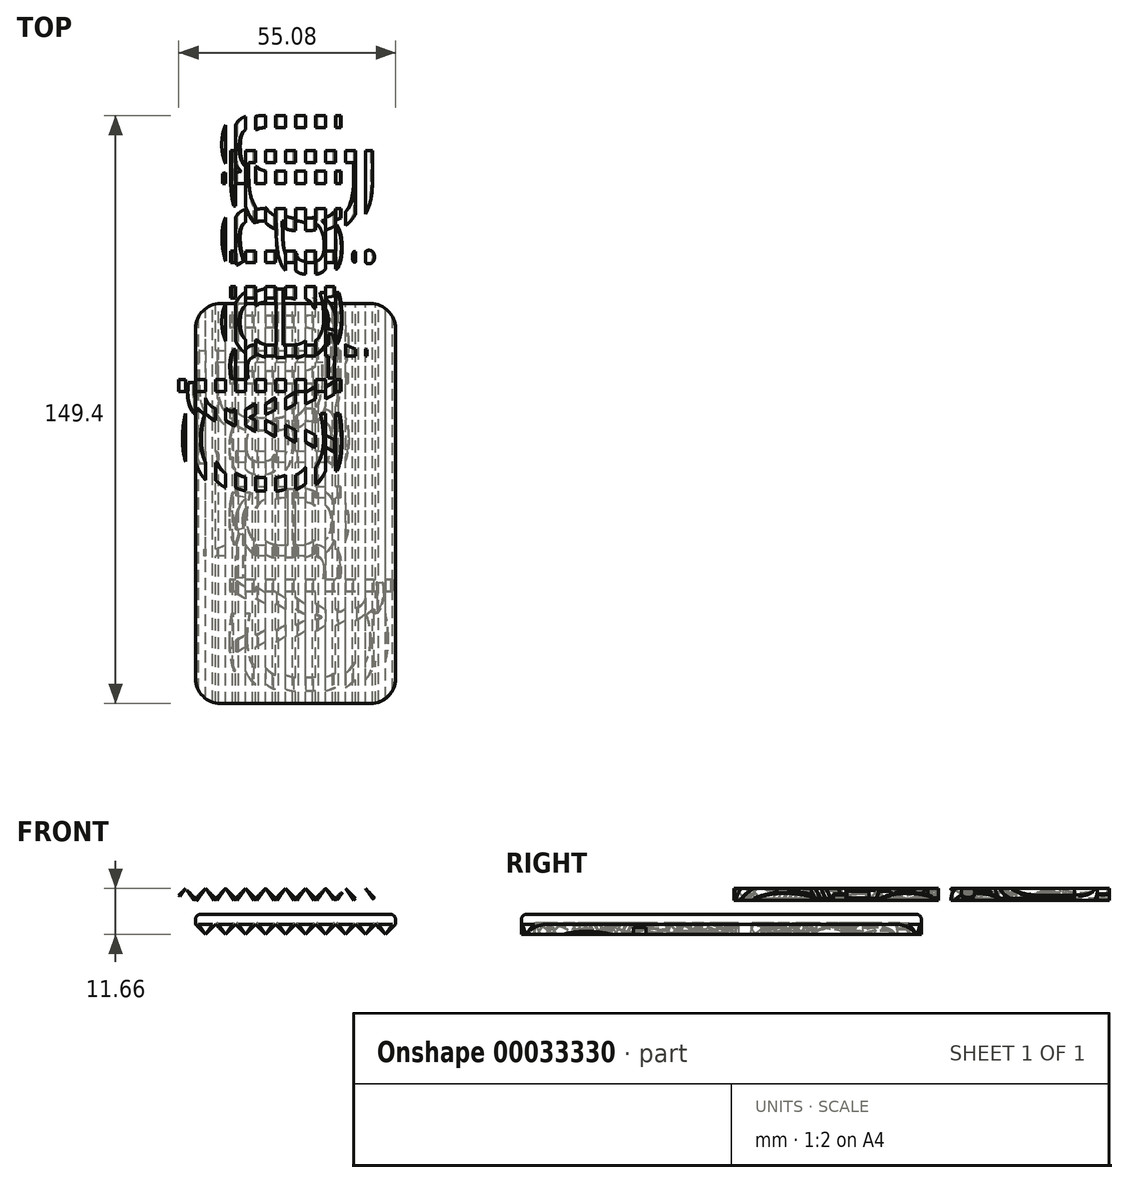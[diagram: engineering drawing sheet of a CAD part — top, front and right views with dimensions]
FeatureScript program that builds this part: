
annotation { "Feature Type Name" : "Feature", "Feature Type Description" : "" }
export const myFeature = defineFeature(function(context is Context, id is Id, definition is map)
    precondition{}
    {
        {
            var Q0;
            Q0=qCreatedBy(makeId("Front.planeOp"),FACE);
            var sketch = newSketch(context, id + "F0", { "sketchPlane" : qUnion([Q0])});
            skLineSegment(sketch, "E0.bottom", {"start": v(-20.32, 0) * mm, "end": v(30.48, 0) * mm});
            skLineSegment(sketch, "E0.top", {"start": v(-20.32, -2.54) * mm, "end": v(30.48, -2.54) * mm});
            skLineSegment(sketch, "E0.left", {"start": v(-20.32, 0) * mm, "end": v(-20.32, -2.54) * mm});
            skLineSegment(sketch, "E0.right", {"start": v(30.48, 0) * mm, "end": v(30.48, -2.54) * mm});
            skLineSegment(sketch, "E1", {"start": v(-20.32, -2.54) * mm, "end": v(-17.78, -5.08) * mm});
            skLineSegment(sketch, "E2", {"start": v(-17.78, -5.08) * mm, "end": v(-15.24, -2.54) * mm});
            skLineSegment(sketch, "E3", {"start": v(-15.24, -2.54) * mm, "end": v(-12.7, -5.08) * mm});
            skLineSegment(sketch, "E4", {"start": v(-12.7, -5.08) * mm, "end": v(-10.16, -2.54) * mm});
            skLineSegment(sketch, "E5", {"start": v(-10.16, -2.54) * mm, "end": v(-7.62, -5.08) * mm});
            skLineSegment(sketch, "E6", {"start": v(-7.62, -5.08) * mm, "end": v(-5.08, -2.54) * mm});
            skLineSegment(sketch, "E7", {"start": v(-5.08, -2.54) * mm, "end": v(-2.54, -5.08) * mm});
            skLineSegment(sketch, "E8", {"start": v(-2.54, -5.08) * mm, "end": v(0, -2.54) * mm});
            skLineSegment(sketch, "E9", {"start": v(0, -2.54) * mm, "end": v(2.54, -5.08) * mm});
            skLineSegment(sketch, "E10", {"start": v(2.54, -5.08) * mm, "end": v(5.08, -2.54) * mm});
            skLineSegment(sketch, "E11", {"start": v(5.08, -2.54) * mm, "end": v(7.62, -5.08) * mm});
            skLineSegment(sketch, "E12", {"start": v(7.62, -5.08) * mm, "end": v(10.16, -2.54) * mm});
            skLineSegment(sketch, "E13", {"start": v(10.16, -2.54) * mm, "end": v(12.7, -5.08) * mm});
            skLineSegment(sketch, "E14", {"start": v(12.7, -5.08) * mm, "end": v(15.24, -2.54) * mm});
            skLineSegment(sketch, "E15", {"start": v(15.24, -2.54) * mm, "end": v(17.78, -5.08) * mm});
            skLineSegment(sketch, "E16", {"start": v(17.78, -5.08) * mm, "end": v(20.32, -2.54) * mm});
            skLineSegment(sketch, "E17", {"start": v(20.32, -2.54) * mm, "end": v(22.86, -5.08) * mm});
            skLineSegment(sketch, "E18", {"start": v(22.86, -5.08) * mm, "end": v(25.4, -2.54) * mm});
            skLineSegment(sketch, "E19", {"start": v(25.4, -2.54) * mm, "end": v(27.94, -5.08) * mm});
            skLineSegment(sketch, "E20", {"start": v(27.94, -5.08) * mm, "end": v(30.48, -2.54) * mm});
            skLineSegment(sketch, "E21", {"start": v(-17.78, -5.08) * mm, "end": v(-19.56, -2.54) * mm});
            skLineSegment(sketch, "E22", {"start": v(-17.78, -5.08) * mm, "end": v(-16, -2.54) * mm});
            skLineSegment(sketch, "E23", {"start": v(-12.7, -5.08) * mm, "end": v(-14.48, -2.54) * mm});
            skLineSegment(sketch, "E24", {"start": v(-12.7, -5.08) * mm, "end": v(-10.92, -2.54) * mm});
            skLineSegment(sketch, "E25", {"start": v(-7.62, -5.08) * mm, "end": v(-9.4, -2.54) * mm});
            skLineSegment(sketch, "E26", {"start": v(-7.62, -5.08) * mm, "end": v(-5.84, -2.54) * mm});
            skLineSegment(sketch, "E27", {"start": v(-2.54, -5.08) * mm, "end": v(-4.32, -2.54) * mm});
            skLineSegment(sketch, "E28", {"start": v(-2.54, -5.08) * mm, "end": v(-0.76, -2.54) * mm});
            skLineSegment(sketch, "E29", {"start": v(2.54, -5.08) * mm, "end": v(0.76, -2.54) * mm});
            skLineSegment(sketch, "E30", {"start": v(2.54, -5.08) * mm, "end": v(4.32, -2.54) * mm});
            skLineSegment(sketch, "E31", {"start": v(7.62, -5.08) * mm, "end": v(9.4, -2.54) * mm});
            skLineSegment(sketch, "E32", {"start": v(7.62, -5.08) * mm, "end": v(5.84, -2.54) * mm});
            skLineSegment(sketch, "E33", {"start": v(12.7, -5.08) * mm, "end": v(10.92, -2.54) * mm});
            skLineSegment(sketch, "E34", {"start": v(12.7, -5.08) * mm, "end": v(14.48, -2.54) * mm});
            skLineSegment(sketch, "E35", {"start": v(17.78, -5.08) * mm, "end": v(16, -2.54) * mm});
            skLineSegment(sketch, "E36", {"start": v(17.78, -5.08) * mm, "end": v(19.56, -2.54) * mm});
            skLineSegment(sketch, "E37", {"start": v(22.86, -5.08) * mm, "end": v(24.64, -2.54) * mm});
            skLineSegment(sketch, "E38", {"start": v(22.86, -5.08) * mm, "end": v(21.08, -2.54) * mm});
            skLineSegment(sketch, "E39", {"start": v(27.94, -5.08) * mm, "end": v(29.72, -2.54) * mm});
            skLineSegment(sketch, "E40", {"start": v(27.94, -5.08) * mm, "end": v(26.16, -2.54) * mm});
            skSolve(sketch);
        }
        {
            var Q0;
            Q0=makeQuery(id+"F0.imprint","IMPRINT",FACE,{"disambiguationData":[TD([[makeQuery(id+"F0.imprint","IMPRINT",EDGE,{"derivedFrom":sQuery(id+"F0.wireOp",EDGE,"E0.bottom")}),-1.0]])]});
            var Q1;
            {var subQ1=sQuery(id+"F0.wireOp",EDGE,"E1");Q1=makeQuery(id+"F0.imprint","IMPRINT",FACE,{"disambiguationData":[TD([[makeQuery(id+"F0.imprint","IMPRINT",EDGE,{"derivedFrom":subQ1}),1.0]])]});}
            var Q2;
            {var subQ1=sQuery(id+"F0.wireOp",EDGE,"E21");Q2=makeQuery(id+"F0.imprint","IMPRINT",FACE,{"disambiguationData":[TD([[makeQuery(id+"F0.imprint","IMPRINT",EDGE,{"derivedFrom":subQ1}),-1.0]])]});}
            var Q3;
            {var subQ1=sQuery(id+"F0.wireOp",EDGE,"E2");Q3=makeQuery(id+"F0.imprint","IMPRINT",FACE,{"disambiguationData":[TD([[makeQuery(id+"F0.imprint","IMPRINT",EDGE,{"derivedFrom":subQ1}),1.0]])]});}
            var Q4;
            {var subQ1=sQuery(id+"F0.wireOp",EDGE,"E14");Q4=makeQuery(id+"F0.imprint","IMPRINT",FACE,{"disambiguationData":[TD([[makeQuery(id+"F0.imprint","IMPRINT",EDGE,{"derivedFrom":subQ1}),1.0]])]});}
            var Q5;
            {var subQ1=sQuery(id+"F0.wireOp",EDGE,"E16");Q5=makeQuery(id+"F0.imprint","IMPRINT",FACE,{"disambiguationData":[TD([[makeQuery(id+"F0.imprint","IMPRINT",EDGE,{"derivedFrom":subQ1}),1.0]])]});}
            var Q6;
            {var subQ1=sQuery(id+"F0.wireOp",EDGE,"E19");Q6=makeQuery(id+"F0.imprint","IMPRINT",FACE,{"disambiguationData":[TD([[makeQuery(id+"F0.imprint","IMPRINT",EDGE,{"derivedFrom":subQ1}),1.0]])]});}
            var Q7;
            {var subQ1=sQuery(id+"F0.wireOp",EDGE,"E33");Q7=makeQuery(id+"F0.imprint","IMPRINT",FACE,{"disambiguationData":[TD([[makeQuery(id+"F0.imprint","IMPRINT",EDGE,{"derivedFrom":subQ1}),-1.0]])]});}
            var Q8;
            {var subQ1=sQuery(id+"F0.wireOp",EDGE,"E6");Q8=makeQuery(id+"F0.imprint","IMPRINT",FACE,{"disambiguationData":[TD([[makeQuery(id+"F0.imprint","IMPRINT",EDGE,{"derivedFrom":subQ1}),1.0]])]});}
            var Q9;
            {var subQ1=sQuery(id+"F0.wireOp",EDGE,"E8");Q9=makeQuery(id+"F0.imprint","IMPRINT",FACE,{"disambiguationData":[TD([[makeQuery(id+"F0.imprint","IMPRINT",EDGE,{"derivedFrom":subQ1}),1.0]])]});}
            var Q10;
            {var subQ1=sQuery(id+"F0.wireOp",EDGE,"E13");Q10=makeQuery(id+"F0.imprint","IMPRINT",FACE,{"disambiguationData":[TD([[makeQuery(id+"F0.imprint","IMPRINT",EDGE,{"derivedFrom":subQ1}),1.0]])]});}
            var Q11;
            {var subQ0=sQuery(id+"F0.wireOp",EDGE,"E9");Q11=makeQuery(id+"F0.imprint","IMPRINT",FACE,{"disambiguationData":[TD([[makeQuery(id+"F0.imprint","IMPRINT",EDGE,{"derivedFrom":subQ0}),1.0]])]});}
            var Q12;
            {var subQ1=sQuery(id+"F0.wireOp",EDGE,"E12");Q12=makeQuery(id+"F0.imprint","IMPRINT",FACE,{"disambiguationData":[TD([[makeQuery(id+"F0.imprint","IMPRINT",EDGE,{"derivedFrom":subQ1}),1.0]])]});}
            var Q13;
            {var subQ1=sQuery(id+"F0.wireOp",EDGE,"E11");Q13=makeQuery(id+"F0.imprint","IMPRINT",FACE,{"disambiguationData":[TD([[makeQuery(id+"F0.imprint","IMPRINT",EDGE,{"derivedFrom":subQ1}),1.0]])]});}
            var Q14;
            {var subQ1=sQuery(id+"F0.wireOp",EDGE,"E10");Q14=makeQuery(id+"F0.imprint","IMPRINT",FACE,{"disambiguationData":[TD([[makeQuery(id+"F0.imprint","IMPRINT",EDGE,{"derivedFrom":subQ1}),1.0]])]});}
            var Q15;
            {var subQ1=sQuery(id+"F0.wireOp",EDGE,"E7");Q15=makeQuery(id+"F0.imprint","IMPRINT",FACE,{"disambiguationData":[TD([[makeQuery(id+"F0.imprint","IMPRINT",EDGE,{"derivedFrom":subQ1}),1.0]])]});}
            var Q16;
            {var subQ1=sQuery(id+"F0.wireOp",EDGE,"E25");Q16=makeQuery(id+"F0.imprint","IMPRINT",FACE,{"disambiguationData":[TD([[makeQuery(id+"F0.imprint","IMPRINT",EDGE,{"derivedFrom":subQ1}),-1.0]])]});}
            var Q17;
            {var subQ1=sQuery(id+"F0.wireOp",EDGE,"E15");Q17=makeQuery(id+"F0.imprint","IMPRINT",FACE,{"disambiguationData":[TD([[makeQuery(id+"F0.imprint","IMPRINT",EDGE,{"derivedFrom":subQ1}),1.0]])]});}
            var Q18;
            {var subQ1=sQuery(id+"F0.wireOp",EDGE,"E31");Q18=makeQuery(id+"F0.imprint","IMPRINT",FACE,{"disambiguationData":[TD([[makeQuery(id+"F0.imprint","IMPRINT",EDGE,{"derivedFrom":subQ1}),1.0]])]});}
            var Q19;
            {var subQ1=sQuery(id+"F0.wireOp",EDGE,"E3");Q19=makeQuery(id+"F0.imprint","IMPRINT",FACE,{"disambiguationData":[TD([[makeQuery(id+"F0.imprint","IMPRINT",EDGE,{"derivedFrom":subQ1}),1.0]])]});}
            var Q20;
            {var subQ1=sQuery(id+"F0.wireOp",EDGE,"E4");Q20=makeQuery(id+"F0.imprint","IMPRINT",FACE,{"disambiguationData":[TD([[makeQuery(id+"F0.imprint","IMPRINT",EDGE,{"derivedFrom":subQ1}),1.0]])]});}
            var Q21;
            {var subQ1=sQuery(id+"F0.wireOp",EDGE,"E5");Q21=makeQuery(id+"F0.imprint","IMPRINT",FACE,{"disambiguationData":[TD([[makeQuery(id+"F0.imprint","IMPRINT",EDGE,{"derivedFrom":subQ1}),1.0]])]});}
            var Q22;
            {var subQ0=sQuery(id+"F0.wireOp",EDGE,"E20");Q22=makeQuery(id+"F0.imprint","IMPRINT",FACE,{"disambiguationData":[TD([[makeQuery(id+"F0.imprint","IMPRINT",EDGE,{"derivedFrom":subQ0}),1.0]])]});}
            var Q23;
            {var subQ1=sQuery(id+"F0.wireOp",EDGE,"E27");Q23=makeQuery(id+"F0.imprint","IMPRINT",FACE,{"disambiguationData":[TD([[makeQuery(id+"F0.imprint","IMPRINT",EDGE,{"derivedFrom":subQ1}),-1.0]])]});}
            var Q24;
            {var subQ1=sQuery(id+"F0.wireOp",EDGE,"E35");Q24=makeQuery(id+"F0.imprint","IMPRINT",FACE,{"disambiguationData":[TD([[makeQuery(id+"F0.imprint","IMPRINT",EDGE,{"derivedFrom":subQ1}),-1.0]])]});}
            var Q25;
            {var subQ1=sQuery(id+"F0.wireOp",EDGE,"E39");Q25=makeQuery(id+"F0.imprint","IMPRINT",FACE,{"disambiguationData":[TD([[makeQuery(id+"F0.imprint","IMPRINT",EDGE,{"derivedFrom":subQ1}),1.0]])]});}
            var Q26;
            {var subQ1=sQuery(id+"F0.wireOp",EDGE,"E23");Q26=makeQuery(id+"F0.imprint","IMPRINT",FACE,{"disambiguationData":[TD([[makeQuery(id+"F0.imprint","IMPRINT",EDGE,{"derivedFrom":subQ1}),-1.0]])]});}
            var Q27;
            {var subQ1=sQuery(id+"F0.wireOp",EDGE,"E17");Q27=makeQuery(id+"F0.imprint","IMPRINT",FACE,{"disambiguationData":[TD([[makeQuery(id+"F0.imprint","IMPRINT",EDGE,{"derivedFrom":subQ1}),1.0]])]});}
            var Q28;
            {var subQ1=sQuery(id+"F0.wireOp",EDGE,"E18");Q28=makeQuery(id+"F0.imprint","IMPRINT",FACE,{"disambiguationData":[TD([[makeQuery(id+"F0.imprint","IMPRINT",EDGE,{"derivedFrom":subQ1}),1.0]])]});}
            var Q29;
            {var subQ0=sQuery(id+"F0.wireOp",EDGE,"E29");Q29=makeQuery(id+"F0.imprint","IMPRINT",FACE,{"disambiguationData":[TD([[makeQuery(id+"F0.imprint","IMPRINT",EDGE,{"derivedFrom":subQ0}),-1.0]])]});}
            var Q30;
            {var subQ1=sQuery(id+"F0.wireOp",EDGE,"E37");Q30=makeQuery(id+"F0.imprint","IMPRINT",FACE,{"disambiguationData":[TD([[makeQuery(id+"F0.imprint","IMPRINT",EDGE,{"derivedFrom":subQ1}),1.0]])]});}
            extrude(context, id + "F1", {"entities" : qUnion([Q0, Q1, Q2, Q3, Q4, Q5, Q6, Q7, Q8, Q9, Q10, Q11, Q12, Q13, Q14, Q15, Q16, Q17, Q18, Q19, Q20, Q21, Q22, Q23, Q24, Q25, Q26, Q27, Q28, Q29, Q30]), "depth" : 101.6 * mm});
        }
        {
            var Q0;
            {var subQ1=sQuery(id+"F0.wireOp",EDGE,"E39");Q0=makeQuery(id+"F0.imprint","IMPRINT",FACE,{"disambiguationData":[TD([[makeQuery(id+"F0.imprint","IMPRINT",EDGE,{"derivedFrom":subQ1}),1.0]])]});}
            var Q1;
            {var subQ1=sQuery(id+"F0.wireOp",EDGE,"E37");Q1=makeQuery(id+"F0.imprint","IMPRINT",FACE,{"disambiguationData":[TD([[makeQuery(id+"F0.imprint","IMPRINT",EDGE,{"derivedFrom":subQ1}),1.0]])]});}
            var Q2;
            {var subQ1=sQuery(id+"F0.wireOp",EDGE,"E35");Q2=makeQuery(id+"F0.imprint","IMPRINT",FACE,{"disambiguationData":[TD([[makeQuery(id+"F0.imprint","IMPRINT",EDGE,{"derivedFrom":subQ1}),-1.0]])]});}
            var Q3;
            {var subQ1=sQuery(id+"F0.wireOp",EDGE,"E33");Q3=makeQuery(id+"F0.imprint","IMPRINT",FACE,{"disambiguationData":[TD([[makeQuery(id+"F0.imprint","IMPRINT",EDGE,{"derivedFrom":subQ1}),-1.0]])]});}
            var Q4;
            {var subQ1=sQuery(id+"F0.wireOp",EDGE,"E31");Q4=makeQuery(id+"F0.imprint","IMPRINT",FACE,{"disambiguationData":[TD([[makeQuery(id+"F0.imprint","IMPRINT",EDGE,{"derivedFrom":subQ1}),1.0]])]});}
            var Q5;
            {var subQ0=sQuery(id+"F0.wireOp",EDGE,"E29");Q5=makeQuery(id+"F0.imprint","IMPRINT",FACE,{"disambiguationData":[TD([[makeQuery(id+"F0.imprint","IMPRINT",EDGE,{"derivedFrom":subQ0}),-1.0]])]});}
            var Q6;
            {var subQ1=sQuery(id+"F0.wireOp",EDGE,"E27");Q6=makeQuery(id+"F0.imprint","IMPRINT",FACE,{"disambiguationData":[TD([[makeQuery(id+"F0.imprint","IMPRINT",EDGE,{"derivedFrom":subQ1}),-1.0]])]});}
            var Q7;
            {var subQ1=sQuery(id+"F0.wireOp",EDGE,"E25");Q7=makeQuery(id+"F0.imprint","IMPRINT",FACE,{"disambiguationData":[TD([[makeQuery(id+"F0.imprint","IMPRINT",EDGE,{"derivedFrom":subQ1}),-1.0]])]});}
            var Q8;
            {var subQ1=sQuery(id+"F0.wireOp",EDGE,"E23");Q8=makeQuery(id+"F0.imprint","IMPRINT",FACE,{"disambiguationData":[TD([[makeQuery(id+"F0.imprint","IMPRINT",EDGE,{"derivedFrom":subQ1}),-1.0]])]});}
            var Q9;
            {var subQ1=sQuery(id+"F0.wireOp",EDGE,"E21");Q9=makeQuery(id+"F0.imprint","IMPRINT",FACE,{"disambiguationData":[TD([[makeQuery(id+"F0.imprint","IMPRINT",EDGE,{"derivedFrom":subQ1}),-1.0]])]});}
            extrude(context, id + "F2", {"entities" : qUnion([Q0, Q1, Q2, Q3, Q4, Q5, Q6, Q7, Q8, Q9]), "depth" : 101.6 * mm});
        }
        {
            var Q0;
            Q0=makeQuery(id+"F1.opExtrude","SWEPT_FACE",FACE,{"disambiguationData":[OSD([sQuery(id+"F0.wireOp",EDGE,"E16")])]});
            cPlane(context, id + "F3", {"entities" : qUnion([Q0]), "cplaneType" : CPlaneType.OFFSET, "offset" : 12.7 * mm, "width" : 152.4 * mm, "height" : 152.4 * mm});
        }
        {
            var Q0;
            Q0=makeQuery(id+"F1.opExtrude","SWEPT_FACE",FACE,{"disambiguationData":[OSD([sQuery(id+"F0.wireOp",EDGE,"E5")])]});
            cPlane(context, id + "F4", {"entities" : qUnion([Q0]), "cplaneType" : CPlaneType.OFFSET, "offset" : 15.24 * mm, "width" : 152.4 * mm, "height" : 152.4 * mm});
        }
        {
            var Q0;
            Q0=qCreatedBy(id+"F3.planeOp",FACE);
            var sketch = newSketch(context, id + "F5", { "sketchPlane" : qUnion([Q0])});
            skText(sketch, "E41", { "text": "Clean", "fontName": "OpenSans-Regular.ttf"});
            skLineSegment(sketch, "E42", {"start": v(-0.73, 16.16) * mm, "end": v(-103.2, 16.16) * mm});
            skLineSegment(sketch, "E43", {"start": v(-103.05, 12.57) * mm, "end": v(-1.71, 12.57) * mm});
            skLineSegment(sketch, "E44", {"start": v(-1.26, 8.98) * mm, "end": v(-105.16, 8.98) * mm});
            skLineSegment(sketch, "E45", {"start": v(-103.35, 5.39) * mm, "end": v(-1.34, 5.39) * mm});
            skLineSegment(sketch, "E46", {"start": v(-1.49, 1.8) * mm, "end": v(-105.62, 1.8) * mm});
            skLineSegment(sketch, "E47", {"start": v(-104.1, -1.8) * mm, "end": v(-1.19, -1.8) * mm});
            skLineSegment(sketch, "E48", {"start": v(-1.56, -5.39) * mm, "end": v(-107.58, -5.39) * mm});
            skLineSegment(sketch, "E49", {"start": v(-104.63, -8.98) * mm, "end": v(-1.03, -8.98) * mm});
            const initialGuessF5  = {"E41": [-0.10082, -0.0107, 1, 0, 0.02779]};
            skSetInitialGuess(sketch, initialGuessF5);
            skSolve(sketch);
        }
        {
            var Q0;
            {var subQ1=sQuery(id+"F5.wireOp",EDGE,"E41.sketch_text.stroke-12");var subQ3=sQuery(id+"F5.wireOp",EDGE,"E41.sketch_text.stroke-11");var subQ5=makeQuery(id+"F5.imprint","INTERSECT",VERTEX,{"derivedFrom":[subQ3,subQ1]});Q0=makeQuery(id+"F5.imprint","IMPRINT",FACE,{"disambiguationData":[TD([[makeQuery(id+"F5.imprint","IMPRINT",EDGE,{"disambiguationData":[TD([[subQ5,1.0]])],"derivedFrom":subQ3}),-1.0]])]});}
            var Q1;
            {var subQ5=sQuery(id+"F5.wireOp",EDGE,"E41.sketch_text.stroke-17");Q1=makeQuery(id+"F5.imprint","IMPRINT",FACE,{"disambiguationData":[TD([[makeQuery(id+"F5.imprint","IMPRINT",EDGE,{"derivedFrom":subQ5}),-1.0]])]});}
            var Q2;
            Q2=makeQuery(id+"F2.opExtrude","SWEPT_FACE",FACE,{"disambiguationData":[OSD([sQuery(id+"F0.wireOp",EDGE,"E39")])]});
            extrude(context, id + "F6", {"entities" : qUnion([Q0, Q1]), "operationType" : NewBodyOperationType.REMOVE, "endBound" : BoundingType.UP_TO_SURFACE, "oppositeDirection" : true, "endBoundEntityFace" : qUnion([Q2]), "depth" : 25.4 * mm});
        }
        {
            var Q0;
            {var subQ11=sQuery(id+"F5.wireOp",EDGE,"E41.sketch_text.stroke-13");Q0=makeQuery(id+"F5.imprint","IMPRINT",FACE,{"disambiguationData":[TD([[makeQuery(id+"F5.imprint","IMPRINT",EDGE,{"derivedFrom":subQ11}),-1.0]])]});}
            var Q1;
            {var subQ1=sQuery(id+"F5.wireOp",EDGE,"E41.sketch_text.stroke-16");var subQ5=sQuery(id+"F5.wireOp",EDGE,"E42");var subQ6=makeQuery(id+"F5.imprint","INTERSECT",VERTEX,{"derivedFrom":[subQ1,subQ5]});Q1=makeQuery(id+"F5.imprint","IMPRINT",FACE,{"disambiguationData":[TD([[makeQuery(id+"F5.imprint","IMPRINT",EDGE,{"disambiguationData":[TD([[subQ6,1.0]])],"derivedFrom":subQ1}),-1.0]])]});}
            var Q2;
            Q2=makeQuery(id+"F2.opExtrude","SWEPT_FACE",FACE,{"disambiguationData":[OSD([sQuery(id+"F0.wireOp",EDGE,"E37")])]});
            extrude(context, id + "F7", {"entities" : qUnion([Q0, Q1]), "operationType" : NewBodyOperationType.REMOVE, "endBound" : BoundingType.UP_TO_SURFACE, "oppositeDirection" : true, "endBoundEntityFace" : qUnion([Q2]), "depth" : 25.4 * mm});
        }
        {
            var Q0;
            {var subQ1=sQuery(id+"F5.wireOp",EDGE,"E41.sketch_text.stroke-1");var subQ6=sQuery(id+"F5.wireOp",EDGE,"E41.sketch_text.stroke-0");var subQ11=makeQuery(id+"F5.imprint","INTERSECT",VERTEX,{"derivedFrom":[subQ6,subQ1]});Q0=makeQuery(id+"F5.imprint","IMPRINT",FACE,{"disambiguationData":[TD([[makeQuery(id+"F5.imprint","IMPRINT",EDGE,{"disambiguationData":[TD([[subQ11,1.0]])],"derivedFrom":subQ6}),-1.0]])]});}
            var Q1;
            {var subQ0=sQuery(id+"F5.wireOp",EDGE,"E44");var subQ1=sQuery(id+"F5.wireOp",EDGE,"E41.sketch_text.stroke-16");var subQ2=makeQuery(id+"F5.imprint","INTERSECT",VERTEX,{"derivedFrom":[subQ1,subQ0]});Q1=makeQuery(id+"F5.imprint","IMPRINT",FACE,{"disambiguationData":[TD([[makeQuery(id+"F5.imprint","IMPRINT",EDGE,{"disambiguationData":[TD([[subQ2,-1.0]])],"derivedFrom":subQ1}),-1.0]])]});}
            var Q2;
            {var subQ1=sQuery(id+"F5.wireOp",EDGE,"E41.sketch_text.stroke-23");var subQ3=sQuery(id+"F5.wireOp",EDGE,"E41.sketch_text.stroke-22");var subQ5=makeQuery(id+"F5.imprint","INTERSECT",VERTEX,{"derivedFrom":[subQ3,subQ1]});Q2=makeQuery(id+"F5.imprint","IMPRINT",FACE,{"disambiguationData":[TD([[makeQuery(id+"F5.imprint","IMPRINT",EDGE,{"disambiguationData":[TD([[subQ5,1.0]])],"derivedFrom":subQ3}),-1.0]])]});}
            var Q3;
            {var subQ5=sQuery(id+"F5.wireOp",EDGE,"E41.sketch_text.stroke-52");Q3=makeQuery(id+"F5.imprint","IMPRINT",FACE,{"disambiguationData":[TD([[makeQuery(id+"F5.imprint","IMPRINT",EDGE,{"derivedFrom":subQ5}),-1.0]])]});}
            var Q4;
            {var subQ5=sQuery(id+"F5.wireOp",EDGE,"E41.sketch_text.stroke-77");Q4=makeQuery(id+"F5.imprint","IMPRINT",FACE,{"disambiguationData":[TD([[makeQuery(id+"F5.imprint","IMPRINT",EDGE,{"derivedFrom":subQ5}),-1.0]])]});}
            var Q5;
            {var subQ5=sQuery(id+"F5.wireOp",EDGE,"E41.sketch_text.stroke-73");Q5=makeQuery(id+"F5.imprint","IMPRINT",FACE,{"disambiguationData":[TD([[makeQuery(id+"F5.imprint","IMPRINT",EDGE,{"derivedFrom":subQ5}),-1.0]])]});}
            var Q6;
            Q6=makeQuery(id+"F2.opExtrude","SWEPT_FACE",FACE,{"disambiguationData":[OSD([sQuery(id+"F0.wireOp",EDGE,"E36")])]});
            extrude(context, id + "F8", {"entities" : qUnion([Q0, Q1, Q2, Q3, Q4, Q5]), "operationType" : NewBodyOperationType.REMOVE, "endBound" : BoundingType.UP_TO_SURFACE, "oppositeDirection" : true, "endBoundEntityFace" : qUnion([Q6]), "depth" : 25.4 * mm});
        }
        {
            var Q0;
            {var subQ1=sQuery(id+"F5.wireOp",EDGE,"E41.sketch_text.stroke-1");var subQ5=sQuery(id+"F5.wireOp",EDGE,"E44");var subQ6=makeQuery(id+"F5.imprint","INTERSECT",VERTEX,{"derivedFrom":[subQ1,subQ5]});Q0=makeQuery(id+"F5.imprint","IMPRINT",FACE,{"disambiguationData":[TD([[makeQuery(id+"F5.imprint","IMPRINT",EDGE,{"disambiguationData":[TD([[subQ6,-1.0]])],"derivedFrom":subQ1}),-1.0]])]});}
            var Q1;
            {var subQ0=sQuery(id+"F5.wireOp",EDGE,"E45");var subQ3=sQuery(id+"F5.wireOp",EDGE,"E41.sketch_text.stroke-16");var subQ4=makeQuery(id+"F5.imprint","INTERSECT",VERTEX,{"derivedFrom":[subQ3,subQ0]});Q1=makeQuery(id+"F5.imprint","IMPRINT",FACE,{"disambiguationData":[TD([[makeQuery(id+"F5.imprint","IMPRINT",EDGE,{"disambiguationData":[TD([[subQ4,-1.0]])],"derivedFrom":subQ3}),-1.0]])]});}
            var Q2;
            {var subQ15=sQuery(id+"F5.wireOp",EDGE,"E41.sketch_text.stroke-33");Q2=makeQuery(id+"F5.imprint","IMPRINT",FACE,{"disambiguationData":[TD([[makeQuery(id+"F5.imprint","IMPRINT",EDGE,{"derivedFrom":subQ15}),-1.0]])]});}
            var Q3;
            {var subQ12=sQuery(id+"F5.wireOp",EDGE,"E41.sketch_text.stroke-48");Q3=makeQuery(id+"F5.imprint","IMPRINT",FACE,{"disambiguationData":[TD([[makeQuery(id+"F5.imprint","IMPRINT",EDGE,{"derivedFrom":subQ12}),-1.0]])]});}
            var Q4;
            {var subQ20=sQuery(id+"F5.wireOp",EDGE,"E41.sketch_text.stroke-67");Q4=makeQuery(id+"F5.imprint","IMPRINT",FACE,{"disambiguationData":[TD([[makeQuery(id+"F5.imprint","IMPRINT",EDGE,{"derivedFrom":subQ20}),-1.0]])]});}
            var Q5;
            Q5=makeQuery(id+"F2.opExtrude","SWEPT_FACE",FACE,{"disambiguationData":[OSD([sQuery(id+"F0.wireOp",EDGE,"E34")])]});
            extrude(context, id + "F9", {"entities" : qUnion([Q0, Q1, Q2, Q3, Q4]), "operationType" : NewBodyOperationType.REMOVE, "endBound" : BoundingType.UP_TO_SURFACE, "oppositeDirection" : true, "endBoundEntityFace" : qUnion([Q5]), "depth" : 25.4 * mm});
        }
        {
            var Q0;
            {var subQ1=sQuery(id+"F5.wireOp",EDGE,"E41.sketch_text.stroke-2");var subQ6=sQuery(id+"F5.wireOp",EDGE,"E41.sketch_text.stroke-1");var subQ11=makeQuery(id+"F5.imprint","INTERSECT",VERTEX,{"derivedFrom":[subQ6,subQ1]});Q0=makeQuery(id+"F5.imprint","IMPRINT",FACE,{"disambiguationData":[TD([[makeQuery(id+"F5.imprint","IMPRINT",EDGE,{"disambiguationData":[TD([[subQ11,1.0]])],"derivedFrom":subQ6}),-1.0]])]});}
            var Q1;
            {var subQ0=sQuery(id+"F5.wireOp",EDGE,"E46");var subQ3=sQuery(id+"F5.wireOp",EDGE,"E41.sketch_text.stroke-16");var subQ4=makeQuery(id+"F5.imprint","INTERSECT",VERTEX,{"derivedFrom":[subQ3,subQ0]});Q1=makeQuery(id+"F5.imprint","IMPRINT",FACE,{"disambiguationData":[TD([[makeQuery(id+"F5.imprint","IMPRINT",EDGE,{"disambiguationData":[TD([[subQ4,-1.0]])],"derivedFrom":subQ3}),-1.0]])]});}
            var Q2;
            {var subQ0=sQuery(id+"F5.wireOp",EDGE,"E46");var subQ3=sQuery(id+"F5.wireOp",EDGE,"E41.sketch_text.stroke-21");var subQ4=makeQuery(id+"F5.imprint","INTERSECT",VERTEX,{"derivedFrom":[subQ3,subQ0]});Q2=makeQuery(id+"F5.imprint","IMPRINT",FACE,{"disambiguationData":[TD([[makeQuery(id+"F5.imprint","IMPRINT",EDGE,{"disambiguationData":[TD([[subQ4,-1.0]])],"derivedFrom":subQ3}),-1.0]])]});}
            var Q3;
            {var subQ3=sQuery(id+"F5.wireOp",EDGE,"E41.sketch_text.stroke-24");var subQ5=sQuery(id+"F5.wireOp",EDGE,"E45");var subQ7=makeQuery(id+"F5.imprint","INTERSECT",VERTEX,{"derivedFrom":[subQ3,subQ5]});Q3=makeQuery(id+"F5.imprint","IMPRINT",FACE,{"disambiguationData":[TD([[makeQuery(id+"F5.imprint","IMPRINT",EDGE,{"disambiguationData":[TD([[subQ7,-1.0]])],"derivedFrom":subQ3}),-1.0]])]});}
            var Q4;
            {var subQ3=sQuery(id+"F5.wireOp",EDGE,"E41.sketch_text.stroke-46");var subQ8=sQuery(id+"F5.wireOp",EDGE,"E41.sketch_text.stroke-47");var subQ11=makeQuery(id+"F5.imprint","INTERSECT",VERTEX,{"derivedFrom":[subQ3,subQ8]});Q4=makeQuery(id+"F5.imprint","IMPRINT",FACE,{"disambiguationData":[TD([[makeQuery(id+"F5.imprint","IMPRINT",EDGE,{"disambiguationData":[TD([[subQ11,1.0]])],"derivedFrom":subQ3}),-1.0]])]});}
            var Q5;
            {var subQ3=sQuery(id+"F5.wireOp",EDGE,"E41.sketch_text.stroke-69");var subQ5=sQuery(id+"F5.wireOp",EDGE,"E45");var subQ7=makeQuery(id+"F5.imprint","INTERSECT",VERTEX,{"derivedFrom":[subQ3,subQ5]});Q5=makeQuery(id+"F5.imprint","IMPRINT",FACE,{"disambiguationData":[TD([[makeQuery(id+"F5.imprint","IMPRINT",EDGE,{"disambiguationData":[TD([[subQ7,-1.0]])],"derivedFrom":subQ3}),-1.0]])]});}
            var Q6;
            {var subQ1=sQuery(id+"F5.wireOp",EDGE,"E41.sketch_text.stroke-65");var subQ6=sQuery(id+"F5.wireOp",EDGE,"E41.sketch_text.stroke-66");var subQ11=makeQuery(id+"F5.imprint","INTERSECT",VERTEX,{"derivedFrom":[subQ1,subQ6]});Q6=makeQuery(id+"F5.imprint","IMPRINT",FACE,{"disambiguationData":[TD([[makeQuery(id+"F5.imprint","IMPRINT",EDGE,{"disambiguationData":[TD([[subQ11,1.0]])],"derivedFrom":subQ1}),-1.0]])]});}
            var Q7;
            Q7=makeQuery(id+"F2.opExtrude","SWEPT_FACE",FACE,{"disambiguationData":[OSD([sQuery(id+"F0.wireOp",EDGE,"E31")])]});
            extrude(context, id + "F10", {"entities" : qUnion([Q0, Q1, Q2, Q3, Q4, Q5, Q6]), "operationType" : NewBodyOperationType.REMOVE, "endBound" : BoundingType.UP_TO_SURFACE, "oppositeDirection" : true, "endBoundEntityFace" : qUnion([Q7]), "depth" : 25.4 * mm});
        }
        {
            var Q0;
            {var subQ1=sQuery(id+"F5.wireOp",EDGE,"E41.sketch_text.stroke-2");var subQ5=sQuery(id+"F5.wireOp",EDGE,"E46");var subQ6=makeQuery(id+"F5.imprint","INTERSECT",VERTEX,{"derivedFrom":[subQ1,subQ5]});Q0=makeQuery(id+"F5.imprint","IMPRINT",FACE,{"disambiguationData":[TD([[makeQuery(id+"F5.imprint","IMPRINT",EDGE,{"disambiguationData":[TD([[subQ6,-1.0]])],"derivedFrom":subQ1}),-1.0]])]});}
            var Q1;
            {var subQ0=sQuery(id+"F5.wireOp",EDGE,"E47");var subQ3=sQuery(id+"F5.wireOp",EDGE,"E41.sketch_text.stroke-16");var subQ4=makeQuery(id+"F5.imprint","INTERSECT",VERTEX,{"derivedFrom":[subQ3,subQ0]});Q1=makeQuery(id+"F5.imprint","IMPRINT",FACE,{"disambiguationData":[TD([[makeQuery(id+"F5.imprint","IMPRINT",EDGE,{"disambiguationData":[TD([[subQ4,-1.0]])],"derivedFrom":subQ3}),-1.0]])]});}
            var Q2;
            {var subQ16=sQuery(id+"F5.wireOp",EDGE,"E41.sketch_text.stroke-25");Q2=makeQuery(id+"F5.imprint","IMPRINT",FACE,{"disambiguationData":[TD([[makeQuery(id+"F5.imprint","IMPRINT",EDGE,{"derivedFrom":subQ16}),-1.0]])]});}
            var Q3;
            {var subQ14=sQuery(id+"F5.wireOp",EDGE,"E41.sketch_text.stroke-45");Q3=makeQuery(id+"F5.imprint","IMPRINT",FACE,{"disambiguationData":[TD([[makeQuery(id+"F5.imprint","IMPRINT",EDGE,{"derivedFrom":subQ14}),-1.0]])]});}
            var Q4;
            {var subQ3=sQuery(id+"F5.wireOp",EDGE,"E41.sketch_text.stroke-70");var subQ7=sQuery(id+"F5.wireOp",EDGE,"E41.sketch_text.stroke-69");var subQ9=makeQuery(id+"F5.imprint","INTERSECT",VERTEX,{"derivedFrom":[subQ7,subQ3]});Q4=makeQuery(id+"F5.imprint","IMPRINT",FACE,{"disambiguationData":[TD([[makeQuery(id+"F5.imprint","IMPRINT",EDGE,{"disambiguationData":[TD([[subQ9,1.0]])],"derivedFrom":subQ7}),-1.0]])]});}
            var Q5;
            {var subQ0=sQuery(id+"F5.wireOp",EDGE,"E47");var subQ1=sQuery(id+"F5.wireOp",EDGE,"E41.sketch_text.stroke-65");var subQ2=makeQuery(id+"F5.imprint","INTERSECT",VERTEX,{"derivedFrom":[subQ1,subQ0]});Q5=makeQuery(id+"F5.imprint","IMPRINT",FACE,{"disambiguationData":[TD([[makeQuery(id+"F5.imprint","IMPRINT",EDGE,{"disambiguationData":[TD([[subQ2,-1.0]])],"derivedFrom":subQ1}),-1.0]])]});}
            var Q6;
            Q6=makeQuery(id+"F2.opExtrude","SWEPT_FACE",FACE,{"disambiguationData":[OSD([sQuery(id+"F0.wireOp",EDGE,"E30")])]});
            extrude(context, id + "F11", {"entities" : qUnion([Q0, Q1, Q2, Q3, Q4, Q5]), "operationType" : NewBodyOperationType.REMOVE, "endBound" : BoundingType.UP_TO_SURFACE, "oppositeDirection" : true, "endBoundEntityFace" : qUnion([Q6]), "depth" : 25.4 * mm});
        }
        {
            var Q0;
            {var subQ1=sQuery(id+"F5.wireOp",EDGE,"E41.sketch_text.stroke-3");var subQ6=sQuery(id+"F5.wireOp",EDGE,"E41.sketch_text.stroke-2");var subQ9=makeQuery(id+"F5.imprint","INTERSECT",VERTEX,{"derivedFrom":[subQ6,subQ1]});Q0=makeQuery(id+"F5.imprint","IMPRINT",FACE,{"disambiguationData":[TD([[makeQuery(id+"F5.imprint","IMPRINT",EDGE,{"disambiguationData":[TD([[subQ9,1.0]])],"derivedFrom":subQ6}),-1.0]])]});}
            var Q1;
            {var subQ0=sQuery(id+"F5.wireOp",EDGE,"E48");var subQ3=sQuery(id+"F5.wireOp",EDGE,"E41.sketch_text.stroke-16");var subQ4=makeQuery(id+"F5.imprint","INTERSECT",VERTEX,{"derivedFrom":[subQ3,subQ0]});Q1=makeQuery(id+"F5.imprint","IMPRINT",FACE,{"disambiguationData":[TD([[makeQuery(id+"F5.imprint","IMPRINT",EDGE,{"disambiguationData":[TD([[subQ4,-1.0]])],"derivedFrom":subQ3}),-1.0]])]});}
            var Q2;
            {var subQ0=sQuery(id+"F5.wireOp",EDGE,"E48");var subQ3=sQuery(id+"F5.wireOp",EDGE,"E41.sketch_text.stroke-20");var subQ4=makeQuery(id+"F5.imprint","INTERSECT",VERTEX,{"derivedFrom":[subQ3,subQ0]});Q2=makeQuery(id+"F5.imprint","IMPRINT",FACE,{"disambiguationData":[TD([[makeQuery(id+"F5.imprint","IMPRINT",EDGE,{"disambiguationData":[TD([[subQ4,-1.0]])],"derivedFrom":subQ3}),-1.0]])]});}
            var Q3;
            {var subQ10=sQuery(id+"F5.wireOp",EDGE,"E41.sketch_text.stroke-62");Q3=makeQuery(id+"F5.imprint","IMPRINT",FACE,{"disambiguationData":[TD([[makeQuery(id+"F5.imprint","IMPRINT",EDGE,{"derivedFrom":subQ10}),-1.0]])]});}
            var Q4;
            {var subQ3=sQuery(id+"F5.wireOp",EDGE,"E41.sketch_text.stroke-55");var subQ5=sQuery(id+"F5.wireOp",EDGE,"E47");var subQ8=makeQuery(id+"F5.imprint","INTERSECT",VERTEX,{"derivedFrom":[subQ3,subQ5]});Q4=makeQuery(id+"F5.imprint","IMPRINT",FACE,{"disambiguationData":[TD([[makeQuery(id+"F5.imprint","IMPRINT",EDGE,{"disambiguationData":[TD([[subQ8,-1.0]])],"derivedFrom":subQ3}),-1.0]])]});}
            var Q5;
            {var subQ3=sQuery(id+"F5.wireOp",EDGE,"E41.sketch_text.stroke-70");var subQ5=sQuery(id+"F5.wireOp",EDGE,"E47");var subQ7=makeQuery(id+"F5.imprint","INTERSECT",VERTEX,{"derivedFrom":[subQ3,subQ5]});Q5=makeQuery(id+"F5.imprint","IMPRINT",FACE,{"disambiguationData":[TD([[makeQuery(id+"F5.imprint","IMPRINT",EDGE,{"disambiguationData":[TD([[subQ7,-1.0]])],"derivedFrom":subQ3}),-1.0]])]});}
            var Q6;
            {var subQ1=sQuery(id+"F5.wireOp",EDGE,"E41.sketch_text.stroke-65");var subQ5=sQuery(id+"F5.wireOp",EDGE,"E48");var subQ6=makeQuery(id+"F5.imprint","INTERSECT",VERTEX,{"derivedFrom":[subQ1,subQ5]});Q6=makeQuery(id+"F5.imprint","IMPRINT",FACE,{"disambiguationData":[TD([[makeQuery(id+"F5.imprint","IMPRINT",EDGE,{"disambiguationData":[TD([[subQ6,-1.0]])],"derivedFrom":subQ1}),-1.0]])]});}
            var Q7;
            Q7=makeQuery(id+"F2.opExtrude","SWEPT_FACE",FACE,{"disambiguationData":[OSD([sQuery(id+"F0.wireOp",EDGE,"E28")])]});
            extrude(context, id + "F12", {"entities" : qUnion([Q0, Q1, Q2, Q3, Q4, Q5, Q6]), "operationType" : NewBodyOperationType.REMOVE, "endBound" : BoundingType.UP_TO_SURFACE, "oppositeDirection" : true, "endBoundEntityFace" : qUnion([Q7]), "depth" : 25.4 * mm});
        }
        {
            var Q0;
            {var subQ11=sQuery(id+"F5.wireOp",EDGE,"E41.sketch_text.stroke-4");Q0=makeQuery(id+"F5.imprint","IMPRINT",FACE,{"disambiguationData":[TD([[makeQuery(id+"F5.imprint","IMPRINT",EDGE,{"derivedFrom":subQ11}),-1.0]])]});}
            var Q1;
            {var subQ0=sQuery(id+"F5.wireOp",EDGE,"E49");var subQ3=sQuery(id+"F5.wireOp",EDGE,"E41.sketch_text.stroke-16");var subQ4=makeQuery(id+"F5.imprint","INTERSECT",VERTEX,{"derivedFrom":[subQ3,subQ0]});Q1=makeQuery(id+"F5.imprint","IMPRINT",FACE,{"disambiguationData":[TD([[makeQuery(id+"F5.imprint","IMPRINT",EDGE,{"disambiguationData":[TD([[subQ4,-1.0]])],"derivedFrom":subQ3}),-1.0]])]});}
            var Q2;
            {var subQ11=sQuery(id+"F5.wireOp",EDGE,"E41.sketch_text.stroke-28");Q2=makeQuery(id+"F5.imprint","IMPRINT",FACE,{"disambiguationData":[TD([[makeQuery(id+"F5.imprint","IMPRINT",EDGE,{"derivedFrom":subQ11}),-1.0]])]});}
            var Q3;
            {var subQ18=sQuery(id+"F5.wireOp",EDGE,"E41.sketch_text.stroke-39");Q3=makeQuery(id+"F5.imprint","IMPRINT",FACE,{"disambiguationData":[TD([[makeQuery(id+"F5.imprint","IMPRINT",EDGE,{"derivedFrom":subQ18}),-1.0]])]});}
            var Q4;
            {var subQ0=sQuery(id+"F5.wireOp",EDGE,"E49");var subQ3=sQuery(id+"F5.wireOp",EDGE,"E41.sketch_text.stroke-70");var subQ4=makeQuery(id+"F5.imprint","INTERSECT",VERTEX,{"derivedFrom":[subQ3,subQ0]});Q4=makeQuery(id+"F5.imprint","IMPRINT",FACE,{"disambiguationData":[TD([[makeQuery(id+"F5.imprint","IMPRINT",EDGE,{"disambiguationData":[TD([[subQ4,1.0]])],"derivedFrom":subQ3}),-1.0]])]});}
            var Q5;
            {var subQ0=sQuery(id+"F5.wireOp",EDGE,"E49");var subQ1=sQuery(id+"F5.wireOp",EDGE,"E41.sketch_text.stroke-65");var subQ2=makeQuery(id+"F5.imprint","INTERSECT",VERTEX,{"derivedFrom":[subQ1,subQ0]});Q5=makeQuery(id+"F5.imprint","IMPRINT",FACE,{"disambiguationData":[TD([[makeQuery(id+"F5.imprint","IMPRINT",EDGE,{"disambiguationData":[TD([[subQ2,-1.0]])],"derivedFrom":subQ1}),-1.0]])]});}
            var Q6;
            Q6=makeQuery(id+"F2.opExtrude","SWEPT_FACE",FACE,{"disambiguationData":[OSD([sQuery(id+"F0.wireOp",EDGE,"E26")])]});
            extrude(context, id + "F13", {"entities" : qUnion([Q0, Q1, Q2, Q3, Q4, Q5]), "operationType" : NewBodyOperationType.REMOVE, "endBound" : BoundingType.UP_TO_SURFACE, "oppositeDirection" : true, "endBoundEntityFace" : qUnion([Q6]), "depth" : 25.4 * mm});
        }
        {
            var Q0;
            {var subQ5=sQuery(id+"F5.wireOp",EDGE,"E41.sketch_text.stroke-6");Q0=makeQuery(id+"F5.imprint","IMPRINT",FACE,{"disambiguationData":[TD([[makeQuery(id+"F5.imprint","IMPRINT",EDGE,{"derivedFrom":subQ5}),-1.0]])]});}
            var Q1;
            {var subQ5=sQuery(id+"F5.wireOp",EDGE,"E41.sketch_text.stroke-15");Q1=makeQuery(id+"F5.imprint","IMPRINT",FACE,{"disambiguationData":[TD([[makeQuery(id+"F5.imprint","IMPRINT",EDGE,{"derivedFrom":subQ5}),-1.0]])]});}
            var Q2;
            {var subQ6=sQuery(id+"F5.wireOp",EDGE,"E41.sketch_text.stroke-31");Q2=makeQuery(id+"F5.imprint","IMPRINT",FACE,{"disambiguationData":[TD([[makeQuery(id+"F5.imprint","IMPRINT",EDGE,{"derivedFrom":subQ6}),-1.0]])]});}
            var Q3;
            {var subQ6=sQuery(id+"F5.wireOp",EDGE,"E41.sketch_text.stroke-41");Q3=makeQuery(id+"F5.imprint","IMPRINT",FACE,{"disambiguationData":[TD([[makeQuery(id+"F5.imprint","IMPRINT",EDGE,{"derivedFrom":subQ6}),-1.0]])]});}
            var Q4;
            {var subQ5=sQuery(id+"F5.wireOp",EDGE,"E41.sketch_text.stroke-56");Q4=makeQuery(id+"F5.imprint","IMPRINT",FACE,{"disambiguationData":[TD([[makeQuery(id+"F5.imprint","IMPRINT",EDGE,{"derivedFrom":subQ5}),-1.0]])]});}
            var Q5;
            {var subQ5=sQuery(id+"F5.wireOp",EDGE,"E41.sketch_text.stroke-71");Q5=makeQuery(id+"F5.imprint","IMPRINT",FACE,{"disambiguationData":[TD([[makeQuery(id+"F5.imprint","IMPRINT",EDGE,{"derivedFrom":subQ5}),-1.0]])]});}
            var Q6;
            {var subQ5=sQuery(id+"F5.wireOp",EDGE,"E41.sketch_text.stroke-81");Q6=makeQuery(id+"F5.imprint","IMPRINT",FACE,{"disambiguationData":[TD([[makeQuery(id+"F5.imprint","IMPRINT",EDGE,{"derivedFrom":subQ5}),-1.0]])]});}
            var Q7;
            Q7=makeQuery(id+"F2.opExtrude","SWEPT_FACE",FACE,{"disambiguationData":[OSD([sQuery(id+"F0.wireOp",EDGE,"E24")])]});
            extrude(context, id + "F14", {"entities" : qUnion([Q0, Q1, Q2, Q3, Q4, Q5, Q6]), "operationType" : NewBodyOperationType.REMOVE, "endBound" : BoundingType.UP_TO_SURFACE, "oppositeDirection" : true, "endBoundEntityFace" : qUnion([Q7]), "depth" : 25.4 * mm});
        }
        {
            var Q0;
            Q0=qCreatedBy(id+"F4.planeOp",FACE);
            var sketch = newSketch(context, id + "F15", { "sketchPlane" : qUnion([Q0])});
            skText(sketch, "E50", { "text": "Dirty", "fontName": "OpenSans-Regular.ttf"});
            skLineSegment(sketch, "E51", {"start": v(86.73, -19.76) * mm, "end": v(18.24, -19.76) * mm});
            skLineSegment(sketch, "E52", {"start": v(30.02, -16.16) * mm, "end": v(94.1, -16.16) * mm});
            skLineSegment(sketch, "E53", {"start": v(95.54, -12.57) * mm, "end": v(5.7, -12.57) * mm});
            skLineSegment(sketch, "E54", {"start": v(4.68, -8.98) * mm, "end": v(93.6, -8.98) * mm});
            skLineSegment(sketch, "E55", {"start": v(93.93, -5.39) * mm, "end": v(3.92, -5.39) * mm});
            skLineSegment(sketch, "E56", {"start": v(4.68, -1.8) * mm, "end": v(94.01, -1.8) * mm});
            skLineSegment(sketch, "E57", {"start": v(93.93, 1.8) * mm, "end": v(4.51, 1.8) * mm});
            skLineSegment(sketch, "E58", {"start": v(4.68, 5.39) * mm, "end": v(93.42, 5.39) * mm});
            skLineSegment(sketch, "E59", {"start": v(93.25, 8.98) * mm, "end": v(1.3, 8.98) * mm});
            const initialGuessF15  = {"E50": [0.00845, -0.01396, 1, 0, 0.02566]};
            skSetInitialGuess(sketch, initialGuessF15);
            skSolve(sketch);
        }
        {
            var Q0;
            {var subQ6=sQuery(id+"F15.wireOp",EDGE,"E50.sketch_text.stroke-67");Q0=makeQuery(id+"F15.imprint","IMPRINT",FACE,{"disambiguationData":[TD([[makeQuery(id+"F15.imprint","IMPRINT",EDGE,{"derivedFrom":subQ6}),-1.0]])]});}
            var Q1;
            Q1=makeQuery(id+"F2.opExtrude","SWEPT_FACE",FACE,{"disambiguationData":[OSD([sQuery(id+"F0.wireOp",EDGE,"E40")])]});
            extrude(context, id + "F16", {"entities" : qUnion([Q0]), "operationType" : NewBodyOperationType.REMOVE, "endBound" : BoundingType.UP_TO_SURFACE, "oppositeDirection" : true, "endBoundEntityFace" : qUnion([Q1]), "depth" : 25.4 * mm});
        }
        {
            var Q0;
            {var subQ3=sQuery(id+"F15.wireOp",EDGE,"E50.sketch_text.stroke-65");var subQ8=sQuery(id+"F15.wireOp",EDGE,"E50.sketch_text.stroke-66");var subQ11=makeQuery(id+"F15.imprint","INTERSECT",VERTEX,{"derivedFrom":[subQ3,subQ8]});Q0=makeQuery(id+"F15.imprint","IMPRINT",FACE,{"disambiguationData":[TD([[makeQuery(id+"F15.imprint","IMPRINT",EDGE,{"disambiguationData":[TD([[subQ11,1.0]])],"derivedFrom":subQ3}),-1.0]])]});}
            var Q1;
            Q1=makeQuery(id+"F2.opExtrude","SWEPT_FACE",FACE,{"disambiguationData":[OSD([sQuery(id+"F0.wireOp",EDGE,"E38")])]});
            extrude(context, id + "F17", {"entities" : qUnion([Q0]), "operationType" : NewBodyOperationType.REMOVE, "endBound" : BoundingType.UP_TO_SURFACE, "oppositeDirection" : true, "endBoundEntityFace" : qUnion([Q1]), "depth" : 25.4 * mm});
        }
        {
            var Q0;
            {var subQ0=sQuery(id+"F15.wireOp",EDGE,"E53");var subQ3=sQuery(id+"F15.wireOp",EDGE,"E50.sketch_text.stroke-65");var subQ4=makeQuery(id+"F15.imprint","INTERSECT",VERTEX,{"derivedFrom":[subQ3,subQ0]});Q0=makeQuery(id+"F15.imprint","IMPRINT",FACE,{"disambiguationData":[TD([[makeQuery(id+"F15.imprint","IMPRINT",EDGE,{"disambiguationData":[TD([[subQ4,-1.0]])],"derivedFrom":subQ3}),-1.0]])]});}
            var Q1;
            {var subQ4=sQuery(id+"F15.wireOp",EDGE,"E50.sketch_text.stroke-42");Q1=makeQuery(id+"F15.imprint","IMPRINT",FACE,{"disambiguationData":[TD([[makeQuery(id+"F15.imprint","IMPRINT",EDGE,{"derivedFrom":subQ4}),-1.0]])]});}
            var Q2;
            {var subQ5=sQuery(id+"F15.wireOp",EDGE,"E50.sketch_text.stroke-32");Q2=makeQuery(id+"F15.imprint","IMPRINT",FACE,{"disambiguationData":[TD([[makeQuery(id+"F15.imprint","IMPRINT",EDGE,{"derivedFrom":subQ5}),-1.0]])]});}
            var Q3;
            {var subQ5=sQuery(id+"F15.wireOp",EDGE,"E50.sketch_text.stroke-14");Q3=makeQuery(id+"F15.imprint","IMPRINT",FACE,{"disambiguationData":[TD([[makeQuery(id+"F15.imprint","IMPRINT",EDGE,{"derivedFrom":subQ5}),-1.0]])]});}
            var Q4;
            {var subQ5=sQuery(id+"F15.wireOp",EDGE,"E50.sketch_text.stroke-2");Q4=makeQuery(id+"F15.imprint","IMPRINT",FACE,{"disambiguationData":[TD([[makeQuery(id+"F15.imprint","IMPRINT",EDGE,{"derivedFrom":subQ5}),-1.0]])]});}
            var Q5;
            Q5=makeQuery(id+"F2.opExtrude","SWEPT_FACE",FACE,{"disambiguationData":[OSD([sQuery(id+"F0.wireOp",EDGE,"E35")])]});
            extrude(context, id + "F18", {"entities" : qUnion([Q0, Q1, Q2, Q3, Q4]), "operationType" : NewBodyOperationType.REMOVE, "endBound" : BoundingType.UP_TO_SURFACE, "oppositeDirection" : true, "endBoundEntityFace" : qUnion([Q5]), "depth" : 25.4 * mm});
        }
        {
            var Q0;
            {var subQ12=sQuery(id+"F15.wireOp",EDGE,"E50.sketch_text.stroke-61");Q0=makeQuery(id+"F15.imprint","IMPRINT",FACE,{"disambiguationData":[TD([[makeQuery(id+"F15.imprint","IMPRINT",EDGE,{"derivedFrom":subQ12}),-1.0]])]});}
            var Q1;
            Q1=makeQuery(id+"F15.imprint","IMPRINT",FACE,{"disambiguationData":[TD([[makeQuery(id+"F15.imprint","IMPRINT",EDGE,{"derivedFrom":sQuery(id+"F15.wireOp",EDGE,"E50.sketch_text.stroke-39")}),-1.0]])]});
            var Q2;
            {var subQ3=sQuery(id+"F15.wireOp",EDGE,"E50.sketch_text.stroke-31");var subQ5=sQuery(id+"F15.wireOp",EDGE,"E53");var subQ7=makeQuery(id+"F15.imprint","INTERSECT",VERTEX,{"derivedFrom":[subQ3,subQ5]});Q2=makeQuery(id+"F15.imprint","IMPRINT",FACE,{"disambiguationData":[TD([[makeQuery(id+"F15.imprint","IMPRINT",EDGE,{"disambiguationData":[TD([[subQ7,1.0]])],"derivedFrom":subQ3}),-1.0]])]});}
            var Q3;
            {var subQ0=sQuery(id+"F15.wireOp",EDGE,"E53");var subQ3=sQuery(id+"F15.wireOp",EDGE,"E50.sketch_text.stroke-15");var subQ4=makeQuery(id+"F15.imprint","INTERSECT",VERTEX,{"derivedFrom":[subQ3,subQ0]});Q3=makeQuery(id+"F15.imprint","IMPRINT",FACE,{"disambiguationData":[TD([[makeQuery(id+"F15.imprint","IMPRINT",EDGE,{"disambiguationData":[TD([[subQ4,-1.0]])],"derivedFrom":subQ3}),-1.0]])]});}
            var Q4;
            {var subQ9=sQuery(id+"F15.wireOp",EDGE,"E50.sketch_text.stroke-11");Q4=makeQuery(id+"F15.imprint","IMPRINT",FACE,{"disambiguationData":[TD([[makeQuery(id+"F15.imprint","IMPRINT",EDGE,{"derivedFrom":subQ9}),-1.0]])]});}
            var Q5;
            Q5=makeQuery(id+"F2.opExtrude","SWEPT_FACE",FACE,{"disambiguationData":[OSD([sQuery(id+"F0.wireOp",EDGE,"E33")])]});
            extrude(context, id + "F19", {"entities" : qUnion([Q0, Q1, Q2, Q3, Q4]), "operationType" : NewBodyOperationType.REMOVE, "endBound" : BoundingType.UP_TO_SURFACE, "oppositeDirection" : true, "endBoundEntityFace" : qUnion([Q5]), "depth" : 25.4 * mm});
        }
        {
            var Q0;
            {var subQ1=sQuery(id+"F15.wireOp",EDGE,"E50.sketch_text.stroke-63");var subQ6=sQuery(id+"F15.wireOp",EDGE,"E50.sketch_text.stroke-62");var subQ9=makeQuery(id+"F15.imprint","INTERSECT",VERTEX,{"derivedFrom":[subQ6,subQ1]});Q0=makeQuery(id+"F15.imprint","IMPRINT",FACE,{"disambiguationData":[TD([[makeQuery(id+"F15.imprint","IMPRINT",EDGE,{"disambiguationData":[TD([[subQ9,1.0]])],"derivedFrom":subQ6}),-1.0]])]});}
            var Q1;
            {var subQ3=sQuery(id+"F15.wireOp",EDGE,"E50.sketch_text.stroke-59");var subQ7=sQuery(id+"F15.wireOp",EDGE,"E50.sketch_text.stroke-60");var subQ9=makeQuery(id+"F15.imprint","INTERSECT",VERTEX,{"derivedFrom":[subQ3,subQ7]});Q1=makeQuery(id+"F15.imprint","IMPRINT",FACE,{"disambiguationData":[TD([[makeQuery(id+"F15.imprint","IMPRINT",EDGE,{"disambiguationData":[TD([[subQ9,1.0]])],"derivedFrom":subQ3}),-1.0]])]});}
            var Q2;
            {var subQ3=sQuery(id+"F15.wireOp",EDGE,"E50.sketch_text.stroke-45");var subQ8=sQuery(id+"F15.wireOp",EDGE,"E50.sketch_text.stroke-44");var subQ11=makeQuery(id+"F15.imprint","INTERSECT",VERTEX,{"derivedFrom":[subQ8,subQ3]});Q2=makeQuery(id+"F15.imprint","IMPRINT",FACE,{"disambiguationData":[TD([[makeQuery(id+"F15.imprint","IMPRINT",EDGE,{"disambiguationData":[TD([[subQ11,1.0]])],"derivedFrom":subQ8}),-1.0]])]});}
            var Q3;
            {var subQ0=sQuery(id+"F15.wireOp",EDGE,"E55");var subQ3=sQuery(id+"F15.wireOp",EDGE,"E50.sketch_text.stroke-31");var subQ4=makeQuery(id+"F15.imprint","INTERSECT",VERTEX,{"derivedFrom":[subQ3,subQ0]});Q3=makeQuery(id+"F15.imprint","IMPRINT",FACE,{"disambiguationData":[TD([[makeQuery(id+"F15.imprint","IMPRINT",EDGE,{"disambiguationData":[TD([[subQ4,-1.0]])],"derivedFrom":subQ3}),-1.0]])]});}
            var Q4;
            {var subQ3=sQuery(id+"F15.wireOp",EDGE,"E50.sketch_text.stroke-15");var subQ5=sQuery(id+"F15.wireOp",EDGE,"E54");var subQ7=makeQuery(id+"F15.imprint","INTERSECT",VERTEX,{"derivedFrom":[subQ3,subQ5]});Q4=makeQuery(id+"F15.imprint","IMPRINT",FACE,{"disambiguationData":[TD([[makeQuery(id+"F15.imprint","IMPRINT",EDGE,{"disambiguationData":[TD([[subQ7,-1.0]])],"derivedFrom":subQ3}),-1.0]])]});}
            var Q5;
            {var subQ0=sQuery(id+"F15.wireOp",EDGE,"E55");var subQ3=sQuery(id+"F15.wireOp",EDGE,"E50.sketch_text.stroke-0");var subQ4=makeQuery(id+"F15.imprint","INTERSECT",VERTEX,{"derivedFrom":[subQ3,subQ0]});Q5=makeQuery(id+"F15.imprint","IMPRINT",FACE,{"disambiguationData":[TD([[makeQuery(id+"F15.imprint","IMPRINT",EDGE,{"disambiguationData":[TD([[subQ4,-1.0]])],"derivedFrom":subQ3}),-1.0]])]});}
            var Q6;
            {var subQ3=sQuery(id+"F15.wireOp",EDGE,"E50.sketch_text.stroke-3");var subQ5=sQuery(id+"F15.wireOp",EDGE,"E54");var subQ7=makeQuery(id+"F15.imprint","INTERSECT",VERTEX,{"derivedFrom":[subQ3,subQ5]});Q6=makeQuery(id+"F15.imprint","IMPRINT",FACE,{"disambiguationData":[TD([[makeQuery(id+"F15.imprint","IMPRINT",EDGE,{"disambiguationData":[TD([[subQ7,-1.0]])],"derivedFrom":subQ3}),-1.0]])]});}
            var Q7;
            Q7=makeQuery(id+"F2.opExtrude","SWEPT_FACE",FACE,{"disambiguationData":[OSD([sQuery(id+"F0.wireOp",EDGE,"E32")])]});
            extrude(context, id + "F20", {"entities" : qUnion([Q0, Q1, Q2, Q3, Q4, Q5, Q6]), "operationType" : NewBodyOperationType.REMOVE, "endBound" : BoundingType.UP_TO_SURFACE, "oppositeDirection" : true, "endBoundEntityFace" : qUnion([Q7]), "depth" : 25.4 * mm});
        }
        {
            var Q0;
            {var subQ3=sQuery(id+"F15.wireOp",EDGE,"E50.sketch_text.stroke-3");var subQ5=sQuery(id+"F15.wireOp",EDGE,"E55");var subQ7=makeQuery(id+"F15.imprint","INTERSECT",VERTEX,{"derivedFrom":[subQ3,subQ5]});Q0=makeQuery(id+"F15.imprint","IMPRINT",FACE,{"disambiguationData":[TD([[makeQuery(id+"F15.imprint","IMPRINT",EDGE,{"disambiguationData":[TD([[subQ7,-1.0]])],"derivedFrom":subQ3}),-1.0]])]});}
            var Q1;
            {var subQ0=sQuery(id+"F15.wireOp",EDGE,"E56");var subQ3=sQuery(id+"F15.wireOp",EDGE,"E50.sketch_text.stroke-0");var subQ4=makeQuery(id+"F15.imprint","INTERSECT",VERTEX,{"derivedFrom":[subQ3,subQ0]});Q1=makeQuery(id+"F15.imprint","IMPRINT",FACE,{"disambiguationData":[TD([[makeQuery(id+"F15.imprint","IMPRINT",EDGE,{"disambiguationData":[TD([[subQ4,-1.0]])],"derivedFrom":subQ3}),-1.0]])]});}
            var Q2;
            {var subQ3=sQuery(id+"F15.wireOp",EDGE,"E50.sketch_text.stroke-15");var subQ5=sQuery(id+"F15.wireOp",EDGE,"E55");var subQ7=makeQuery(id+"F15.imprint","INTERSECT",VERTEX,{"derivedFrom":[subQ3,subQ5]});Q2=makeQuery(id+"F15.imprint","IMPRINT",FACE,{"disambiguationData":[TD([[makeQuery(id+"F15.imprint","IMPRINT",EDGE,{"disambiguationData":[TD([[subQ7,-1.0]])],"derivedFrom":subQ3}),-1.0]])]});}
            var Q3;
            {var subQ3=sQuery(id+"F15.wireOp",EDGE,"E50.sketch_text.stroke-30");var subQ7=sQuery(id+"F15.wireOp",EDGE,"E50.sketch_text.stroke-31");var subQ9=makeQuery(id+"F15.imprint","INTERSECT",VERTEX,{"derivedFrom":[subQ3,subQ7]});Q3=makeQuery(id+"F15.imprint","IMPRINT",FACE,{"disambiguationData":[TD([[makeQuery(id+"F15.imprint","IMPRINT",EDGE,{"disambiguationData":[TD([[subQ9,1.0]])],"derivedFrom":subQ3}),-1.0]])]});}
            var Q4;
            {var subQ3=sQuery(id+"F15.wireOp",EDGE,"E50.sketch_text.stroke-45");var subQ5=sQuery(id+"F15.wireOp",EDGE,"E55");var subQ7=makeQuery(id+"F15.imprint","INTERSECT",VERTEX,{"derivedFrom":[subQ3,subQ5]});Q4=makeQuery(id+"F15.imprint","IMPRINT",FACE,{"disambiguationData":[TD([[makeQuery(id+"F15.imprint","IMPRINT",EDGE,{"disambiguationData":[TD([[subQ7,-1.0]])],"derivedFrom":subQ3}),-1.0]])]});}
            var Q5;
            {var subQ0=sQuery(id+"F15.wireOp",EDGE,"E56");var subQ3=sQuery(id+"F15.wireOp",EDGE,"E50.sketch_text.stroke-59");var subQ4=makeQuery(id+"F15.imprint","INTERSECT",VERTEX,{"derivedFrom":[subQ3,subQ0]});Q5=makeQuery(id+"F15.imprint","IMPRINT",FACE,{"disambiguationData":[TD([[makeQuery(id+"F15.imprint","IMPRINT",EDGE,{"disambiguationData":[TD([[subQ4,-1.0]])],"derivedFrom":subQ3}),-1.0]])]});}
            var Q6;
            {var subQ1=sQuery(id+"F15.wireOp",EDGE,"E50.sketch_text.stroke-63");var subQ5=sQuery(id+"F15.wireOp",EDGE,"E55");var subQ6=makeQuery(id+"F15.imprint","INTERSECT",VERTEX,{"derivedFrom":[subQ1,subQ5]});Q6=makeQuery(id+"F15.imprint","IMPRINT",FACE,{"disambiguationData":[TD([[makeQuery(id+"F15.imprint","IMPRINT",EDGE,{"disambiguationData":[TD([[subQ6,-1.0]])],"derivedFrom":subQ1}),-1.0]])]});}
            var Q7;
            Q7=makeQuery(id+"F2.opExtrude","SWEPT_FACE",FACE,{"disambiguationData":[OSD([sQuery(id+"F0.wireOp",EDGE,"E29")])]});
            extrude(context, id + "F21", {"entities" : qUnion([Q0, Q1, Q2, Q3, Q4, Q5, Q6]), "operationType" : NewBodyOperationType.REMOVE, "endBound" : BoundingType.UP_TO_SURFACE, "oppositeDirection" : true, "endBoundEntityFace" : qUnion([Q7]), "depth" : 25.4 * mm});
        }
        {
            var Q0;
            {var subQ3=sQuery(id+"F15.wireOp",EDGE,"E50.sketch_text.stroke-3");var subQ5=sQuery(id+"F15.wireOp",EDGE,"E56");var subQ7=makeQuery(id+"F15.imprint","INTERSECT",VERTEX,{"derivedFrom":[subQ3,subQ5]});Q0=makeQuery(id+"F15.imprint","IMPRINT",FACE,{"disambiguationData":[TD([[makeQuery(id+"F15.imprint","IMPRINT",EDGE,{"disambiguationData":[TD([[subQ7,-1.0]])],"derivedFrom":subQ3}),-1.0]])]});}
            var Q1;
            {var subQ3=sQuery(id+"F15.wireOp",EDGE,"E50.sketch_text.stroke-0");var subQ9=sQuery(id+"F15.wireOp",EDGE,"E50.sketch_text.stroke-6");var subQ11=makeQuery(id+"F15.imprint","INTERSECT",VERTEX,{"derivedFrom":[subQ3,subQ9]});Q1=makeQuery(id+"F15.imprint","IMPRINT",FACE,{"disambiguationData":[TD([[makeQuery(id+"F15.imprint","IMPRINT",EDGE,{"disambiguationData":[TD([[subQ11,-1.0]])],"derivedFrom":subQ3}),-1.0]])]});}
            var Q2;
            {var subQ0=sQuery(id+"F15.wireOp",EDGE,"E56");var subQ3=sQuery(id+"F15.wireOp",EDGE,"E50.sketch_text.stroke-15");var subQ4=makeQuery(id+"F15.imprint","INTERSECT",VERTEX,{"derivedFrom":[subQ3,subQ0]});Q2=makeQuery(id+"F15.imprint","IMPRINT",FACE,{"disambiguationData":[TD([[makeQuery(id+"F15.imprint","IMPRINT",EDGE,{"disambiguationData":[TD([[subQ4,-1.0]])],"derivedFrom":subQ3}),-1.0]])]});}
            var Q3;
            {var subQ13=sQuery(id+"F15.wireOp",EDGE,"E50.sketch_text.stroke-36");Q3=makeQuery(id+"F15.imprint","IMPRINT",FACE,{"disambiguationData":[TD([[makeQuery(id+"F15.imprint","IMPRINT",EDGE,{"derivedFrom":subQ13}),-1.0]])]});}
            var Q4;
            {var subQ1=sQuery(id+"F15.wireOp",EDGE,"E50.sketch_text.stroke-45");var subQ5=sQuery(id+"F15.wireOp",EDGE,"E56");var subQ7=makeQuery(id+"F15.imprint","INTERSECT",VERTEX,{"derivedFrom":[subQ1,subQ5]});Q4=makeQuery(id+"F15.imprint","IMPRINT",FACE,{"disambiguationData":[TD([[makeQuery(id+"F15.imprint","IMPRINT",EDGE,{"disambiguationData":[TD([[subQ7,-1.0]])],"derivedFrom":subQ1}),-1.0]])]});}
            var Q5;
            {var subQ0=sQuery(id+"F15.wireOp",EDGE,"E57");var subQ3=sQuery(id+"F15.wireOp",EDGE,"E50.sketch_text.stroke-59");var subQ4=makeQuery(id+"F15.imprint","INTERSECT",VERTEX,{"derivedFrom":[subQ3,subQ0]});Q5=makeQuery(id+"F15.imprint","IMPRINT",FACE,{"disambiguationData":[TD([[makeQuery(id+"F15.imprint","IMPRINT",EDGE,{"disambiguationData":[TD([[subQ4,-1.0]])],"derivedFrom":subQ3}),-1.0]])]});}
            var Q6;
            {var subQ0=sQuery(id+"F15.wireOp",EDGE,"E57");var subQ1=sQuery(id+"F15.wireOp",EDGE,"E50.sketch_text.stroke-63");var subQ2=makeQuery(id+"F15.imprint","INTERSECT",VERTEX,{"derivedFrom":[subQ1,subQ0]});Q6=makeQuery(id+"F15.imprint","IMPRINT",FACE,{"disambiguationData":[TD([[makeQuery(id+"F15.imprint","IMPRINT",EDGE,{"disambiguationData":[TD([[subQ2,1.0]])],"derivedFrom":subQ1}),-1.0]])]});}
            var Q7;
            Q7=makeQuery(id+"F2.opExtrude","SWEPT_FACE",FACE,{"disambiguationData":[OSD([sQuery(id+"F0.wireOp",EDGE,"E27")])]});
            extrude(context, id + "F22", {"entities" : qUnion([Q0, Q1, Q2, Q3, Q4, Q5, Q6]), "operationType" : NewBodyOperationType.REMOVE, "endBound" : BoundingType.UP_TO_SURFACE, "oppositeDirection" : true, "endBoundEntityFace" : qUnion([Q7]), "depth" : 25.4 * mm});
        }
        {
            var Q0;
            {var subQ0=sQuery(id+"F15.wireOp",EDGE,"E57");var subQ3=sQuery(id+"F15.wireOp",EDGE,"E50.sketch_text.stroke-3");var subQ4=makeQuery(id+"F15.imprint","INTERSECT",VERTEX,{"derivedFrom":[subQ3,subQ0]});Q0=makeQuery(id+"F15.imprint","IMPRINT",FACE,{"disambiguationData":[TD([[makeQuery(id+"F15.imprint","IMPRINT",EDGE,{"disambiguationData":[TD([[subQ4,-1.0]])],"derivedFrom":subQ3}),-1.0]])]});}
            var Q1;
            {var subQ0=sQuery(id+"F15.wireOp",EDGE,"E58");var subQ3=sQuery(id+"F15.wireOp",EDGE,"E50.sketch_text.stroke-6");var subQ4=makeQuery(id+"F15.imprint","INTERSECT",VERTEX,{"derivedFrom":[subQ3,subQ0]});Q1=makeQuery(id+"F15.imprint","IMPRINT",FACE,{"disambiguationData":[TD([[makeQuery(id+"F15.imprint","IMPRINT",EDGE,{"disambiguationData":[TD([[subQ4,-1.0]])],"derivedFrom":subQ3}),-1.0]])]});}
            var Q2;
            {var subQ3=sQuery(id+"F15.wireOp",EDGE,"E50.sketch_text.stroke-16");Q2=makeQuery(id+"F15.imprint","IMPRINT",FACE,{"disambiguationData":[TD([[makeQuery(id+"F15.imprint","IMPRINT",EDGE,{"derivedFrom":subQ3}),-1.0]])]});}
            var Q3;
            {var subQ3=sQuery(id+"F15.wireOp",EDGE,"E50.sketch_text.stroke-34");Q3=makeQuery(id+"F15.imprint","IMPRINT",FACE,{"disambiguationData":[TD([[makeQuery(id+"F15.imprint","IMPRINT",EDGE,{"derivedFrom":subQ3}),-1.0]])]});}
            var Q4;
            {var subQ12=sQuery(id+"F15.wireOp",EDGE,"E50.sketch_text.stroke-27");Q4=makeQuery(id+"F15.imprint","IMPRINT",FACE,{"disambiguationData":[TD([[makeQuery(id+"F15.imprint","IMPRINT",EDGE,{"derivedFrom":subQ12}),-1.0]])]});}
            var Q5;
            {var subQ13=sQuery(id+"F15.wireOp",EDGE,"E50.sketch_text.stroke-46");Q5=makeQuery(id+"F15.imprint","IMPRINT",FACE,{"disambiguationData":[TD([[makeQuery(id+"F15.imprint","IMPRINT",EDGE,{"derivedFrom":subQ13}),-1.0]])]});}
            var Q6;
            {var subQ3=sQuery(id+"F15.wireOp",EDGE,"E50.sketch_text.stroke-58");Q6=makeQuery(id+"F15.imprint","IMPRINT",FACE,{"disambiguationData":[TD([[makeQuery(id+"F15.imprint","IMPRINT",EDGE,{"derivedFrom":subQ3}),-1.0]])]});}
            var Q7;
            {var subQ5=sQuery(id+"F15.wireOp",EDGE,"E50.sketch_text.stroke-64");Q7=makeQuery(id+"F15.imprint","IMPRINT",FACE,{"disambiguationData":[TD([[makeQuery(id+"F15.imprint","IMPRINT",EDGE,{"derivedFrom":subQ5}),-1.0]])]});}
            var Q8;
            Q8=makeQuery(id+"F2.opExtrude","SWEPT_FACE",FACE,{"disambiguationData":[OSD([sQuery(id+"F0.wireOp",EDGE,"E25")])]});
            extrude(context, id + "F23", {"entities" : qUnion([Q0, Q1, Q2, Q3, Q4, Q5, Q6, Q7]), "operationType" : NewBodyOperationType.REMOVE, "endBound" : BoundingType.UP_TO_SURFACE, "oppositeDirection" : true, "endBoundEntityFace" : qUnion([Q8]), "depth" : 25.4 * mm});
        }
        {
            var Q0;
            {var subQ14=sQuery(id+"F15.wireOp",EDGE,"E50.sketch_text.stroke-8");Q0=makeQuery(id+"F15.imprint","IMPRINT",FACE,{"disambiguationData":[TD([[makeQuery(id+"F15.imprint","IMPRINT",EDGE,{"derivedFrom":subQ14}),-1.0]])]});}
            var Q1;
            {var subQ6=sQuery(id+"F15.wireOp",EDGE,"E50.sketch_text.stroke-23");Q1=makeQuery(id+"F15.imprint","IMPRINT",FACE,{"disambiguationData":[TD([[makeQuery(id+"F15.imprint","IMPRINT",EDGE,{"derivedFrom":subQ6}),-1.0]])]});}
            var Q2;
            {var subQ1=sQuery(id+"F15.wireOp",EDGE,"E50.sketch_text.stroke-49");var subQ6=sQuery(id+"F15.wireOp",EDGE,"E50.sketch_text.stroke-48");var subQ9=makeQuery(id+"F15.imprint","INTERSECT",VERTEX,{"derivedFrom":[subQ6,subQ1]});Q2=makeQuery(id+"F15.imprint","IMPRINT",FACE,{"disambiguationData":[TD([[makeQuery(id+"F15.imprint","IMPRINT",EDGE,{"disambiguationData":[TD([[subQ9,1.0]])],"derivedFrom":subQ6}),-1.0]])]});}
            var Q3;
            Q3=makeQuery(id+"F2.opExtrude","SWEPT_FACE",FACE,{"disambiguationData":[OSD([sQuery(id+"F0.wireOp",EDGE,"E23")])]});
            extrude(context, id + "F24", {"entities" : qUnion([Q0, Q1, Q2]), "operationType" : NewBodyOperationType.REMOVE, "endBound" : BoundingType.UP_TO_SURFACE, "oppositeDirection" : true, "endBoundEntityFace" : qUnion([Q3]), "depth" : 25.4 * mm});
        }
        {
            var Q0;
            {var subQ5=sQuery(id+"F15.wireOp",EDGE,"E50.sketch_text.stroke-4");Q0=makeQuery(id+"F15.imprint","IMPRINT",FACE,{"disambiguationData":[TD([[makeQuery(id+"F15.imprint","IMPRINT",EDGE,{"derivedFrom":subQ5}),-1.0]])]});}
            var Q1;
            {var subQ6=sQuery(id+"F15.wireOp",EDGE,"E50.sketch_text.stroke-18");Q1=makeQuery(id+"F15.imprint","IMPRINT",FACE,{"disambiguationData":[TD([[makeQuery(id+"F15.imprint","IMPRINT",EDGE,{"derivedFrom":subQ6}),-1.0]])]});}
            var Q2;
            {var subQ5=sQuery(id+"F15.wireOp",EDGE,"E50.sketch_text.stroke-50");Q2=makeQuery(id+"F15.imprint","IMPRINT",FACE,{"disambiguationData":[TD([[makeQuery(id+"F15.imprint","IMPRINT",EDGE,{"derivedFrom":subQ5}),-1.0]])]});}
            var Q3;
            Q3=makeQuery(id+"F2.opExtrude","SWEPT_FACE",FACE,{"disambiguationData":[OSD([sQuery(id+"F0.wireOp",EDGE,"E21")])]});
            extrude(context, id + "F25", {"entities" : qUnion([Q0, Q1, Q2]), "operationType" : NewBodyOperationType.REMOVE, "endBound" : BoundingType.UP_TO_SURFACE, "oppositeDirection" : true, "endBoundEntityFace" : qUnion([Q3]), "depth" : 25.4 * mm});
        }
        {
            var Q0;
            Q0=qCreatedBy(makeId("Top.planeOp"),FACE);
            var sketch = newSketch(context, id + "F26", { "sketchPlane" : qUnion([Q0])});
            skLineSegment(sketch, "E60.bottom", {"start": v(24.13, -101.6) * mm, "end": v(-13.97, -101.6) * mm});
            skLineSegment(sketch, "E60.top", {"start": v(24.13, 0) * mm, "end": v(-13.97, 0) * mm});
            skLineSegment(sketch, "E60.left", {"start": v(30.48, -95.25) * mm, "end": v(30.48, -6.35) * mm});
            skLineSegment(sketch, "E60.right", {"start": v(-20.32, -95.25) * mm, "end": v(-20.32, -6.35) * mm});
            skPoint(sketch, "E61.visualSharp", {"position": v(-20.32, -101.6) * mm});
            skArc(sketch, "E61.filletArc", {"start": v(-20.32, -95.25) * mm, "mid": v(-18.46, -99.74) * mm, "end": v(-13.97, -101.6) * mm});
            skPoint(sketch, "E62.visualSharp", {"position": v(30.48, -101.6) * mm});
            skArc(sketch, "E62.filletArc", {"start": v(24.13, -101.6) * mm, "mid": v(28.62, -99.74) * mm, "end": v(30.48, -95.25) * mm});
            skPoint(sketch, "E63.visualSharp", {"position": v(30.48, 0) * mm});
            skArc(sketch, "E63.filletArc", {"start": v(30.48, -6.35) * mm, "mid": v(28.62, -1.86) * mm, "end": v(24.13, 0) * mm});
            skPoint(sketch, "E64.visualSharp", {"position": v(-20.32, 0) * mm});
            skArc(sketch, "E64.filletArc", {"start": v(-13.97, 0) * mm, "mid": v(-18.46, -1.86) * mm, "end": v(-20.32, -6.35) * mm});
            skLineSegment(sketch, "E65.bottom", {"start": v(32.03, -103.63) * mm, "end": v(-22.04, -103.63) * mm});
            skLineSegment(sketch, "E65.top", {"start": v(32.03, 1.1) * mm, "end": v(-22.04, 1.1) * mm});
            skLineSegment(sketch, "E65.left", {"start": v(32.03, -103.63) * mm, "end": v(32.03, 1.1) * mm});
            skLineSegment(sketch, "E65.right", {"start": v(-22.04, -103.63) * mm, "end": v(-22.04, 1.1) * mm});
            skSolve(sketch);
        }
        {
            var Q0;
            Q0=makeQuery(id+"F26.imprint","IMPRINT",FACE,{"disambiguationData":[TD([[makeQuery(id+"F26.imprint","IMPRINT",EDGE,{"derivedFrom":sQuery(id+"F26.wireOp",EDGE,"E60.bottom")}),1.0]])]});
            extrude(context, id + "F27", {"entities" : qUnion([Q0]), "operationType" : NewBodyOperationType.REMOVE, "endBound" : BoundingType.THROUGH_ALL, "oppositeDirection" : true, "depth" : 25.4 * mm});
        }
        {
            var Q0;
            Q0=makeQuery(id+"F1.opExtrude","SWEPT_EDGE",EDGE,{"disambiguationData":[OSD([sQuery(id+"F0.wireOp",EDGE,"E0.bottom"),sQuery(id+"F0.wireOp",EDGE,"E0.right")])]});
            fillet(context, id + "F28", {"entities" : qUnion([Q0]), "radius" : 1.27 * mm, "tangentPropagation" : true, "allowEdgeOverflow" : false});
        }
        {
            var Q0;
            Q0=makeQuery(id+"F1.opExtrude","SWEPT_BODY",BODY,{"disambiguationData":[OSD([sQuery(id+"F0.wireOp",EDGE,"E0.bottom"),sQuery(id+"F0.wireOp",EDGE,"E0.left"),sQuery(id+"F0.wireOp",EDGE,"E0.right"),sQuery(id+"F0.wireOp",EDGE,"E1"),sQuery(id+"F0.wireOp",EDGE,"E2"),sQuery(id+"F0.wireOp",EDGE,"E3"),sQuery(id+"F0.wireOp",EDGE,"E4"),sQuery(id+"F0.wireOp",EDGE,"E5"),sQuery(id+"F0.wireOp",EDGE,"E6"),sQuery(id+"F0.wireOp",EDGE,"E7"),sQuery(id+"F0.wireOp",EDGE,"E8"),sQuery(id+"F0.wireOp",EDGE,"E9"),sQuery(id+"F0.wireOp",EDGE,"E10"),sQuery(id+"F0.wireOp",EDGE,"E11"),sQuery(id+"F0.wireOp",EDGE,"E12"),sQuery(id+"F0.wireOp",EDGE,"E13"),sQuery(id+"F0.wireOp",EDGE,"E14"),sQuery(id+"F0.wireOp",EDGE,"E15"),sQuery(id+"F0.wireOp",EDGE,"E16"),sQuery(id+"F0.wireOp",EDGE,"E17"),sQuery(id+"F0.wireOp",EDGE,"E18"),sQuery(id+"F0.wireOp",EDGE,"E19"),sQuery(id+"F0.wireOp",EDGE,"E20")])]});
            transform(context, id + "F29", {"entities" : qUnion([Q0]), "transformType" : TransformType.TRANSLATION_3D, "dx" : 0 * mm, "dy" : 0 * mm, "dz" : 0 * mm, "makeCopy" : true});
        }
        {
            var Q0;
            Q0=makeQuery(id+"F1.opExtrude","SWEPT_BODY",BODY,{"disambiguationData":[OSD([sQuery(id+"F0.wireOp",EDGE,"E0.bottom"),sQuery(id+"F0.wireOp",EDGE,"E0.left"),sQuery(id+"F0.wireOp",EDGE,"E0.right"),sQuery(id+"F0.wireOp",EDGE,"E1"),sQuery(id+"F0.wireOp",EDGE,"E2"),sQuery(id+"F0.wireOp",EDGE,"E3"),sQuery(id+"F0.wireOp",EDGE,"E4"),sQuery(id+"F0.wireOp",EDGE,"E5"),sQuery(id+"F0.wireOp",EDGE,"E6"),sQuery(id+"F0.wireOp",EDGE,"E7"),sQuery(id+"F0.wireOp",EDGE,"E8"),sQuery(id+"F0.wireOp",EDGE,"E9"),sQuery(id+"F0.wireOp",EDGE,"E10"),sQuery(id+"F0.wireOp",EDGE,"E11"),sQuery(id+"F0.wireOp",EDGE,"E12"),sQuery(id+"F0.wireOp",EDGE,"E13"),sQuery(id+"F0.wireOp",EDGE,"E14"),sQuery(id+"F0.wireOp",EDGE,"E15"),sQuery(id+"F0.wireOp",EDGE,"E16"),sQuery(id+"F0.wireOp",EDGE,"E17"),sQuery(id+"F0.wireOp",EDGE,"E18"),sQuery(id+"F0.wireOp",EDGE,"E19"),sQuery(id+"F0.wireOp",EDGE,"E20")])]});
            var Q1;
            {var subQ0=sQuery(id+"F0.wireOp",EDGE,"E0.bottom");Q1=makeQuery(id+"F28.opFillet","BLEND_EDGE",EDGE,{"blendedFrom":[makeQuery(id+"F1.opExtrude","SWEPT_EDGE",EDGE,{"disambiguationData":[OSD([subQ0,sQuery(id+"F0.wireOp",EDGE,"E0.right")])]}),makeQuery(id+"F1.opExtrude","SWEPT_FACE",FACE,{"disambiguationData":[OSD([subQ0])]})],"blendedInto":[makeQuery(id+"F1.opExtrude","SWEPT_FACE",FACE,{"disambiguationData":[OSD([subQ0])]})]});}
            var Q2;
            {var subQ0=sQuery(id+"F0.wireOp",EDGE,"E0.bottom");Q2=makeQuery(id+"F28.opFillet","BLEND_EDGE",EDGE,{"blendedFrom":[makeQuery(id+"F1.opExtrude","SWEPT_EDGE",EDGE,{"disambiguationData":[OSD([subQ0,sQuery(id+"F0.wireOp",EDGE,"E0.right")])]}),makeQuery(id+"F1.opExtrude","SWEPT_FACE",FACE,{"disambiguationData":[OSD([subQ0])]})],"blendedInto":[makeQuery(id+"F1.opExtrude","SWEPT_FACE",FACE,{"disambiguationData":[OSD([subQ0])]})]});}
            transform(context, id + "F30", {"entities" : qUnion([Q0]), "transformType" : TransformType.ROTATION, "transformAxis" : qUnion([Q2]), "angle" : 180 * degree, "makeCopy" : false});
        }
        {
            var Q0;
            Q0=makeQuery(id+"F1.opExtrude","SWEPT_BODY",BODY,{"disambiguationData":[OSD([sQuery(id+"F0.wireOp",EDGE,"E0.bottom"),sQuery(id+"F0.wireOp",EDGE,"E0.left"),sQuery(id+"F0.wireOp",EDGE,"E0.right"),sQuery(id+"F0.wireOp",EDGE,"E1"),sQuery(id+"F0.wireOp",EDGE,"E2"),sQuery(id+"F0.wireOp",EDGE,"E3"),sQuery(id+"F0.wireOp",EDGE,"E4"),sQuery(id+"F0.wireOp",EDGE,"E5"),sQuery(id+"F0.wireOp",EDGE,"E6"),sQuery(id+"F0.wireOp",EDGE,"E7"),sQuery(id+"F0.wireOp",EDGE,"E8"),sQuery(id+"F0.wireOp",EDGE,"E9"),sQuery(id+"F0.wireOp",EDGE,"E10"),sQuery(id+"F0.wireOp",EDGE,"E11"),sQuery(id+"F0.wireOp",EDGE,"E12"),sQuery(id+"F0.wireOp",EDGE,"E13"),sQuery(id+"F0.wireOp",EDGE,"E14"),sQuery(id+"F0.wireOp",EDGE,"E15"),sQuery(id+"F0.wireOp",EDGE,"E16"),sQuery(id+"F0.wireOp",EDGE,"E17"),sQuery(id+"F0.wireOp",EDGE,"E18"),sQuery(id+"F0.wireOp",EDGE,"E19"),sQuery(id+"F0.wireOp",EDGE,"E20")])]});
            var Q1;
            Q1=qCreatedBy(makeId("Right.planeOp"),FACE);
            transform(context, id + "F31", {"entities" : qUnion([Q0]), "transformType" : TransformType.TRANSLATION_DISTANCE, "transformDirection" : qUnion([Q1]), "distance" : 53.34 * mm, "oppositeDirection" : true, "makeCopy" : false});
        }
        {
            var Q0;
            Q0=makeQuery(id+"F1.opExtrude","SWEPT_BODY",BODY,{"disambiguationData":[OSD([sQuery(id+"F0.wireOp",EDGE,"E0.bottom"),sQuery(id+"F0.wireOp",EDGE,"E0.left"),sQuery(id+"F0.wireOp",EDGE,"E0.right"),sQuery(id+"F0.wireOp",EDGE,"E1"),sQuery(id+"F0.wireOp",EDGE,"E2"),sQuery(id+"F0.wireOp",EDGE,"E3"),sQuery(id+"F0.wireOp",EDGE,"E4"),sQuery(id+"F0.wireOp",EDGE,"E5"),sQuery(id+"F0.wireOp",EDGE,"E6"),sQuery(id+"F0.wireOp",EDGE,"E7"),sQuery(id+"F0.wireOp",EDGE,"E8"),sQuery(id+"F0.wireOp",EDGE,"E9"),sQuery(id+"F0.wireOp",EDGE,"E10"),sQuery(id+"F0.wireOp",EDGE,"E11"),sQuery(id+"F0.wireOp",EDGE,"E12"),sQuery(id+"F0.wireOp",EDGE,"E13"),sQuery(id+"F0.wireOp",EDGE,"E14"),sQuery(id+"F0.wireOp",EDGE,"E15"),sQuery(id+"F0.wireOp",EDGE,"E16"),sQuery(id+"F0.wireOp",EDGE,"E17"),sQuery(id+"F0.wireOp",EDGE,"E18"),sQuery(id+"F0.wireOp",EDGE,"E19"),sQuery(id+"F0.wireOp",EDGE,"E20")])]});
            var Q1;
            Q1=qCreatedBy(makeId("Front.planeOp"),FACE);
            transform(context, id + "F32", {"entities" : qUnion([Q0]), "transformType" : TransformType.TRANSLATION_DISTANCE, "transformDirection" : qUnion([Q1]), "distance" : 50.8 * mm, "oppositeDirection" : true, "makeCopy" : false});
        }
        {
            var Q0;
            Q0=makeQuery(id+"F1.opExtrude","CAP_FACE",FACE,{"disambiguationData":[OSD([sQuery(id+"F0.wireOp",EDGE,"E0.bottom"),sQuery(id+"F0.wireOp",EDGE,"E0.left"),sQuery(id+"F0.wireOp",EDGE,"E0.right"),sQuery(id+"F0.wireOp",EDGE,"E1"),sQuery(id+"F0.wireOp",EDGE,"E2"),sQuery(id+"F0.wireOp",EDGE,"E3"),sQuery(id+"F0.wireOp",EDGE,"E4"),sQuery(id+"F0.wireOp",EDGE,"E5"),sQuery(id+"F0.wireOp",EDGE,"E6"),sQuery(id+"F0.wireOp",EDGE,"E7"),sQuery(id+"F0.wireOp",EDGE,"E8"),sQuery(id+"F0.wireOp",EDGE,"E9"),sQuery(id+"F0.wireOp",EDGE,"E10"),sQuery(id+"F0.wireOp",EDGE,"E11"),sQuery(id+"F0.wireOp",EDGE,"E12"),sQuery(id+"F0.wireOp",EDGE,"E13"),sQuery(id+"F0.wireOp",EDGE,"E14"),sQuery(id+"F0.wireOp",EDGE,"E15"),sQuery(id+"F0.wireOp",EDGE,"E16"),sQuery(id+"F0.wireOp",EDGE,"E17"),sQuery(id+"F0.wireOp",EDGE,"E18"),sQuery(id+"F0.wireOp",EDGE,"E19"),sQuery(id+"F0.wireOp",EDGE,"E20")])],"isStart":false});
            var sketch = newSketch(context, id + "F33", { "sketchPlane" : qUnion([Q0])});
            skLineSegment(sketch, "E66", {"start": v(-25.4, 1.27) * mm, "end": v(-19.05, 1.27) * mm});
            skLineSegment(sketch, "E67", {"start": v(-19.05, 3.8) * mm, "end": v(-19.05, 1.27) * mm});
            skLineSegment(sketch, "E68", {"start": v(-19.05, 3.8) * mm, "end": v(-20.32, 2.54) * mm});
            skLineSegment(sketch, "E69", {"start": v(-20.32, 2.54) * mm, "end": v(-22.86, 5.08) * mm});
            skLineSegment(sketch, "E70", {"start": v(-22.86, 5.08) * mm, "end": v(-25.4, 2.54) * mm});
            skLineSegment(sketch, "E71", {"start": v(-25.4, 2.54) * mm, "end": v(-25.39, 1.27) * mm});
            skLineSegment(sketch, "E72.MirrorCS", {"start": v(22.86, 5.08) * mm, "end": v(25.4, 2.54) * mm});
            skLineSegment(sketch, "E73.MirrorCS", {"start": v(25.4, 2.54) * mm, "end": v(25.39, 1.27) * mm});
            skLineSegment(sketch, "E74.MirrorCS", {"start": v(20.32, 2.54) * mm, "end": v(22.86, 5.08) * mm});
            skLineSegment(sketch, "E75.MirrorCS", {"start": v(25.4, 1.27) * mm, "end": v(19.05, 1.27) * mm});
            skLineSegment(sketch, "E76.MirrorCS", {"start": v(19.05, 3.8) * mm, "end": v(19.05, 1.27) * mm});
            skLineSegment(sketch, "E77.MirrorCS", {"start": v(19.05, 3.8) * mm, "end": v(20.32, 2.54) * mm});
            skSolve(sketch);
        }
        {
            var Q0;
            {var subQ4=sQuery(id+"F0.wireOp",EDGE,"E4");Q0=makeQuery(id+"F33.imprint","IMPRINT",FACE,{"disambiguationData":[TD([[makeQuery(id+"F33.imprint","IMPRINT",EDGE,{"derivedFrom":makeQuery(id+"F1.opExtrude","CAP_EDGE",EDGE,{"disambiguationData":[OSD([subQ4])],"isStart":false})}),1.0]])]});}
            var Q1;
            {var subQ1=sQuery(id+"F33.wireOp",EDGE,"E67");Q1=makeQuery(id+"F33.imprint","IMPRINT",FACE,{"disambiguationData":[TD([[makeQuery(id+"F33.imprint","IMPRINT",EDGE,{"derivedFrom":subQ1}),-1.0]])]});}
            var Q2;
            Q2=makeQuery(id+"F33.imprint","IMPRINT",FACE,{"disambiguationData":[TD([[makeQuery(id+"F33.imprint","IMPRINT",EDGE,{"derivedFrom":sQuery(id+"F33.wireOp",EDGE,"E72.MirrorCS")}),-1.0]])]});
            extrude(context, id + "F34", {"entities" : qUnion([Q0, Q1, Q2]), "oppositeDirection" : true, "offsetDistance" : 25.4 * mm, "depth" : 101.6 * mm});
        }
        {
            var Q0;
            Q0=makeQuery(id+"F1.opExtrude","SWEPT_BODY",BODY,{"disambiguationData":[OSD([sQuery(id+"F0.wireOp",EDGE,"E0.bottom"),sQuery(id+"F0.wireOp",EDGE,"E0.left"),sQuery(id+"F0.wireOp",EDGE,"E0.right"),sQuery(id+"F0.wireOp",EDGE,"E1"),sQuery(id+"F0.wireOp",EDGE,"E2"),sQuery(id+"F0.wireOp",EDGE,"E3"),sQuery(id+"F0.wireOp",EDGE,"E4"),sQuery(id+"F0.wireOp",EDGE,"E5"),sQuery(id+"F0.wireOp",EDGE,"E6"),sQuery(id+"F0.wireOp",EDGE,"E7"),sQuery(id+"F0.wireOp",EDGE,"E8"),sQuery(id+"F0.wireOp",EDGE,"E9"),sQuery(id+"F0.wireOp",EDGE,"E10"),sQuery(id+"F0.wireOp",EDGE,"E11"),sQuery(id+"F0.wireOp",EDGE,"E12"),sQuery(id+"F0.wireOp",EDGE,"E13"),sQuery(id+"F0.wireOp",EDGE,"E14"),sQuery(id+"F0.wireOp",EDGE,"E15"),sQuery(id+"F0.wireOp",EDGE,"E16"),sQuery(id+"F0.wireOp",EDGE,"E17"),sQuery(id+"F0.wireOp",EDGE,"E18"),sQuery(id+"F0.wireOp",EDGE,"E19"),sQuery(id+"F0.wireOp",EDGE,"E20")])]});
            var Q1;
            Q1=makeQuery(id+"F34.opExtrude","SWEPT_BODY",BODY,{"disambiguationData":[OSD([sQuery(id+"F0.wireOp",EDGE,"E0.bottom"),sQuery(id+"F0.wireOp",EDGE,"E0.left"),sQuery(id+"F0.wireOp",EDGE,"E0.right"),sQuery(id+"F0.wireOp",EDGE,"E1"),sQuery(id+"F0.wireOp",EDGE,"E2"),sQuery(id+"F0.wireOp",EDGE,"E3"),sQuery(id+"F0.wireOp",EDGE,"E4"),sQuery(id+"F0.wireOp",EDGE,"E5"),sQuery(id+"F0.wireOp",EDGE,"E6"),sQuery(id+"F0.wireOp",EDGE,"E7"),sQuery(id+"F0.wireOp",EDGE,"E8"),sQuery(id+"F0.wireOp",EDGE,"E9"),sQuery(id+"F0.wireOp",EDGE,"E10"),sQuery(id+"F0.wireOp",EDGE,"E11"),sQuery(id+"F0.wireOp",EDGE,"E12"),sQuery(id+"F0.wireOp",EDGE,"E13"),sQuery(id+"F0.wireOp",EDGE,"E14"),sQuery(id+"F0.wireOp",EDGE,"E15"),sQuery(id+"F0.wireOp",EDGE,"E16"),sQuery(id+"F0.wireOp",EDGE,"E17"),sQuery(id+"F0.wireOp",EDGE,"E18"),sQuery(id+"F0.wireOp",EDGE,"E19"),sQuery(id+"F0.wireOp",EDGE,"E20"),sQuery(id+"F26.wireOp",EDGE,"E60.bottom"),sQuery(id+"F26.wireOp",EDGE,"E61.filletArc"),sQuery(id+"F26.wireOp",EDGE,"E62.filletArc")])]});
            booleanBodies(context, id + "F35", {"operationType" : BooleanOperationType.SUBTRACTION, "tools" : qUnion([Q0]), "targets" : qUnion([Q1])});
        }
        {
            var Q0;
            Q0=qCreatedBy(makeId("Top.planeOp"),FACE);
            var sketch = newSketch(context, id + "F36", { "sketchPlane" : qUnion([Q0])});
            skLineSegment(sketch, "E78.bottom", {"start": v(-33.56, 54.39) * mm, "end": v(-17.62, 54.39) * mm});
            skLineSegment(sketch, "E78.top", {"start": v(-33.56, 42.71) * mm, "end": v(-17.62, 42.71) * mm});
            skLineSegment(sketch, "E78.left", {"start": v(-33.56, 54.39) * mm, "end": v(-33.56, 42.71) * mm});
            skLineSegment(sketch, "E78.right", {"start": v(-17.62, 54.39) * mm, "end": v(-17.62, 42.71) * mm});
            skLineSegment(sketch, "E79.bottom", {"start": v(-34.58, -44.41) * mm, "end": v(-18.75, -44.41) * mm});
            skLineSegment(sketch, "E79.top", {"start": v(-34.58, -60.73) * mm, "end": v(-18.75, -60.73) * mm});
            skLineSegment(sketch, "E79.left", {"start": v(-34.58, -44.41) * mm, "end": v(-34.58, -60.73) * mm});
            skLineSegment(sketch, "E79.right", {"start": v(-18.75, -44.41) * mm, "end": v(-18.75, -60.73) * mm});
            skLineSegment(sketch, "E80.bottom", {"start": v(-18.75, -44.41) * mm, "end": v(-26.9, -44.41) * mm});
            skLineSegment(sketch, "E80.left", {"start": v(-18.75, -44.41) * mm, "end": v(-18.75, -53.23) * mm});
            skLineSegment(sketch, "E81.bottom", {"start": v(17.8, -43.33) * mm, "end": v(28.09, -43.33) * mm});
            skLineSegment(sketch, "E81.top", {"start": v(17.8, -53.75) * mm, "end": v(28.09, -53.75) * mm});
            skLineSegment(sketch, "E81.left", {"start": v(17.8, -43.33) * mm, "end": v(17.8, -53.75) * mm});
            skLineSegment(sketch, "E81.right", {"start": v(28.09, -43.33) * mm, "end": v(28.09, -53.75) * mm});
            skLineSegment(sketch, "E82.bottom", {"start": v(18.47, 51.9) * mm, "end": v(27.24, 51.9) * mm});
            skLineSegment(sketch, "E82.top", {"start": v(18.47, 43.37) * mm, "end": v(27.24, 43.37) * mm});
            skLineSegment(sketch, "E82.left", {"start": v(18.47, 51.9) * mm, "end": v(18.47, 43.37) * mm});
            skLineSegment(sketch, "E82.right", {"start": v(27.24, 51.9) * mm, "end": v(27.24, 43.37) * mm});
            skSolve(sketch);
        }
        {
            var Q0;
            Q0=makeQuery(id+"F36.imprint","IMPRINT",FACE,{"disambiguationData":[TD([[makeQuery(id+"F36.imprint","IMPRINT",EDGE,{"derivedFrom":sQuery(id+"F36.wireOp",EDGE,"E78.bottom")}),-1.0]])]});
            var Q1;
            Q1=makeQuery(id+"F36.imprint","IMPRINT",FACE,{"disambiguationData":[TD([[makeQuery(id+"F36.imprint","IMPRINT",EDGE,{"derivedFrom":sQuery(id+"F36.wireOp",EDGE,"E82.bottom")}),-1.0]])]});
            var Q2;
            Q2=makeQuery(id+"F36.imprint","IMPRINT",FACE,{"disambiguationData":[TD([[makeQuery(id+"F36.imprint","IMPRINT",EDGE,{"derivedFrom":sQuery(id+"F36.wireOp",EDGE,"E79.bottom")}),-1.0]])]});
            var Q3;
            Q3=makeQuery(id+"F36.imprint","IMPRINT",FACE,{"disambiguationData":[TD([[makeQuery(id+"F36.imprint","IMPRINT",EDGE,{"derivedFrom":sQuery(id+"F36.wireOp",EDGE,"E81.bottom")}),-1.0]])]});
            extrude(context, id + "F37", {"entities" : qUnion([Q0, Q1, Q2, Q3]), "operationType" : NewBodyOperationType.REMOVE, "depth" : 25.4 * mm});
        }
        {
            var Q0;
            Q0=makeQuery(id+"F35.opBoolean","SPLIT",BODY,{"disambiguationData":[OD(0.0)],"derivedFrom":makeQuery(id+"F34.opExtrude","SWEPT_BODY",BODY,{"disambiguationData":[OSD([sQuery(id+"F0.wireOp",EDGE,"E0.bottom"),sQuery(id+"F0.wireOp",EDGE,"E0.left"),sQuery(id+"F0.wireOp",EDGE,"E0.right"),sQuery(id+"F0.wireOp",EDGE,"E1"),sQuery(id+"F0.wireOp",EDGE,"E2"),sQuery(id+"F0.wireOp",EDGE,"E3"),sQuery(id+"F0.wireOp",EDGE,"E4"),sQuery(id+"F0.wireOp",EDGE,"E5"),sQuery(id+"F0.wireOp",EDGE,"E6"),sQuery(id+"F0.wireOp",EDGE,"E7"),sQuery(id+"F0.wireOp",EDGE,"E8"),sQuery(id+"F0.wireOp",EDGE,"E9"),sQuery(id+"F0.wireOp",EDGE,"E10"),sQuery(id+"F0.wireOp",EDGE,"E11"),sQuery(id+"F0.wireOp",EDGE,"E12"),sQuery(id+"F0.wireOp",EDGE,"E13"),sQuery(id+"F0.wireOp",EDGE,"E14"),sQuery(id+"F0.wireOp",EDGE,"E15"),sQuery(id+"F0.wireOp",EDGE,"E16"),sQuery(id+"F0.wireOp",EDGE,"E17"),sQuery(id+"F0.wireOp",EDGE,"E18"),sQuery(id+"F0.wireOp",EDGE,"E19"),sQuery(id+"F0.wireOp",EDGE,"E20"),sQuery(id+"F33.wireOp",EDGE,"E66"),sQuery(id+"F33.wireOp",EDGE,"E68"),sQuery(id+"F33.wireOp",EDGE,"E69"),sQuery(id+"F33.wireOp",EDGE,"E70"),sQuery(id+"F33.wireOp",EDGE,"E71"),sQuery(id+"F33.wireOp",EDGE,"E72.MirrorCS"),sQuery(id+"F33.wireOp",EDGE,"E73.MirrorCS"),sQuery(id+"F33.wireOp",EDGE,"E74.MirrorCS"),sQuery(id+"F33.wireOp",EDGE,"E75.MirrorCS"),sQuery(id+"F33.wireOp",EDGE,"E77.MirrorCS")])]})});
            var Q1;
            Q1=makeQuery(id+"F35.opBoolean","SPLIT",BODY,{"disambiguationData":[OD(1.0)],"derivedFrom":makeQuery(id+"F34.opExtrude","SWEPT_BODY",BODY,{"disambiguationData":[OSD([sQuery(id+"F0.wireOp",EDGE,"E0.bottom"),sQuery(id+"F0.wireOp",EDGE,"E0.left"),sQuery(id+"F0.wireOp",EDGE,"E0.right"),sQuery(id+"F0.wireOp",EDGE,"E1"),sQuery(id+"F0.wireOp",EDGE,"E2"),sQuery(id+"F0.wireOp",EDGE,"E3"),sQuery(id+"F0.wireOp",EDGE,"E4"),sQuery(id+"F0.wireOp",EDGE,"E5"),sQuery(id+"F0.wireOp",EDGE,"E6"),sQuery(id+"F0.wireOp",EDGE,"E7"),sQuery(id+"F0.wireOp",EDGE,"E8"),sQuery(id+"F0.wireOp",EDGE,"E9"),sQuery(id+"F0.wireOp",EDGE,"E10"),sQuery(id+"F0.wireOp",EDGE,"E11"),sQuery(id+"F0.wireOp",EDGE,"E12"),sQuery(id+"F0.wireOp",EDGE,"E13"),sQuery(id+"F0.wireOp",EDGE,"E14"),sQuery(id+"F0.wireOp",EDGE,"E15"),sQuery(id+"F0.wireOp",EDGE,"E16"),sQuery(id+"F0.wireOp",EDGE,"E17"),sQuery(id+"F0.wireOp",EDGE,"E18"),sQuery(id+"F0.wireOp",EDGE,"E19"),sQuery(id+"F0.wireOp",EDGE,"E20"),sQuery(id+"F33.wireOp",EDGE,"E66"),sQuery(id+"F33.wireOp",EDGE,"E68"),sQuery(id+"F33.wireOp",EDGE,"E69"),sQuery(id+"F33.wireOp",EDGE,"E70"),sQuery(id+"F33.wireOp",EDGE,"E71"),sQuery(id+"F33.wireOp",EDGE,"E72.MirrorCS"),sQuery(id+"F33.wireOp",EDGE,"E73.MirrorCS"),sQuery(id+"F33.wireOp",EDGE,"E74.MirrorCS"),sQuery(id+"F33.wireOp",EDGE,"E75.MirrorCS"),sQuery(id+"F33.wireOp",EDGE,"E77.MirrorCS")])]})});
            var Q2;
            Q2=makeQuery(id+"F35.opBoolean","SPLIT",BODY,{"disambiguationData":[OD(2.0)],"derivedFrom":makeQuery(id+"F34.opExtrude","SWEPT_BODY",BODY,{"disambiguationData":[OSD([sQuery(id+"F0.wireOp",EDGE,"E0.bottom"),sQuery(id+"F0.wireOp",EDGE,"E0.left"),sQuery(id+"F0.wireOp",EDGE,"E0.right"),sQuery(id+"F0.wireOp",EDGE,"E1"),sQuery(id+"F0.wireOp",EDGE,"E2"),sQuery(id+"F0.wireOp",EDGE,"E3"),sQuery(id+"F0.wireOp",EDGE,"E4"),sQuery(id+"F0.wireOp",EDGE,"E5"),sQuery(id+"F0.wireOp",EDGE,"E6"),sQuery(id+"F0.wireOp",EDGE,"E7"),sQuery(id+"F0.wireOp",EDGE,"E8"),sQuery(id+"F0.wireOp",EDGE,"E9"),sQuery(id+"F0.wireOp",EDGE,"E10"),sQuery(id+"F0.wireOp",EDGE,"E11"),sQuery(id+"F0.wireOp",EDGE,"E12"),sQuery(id+"F0.wireOp",EDGE,"E13"),sQuery(id+"F0.wireOp",EDGE,"E14"),sQuery(id+"F0.wireOp",EDGE,"E15"),sQuery(id+"F0.wireOp",EDGE,"E16"),sQuery(id+"F0.wireOp",EDGE,"E17"),sQuery(id+"F0.wireOp",EDGE,"E18"),sQuery(id+"F0.wireOp",EDGE,"E19"),sQuery(id+"F0.wireOp",EDGE,"E20"),sQuery(id+"F33.wireOp",EDGE,"E66"),sQuery(id+"F33.wireOp",EDGE,"E68"),sQuery(id+"F33.wireOp",EDGE,"E69"),sQuery(id+"F33.wireOp",EDGE,"E70"),sQuery(id+"F33.wireOp",EDGE,"E71"),sQuery(id+"F33.wireOp",EDGE,"E72.MirrorCS"),sQuery(id+"F33.wireOp",EDGE,"E73.MirrorCS"),sQuery(id+"F33.wireOp",EDGE,"E74.MirrorCS"),sQuery(id+"F33.wireOp",EDGE,"E75.MirrorCS"),sQuery(id+"F33.wireOp",EDGE,"E77.MirrorCS")])]})});
            var Q3;
            Q3=makeQuery(id+"F35.opBoolean","SPLIT",BODY,{"disambiguationData":[OD(3.0)],"derivedFrom":makeQuery(id+"F34.opExtrude","SWEPT_BODY",BODY,{"disambiguationData":[OSD([sQuery(id+"F0.wireOp",EDGE,"E0.bottom"),sQuery(id+"F0.wireOp",EDGE,"E0.left"),sQuery(id+"F0.wireOp",EDGE,"E0.right"),sQuery(id+"F0.wireOp",EDGE,"E1"),sQuery(id+"F0.wireOp",EDGE,"E2"),sQuery(id+"F0.wireOp",EDGE,"E3"),sQuery(id+"F0.wireOp",EDGE,"E4"),sQuery(id+"F0.wireOp",EDGE,"E5"),sQuery(id+"F0.wireOp",EDGE,"E6"),sQuery(id+"F0.wireOp",EDGE,"E7"),sQuery(id+"F0.wireOp",EDGE,"E8"),sQuery(id+"F0.wireOp",EDGE,"E9"),sQuery(id+"F0.wireOp",EDGE,"E10"),sQuery(id+"F0.wireOp",EDGE,"E11"),sQuery(id+"F0.wireOp",EDGE,"E12"),sQuery(id+"F0.wireOp",EDGE,"E13"),sQuery(id+"F0.wireOp",EDGE,"E14"),sQuery(id+"F0.wireOp",EDGE,"E15"),sQuery(id+"F0.wireOp",EDGE,"E16"),sQuery(id+"F0.wireOp",EDGE,"E17"),sQuery(id+"F0.wireOp",EDGE,"E18"),sQuery(id+"F0.wireOp",EDGE,"E19"),sQuery(id+"F0.wireOp",EDGE,"E20"),sQuery(id+"F33.wireOp",EDGE,"E66"),sQuery(id+"F33.wireOp",EDGE,"E68"),sQuery(id+"F33.wireOp",EDGE,"E69"),sQuery(id+"F33.wireOp",EDGE,"E70"),sQuery(id+"F33.wireOp",EDGE,"E71"),sQuery(id+"F33.wireOp",EDGE,"E72.MirrorCS"),sQuery(id+"F33.wireOp",EDGE,"E73.MirrorCS"),sQuery(id+"F33.wireOp",EDGE,"E74.MirrorCS"),sQuery(id+"F33.wireOp",EDGE,"E75.MirrorCS"),sQuery(id+"F33.wireOp",EDGE,"E77.MirrorCS")])]})});
            var Q4;
            Q4=makeQuery(id+"F35.opBoolean","SPLIT",BODY,{"disambiguationData":[OD(4.0)],"derivedFrom":makeQuery(id+"F34.opExtrude","SWEPT_BODY",BODY,{"disambiguationData":[OSD([sQuery(id+"F0.wireOp",EDGE,"E0.bottom"),sQuery(id+"F0.wireOp",EDGE,"E0.left"),sQuery(id+"F0.wireOp",EDGE,"E0.right"),sQuery(id+"F0.wireOp",EDGE,"E1"),sQuery(id+"F0.wireOp",EDGE,"E2"),sQuery(id+"F0.wireOp",EDGE,"E3"),sQuery(id+"F0.wireOp",EDGE,"E4"),sQuery(id+"F0.wireOp",EDGE,"E5"),sQuery(id+"F0.wireOp",EDGE,"E6"),sQuery(id+"F0.wireOp",EDGE,"E7"),sQuery(id+"F0.wireOp",EDGE,"E8"),sQuery(id+"F0.wireOp",EDGE,"E9"),sQuery(id+"F0.wireOp",EDGE,"E10"),sQuery(id+"F0.wireOp",EDGE,"E11"),sQuery(id+"F0.wireOp",EDGE,"E12"),sQuery(id+"F0.wireOp",EDGE,"E13"),sQuery(id+"F0.wireOp",EDGE,"E14"),sQuery(id+"F0.wireOp",EDGE,"E15"),sQuery(id+"F0.wireOp",EDGE,"E16"),sQuery(id+"F0.wireOp",EDGE,"E17"),sQuery(id+"F0.wireOp",EDGE,"E18"),sQuery(id+"F0.wireOp",EDGE,"E19"),sQuery(id+"F0.wireOp",EDGE,"E20"),sQuery(id+"F33.wireOp",EDGE,"E66"),sQuery(id+"F33.wireOp",EDGE,"E68"),sQuery(id+"F33.wireOp",EDGE,"E69"),sQuery(id+"F33.wireOp",EDGE,"E70"),sQuery(id+"F33.wireOp",EDGE,"E71"),sQuery(id+"F33.wireOp",EDGE,"E72.MirrorCS"),sQuery(id+"F33.wireOp",EDGE,"E73.MirrorCS"),sQuery(id+"F33.wireOp",EDGE,"E74.MirrorCS"),sQuery(id+"F33.wireOp",EDGE,"E75.MirrorCS"),sQuery(id+"F33.wireOp",EDGE,"E77.MirrorCS")])]})});
            var Q5;
            Q5=makeQuery(id+"F35.opBoolean","SPLIT",BODY,{"disambiguationData":[OD(5.0)],"derivedFrom":makeQuery(id+"F34.opExtrude","SWEPT_BODY",BODY,{"disambiguationData":[OSD([sQuery(id+"F0.wireOp",EDGE,"E0.bottom"),sQuery(id+"F0.wireOp",EDGE,"E0.left"),sQuery(id+"F0.wireOp",EDGE,"E0.right"),sQuery(id+"F0.wireOp",EDGE,"E1"),sQuery(id+"F0.wireOp",EDGE,"E2"),sQuery(id+"F0.wireOp",EDGE,"E3"),sQuery(id+"F0.wireOp",EDGE,"E4"),sQuery(id+"F0.wireOp",EDGE,"E5"),sQuery(id+"F0.wireOp",EDGE,"E6"),sQuery(id+"F0.wireOp",EDGE,"E7"),sQuery(id+"F0.wireOp",EDGE,"E8"),sQuery(id+"F0.wireOp",EDGE,"E9"),sQuery(id+"F0.wireOp",EDGE,"E10"),sQuery(id+"F0.wireOp",EDGE,"E11"),sQuery(id+"F0.wireOp",EDGE,"E12"),sQuery(id+"F0.wireOp",EDGE,"E13"),sQuery(id+"F0.wireOp",EDGE,"E14"),sQuery(id+"F0.wireOp",EDGE,"E15"),sQuery(id+"F0.wireOp",EDGE,"E16"),sQuery(id+"F0.wireOp",EDGE,"E17"),sQuery(id+"F0.wireOp",EDGE,"E18"),sQuery(id+"F0.wireOp",EDGE,"E19"),sQuery(id+"F0.wireOp",EDGE,"E20"),sQuery(id+"F33.wireOp",EDGE,"E66"),sQuery(id+"F33.wireOp",EDGE,"E68"),sQuery(id+"F33.wireOp",EDGE,"E69"),sQuery(id+"F33.wireOp",EDGE,"E70"),sQuery(id+"F33.wireOp",EDGE,"E71"),sQuery(id+"F33.wireOp",EDGE,"E72.MirrorCS"),sQuery(id+"F33.wireOp",EDGE,"E73.MirrorCS"),sQuery(id+"F33.wireOp",EDGE,"E74.MirrorCS"),sQuery(id+"F33.wireOp",EDGE,"E75.MirrorCS"),sQuery(id+"F33.wireOp",EDGE,"E77.MirrorCS")])]})});
            var Q6;
            Q6=makeQuery(id+"F35.opBoolean","SPLIT",BODY,{"disambiguationData":[OD(6.0)],"derivedFrom":makeQuery(id+"F34.opExtrude","SWEPT_BODY",BODY,{"disambiguationData":[OSD([sQuery(id+"F0.wireOp",EDGE,"E0.bottom"),sQuery(id+"F0.wireOp",EDGE,"E0.left"),sQuery(id+"F0.wireOp",EDGE,"E0.right"),sQuery(id+"F0.wireOp",EDGE,"E1"),sQuery(id+"F0.wireOp",EDGE,"E2"),sQuery(id+"F0.wireOp",EDGE,"E3"),sQuery(id+"F0.wireOp",EDGE,"E4"),sQuery(id+"F0.wireOp",EDGE,"E5"),sQuery(id+"F0.wireOp",EDGE,"E6"),sQuery(id+"F0.wireOp",EDGE,"E7"),sQuery(id+"F0.wireOp",EDGE,"E8"),sQuery(id+"F0.wireOp",EDGE,"E9"),sQuery(id+"F0.wireOp",EDGE,"E10"),sQuery(id+"F0.wireOp",EDGE,"E11"),sQuery(id+"F0.wireOp",EDGE,"E12"),sQuery(id+"F0.wireOp",EDGE,"E13"),sQuery(id+"F0.wireOp",EDGE,"E14"),sQuery(id+"F0.wireOp",EDGE,"E15"),sQuery(id+"F0.wireOp",EDGE,"E16"),sQuery(id+"F0.wireOp",EDGE,"E17"),sQuery(id+"F0.wireOp",EDGE,"E18"),sQuery(id+"F0.wireOp",EDGE,"E19"),sQuery(id+"F0.wireOp",EDGE,"E20"),sQuery(id+"F33.wireOp",EDGE,"E66"),sQuery(id+"F33.wireOp",EDGE,"E68"),sQuery(id+"F33.wireOp",EDGE,"E69"),sQuery(id+"F33.wireOp",EDGE,"E70"),sQuery(id+"F33.wireOp",EDGE,"E71"),sQuery(id+"F33.wireOp",EDGE,"E72.MirrorCS"),sQuery(id+"F33.wireOp",EDGE,"E73.MirrorCS"),sQuery(id+"F33.wireOp",EDGE,"E74.MirrorCS"),sQuery(id+"F33.wireOp",EDGE,"E75.MirrorCS"),sQuery(id+"F33.wireOp",EDGE,"E77.MirrorCS")])]})});
            var Q7;
            Q7=makeQuery(id+"F35.opBoolean","SPLIT",BODY,{"disambiguationData":[OD(7.0)],"derivedFrom":makeQuery(id+"F34.opExtrude","SWEPT_BODY",BODY,{"disambiguationData":[OSD([sQuery(id+"F0.wireOp",EDGE,"E0.bottom"),sQuery(id+"F0.wireOp",EDGE,"E0.left"),sQuery(id+"F0.wireOp",EDGE,"E0.right"),sQuery(id+"F0.wireOp",EDGE,"E1"),sQuery(id+"F0.wireOp",EDGE,"E2"),sQuery(id+"F0.wireOp",EDGE,"E3"),sQuery(id+"F0.wireOp",EDGE,"E4"),sQuery(id+"F0.wireOp",EDGE,"E5"),sQuery(id+"F0.wireOp",EDGE,"E6"),sQuery(id+"F0.wireOp",EDGE,"E7"),sQuery(id+"F0.wireOp",EDGE,"E8"),sQuery(id+"F0.wireOp",EDGE,"E9"),sQuery(id+"F0.wireOp",EDGE,"E10"),sQuery(id+"F0.wireOp",EDGE,"E11"),sQuery(id+"F0.wireOp",EDGE,"E12"),sQuery(id+"F0.wireOp",EDGE,"E13"),sQuery(id+"F0.wireOp",EDGE,"E14"),sQuery(id+"F0.wireOp",EDGE,"E15"),sQuery(id+"F0.wireOp",EDGE,"E16"),sQuery(id+"F0.wireOp",EDGE,"E17"),sQuery(id+"F0.wireOp",EDGE,"E18"),sQuery(id+"F0.wireOp",EDGE,"E19"),sQuery(id+"F0.wireOp",EDGE,"E20"),sQuery(id+"F33.wireOp",EDGE,"E66"),sQuery(id+"F33.wireOp",EDGE,"E68"),sQuery(id+"F33.wireOp",EDGE,"E69"),sQuery(id+"F33.wireOp",EDGE,"E70"),sQuery(id+"F33.wireOp",EDGE,"E71"),sQuery(id+"F33.wireOp",EDGE,"E72.MirrorCS"),sQuery(id+"F33.wireOp",EDGE,"E73.MirrorCS"),sQuery(id+"F33.wireOp",EDGE,"E74.MirrorCS"),sQuery(id+"F33.wireOp",EDGE,"E75.MirrorCS"),sQuery(id+"F33.wireOp",EDGE,"E77.MirrorCS")])]})});
            var Q8;
            Q8=makeQuery(id+"F35.opBoolean","SPLIT",BODY,{"disambiguationData":[OD(8.0)],"derivedFrom":makeQuery(id+"F34.opExtrude","SWEPT_BODY",BODY,{"disambiguationData":[OSD([sQuery(id+"F0.wireOp",EDGE,"E0.bottom"),sQuery(id+"F0.wireOp",EDGE,"E0.left"),sQuery(id+"F0.wireOp",EDGE,"E0.right"),sQuery(id+"F0.wireOp",EDGE,"E1"),sQuery(id+"F0.wireOp",EDGE,"E2"),sQuery(id+"F0.wireOp",EDGE,"E3"),sQuery(id+"F0.wireOp",EDGE,"E4"),sQuery(id+"F0.wireOp",EDGE,"E5"),sQuery(id+"F0.wireOp",EDGE,"E6"),sQuery(id+"F0.wireOp",EDGE,"E7"),sQuery(id+"F0.wireOp",EDGE,"E8"),sQuery(id+"F0.wireOp",EDGE,"E9"),sQuery(id+"F0.wireOp",EDGE,"E10"),sQuery(id+"F0.wireOp",EDGE,"E11"),sQuery(id+"F0.wireOp",EDGE,"E12"),sQuery(id+"F0.wireOp",EDGE,"E13"),sQuery(id+"F0.wireOp",EDGE,"E14"),sQuery(id+"F0.wireOp",EDGE,"E15"),sQuery(id+"F0.wireOp",EDGE,"E16"),sQuery(id+"F0.wireOp",EDGE,"E17"),sQuery(id+"F0.wireOp",EDGE,"E18"),sQuery(id+"F0.wireOp",EDGE,"E19"),sQuery(id+"F0.wireOp",EDGE,"E20"),sQuery(id+"F33.wireOp",EDGE,"E66"),sQuery(id+"F33.wireOp",EDGE,"E68"),sQuery(id+"F33.wireOp",EDGE,"E69"),sQuery(id+"F33.wireOp",EDGE,"E70"),sQuery(id+"F33.wireOp",EDGE,"E71"),sQuery(id+"F33.wireOp",EDGE,"E72.MirrorCS"),sQuery(id+"F33.wireOp",EDGE,"E73.MirrorCS"),sQuery(id+"F33.wireOp",EDGE,"E74.MirrorCS"),sQuery(id+"F33.wireOp",EDGE,"E75.MirrorCS"),sQuery(id+"F33.wireOp",EDGE,"E77.MirrorCS")])]})});
            var Q9;
            Q9=makeQuery(id+"F35.opBoolean","SPLIT",BODY,{"disambiguationData":[OD(9.0)],"derivedFrom":makeQuery(id+"F34.opExtrude","SWEPT_BODY",BODY,{"disambiguationData":[OSD([sQuery(id+"F0.wireOp",EDGE,"E0.bottom"),sQuery(id+"F0.wireOp",EDGE,"E0.left"),sQuery(id+"F0.wireOp",EDGE,"E0.right"),sQuery(id+"F0.wireOp",EDGE,"E1"),sQuery(id+"F0.wireOp",EDGE,"E2"),sQuery(id+"F0.wireOp",EDGE,"E3"),sQuery(id+"F0.wireOp",EDGE,"E4"),sQuery(id+"F0.wireOp",EDGE,"E5"),sQuery(id+"F0.wireOp",EDGE,"E6"),sQuery(id+"F0.wireOp",EDGE,"E7"),sQuery(id+"F0.wireOp",EDGE,"E8"),sQuery(id+"F0.wireOp",EDGE,"E9"),sQuery(id+"F0.wireOp",EDGE,"E10"),sQuery(id+"F0.wireOp",EDGE,"E11"),sQuery(id+"F0.wireOp",EDGE,"E12"),sQuery(id+"F0.wireOp",EDGE,"E13"),sQuery(id+"F0.wireOp",EDGE,"E14"),sQuery(id+"F0.wireOp",EDGE,"E15"),sQuery(id+"F0.wireOp",EDGE,"E16"),sQuery(id+"F0.wireOp",EDGE,"E17"),sQuery(id+"F0.wireOp",EDGE,"E18"),sQuery(id+"F0.wireOp",EDGE,"E19"),sQuery(id+"F0.wireOp",EDGE,"E20"),sQuery(id+"F33.wireOp",EDGE,"E66"),sQuery(id+"F33.wireOp",EDGE,"E68"),sQuery(id+"F33.wireOp",EDGE,"E69"),sQuery(id+"F33.wireOp",EDGE,"E70"),sQuery(id+"F33.wireOp",EDGE,"E71"),sQuery(id+"F33.wireOp",EDGE,"E72.MirrorCS"),sQuery(id+"F33.wireOp",EDGE,"E73.MirrorCS"),sQuery(id+"F33.wireOp",EDGE,"E74.MirrorCS"),sQuery(id+"F33.wireOp",EDGE,"E75.MirrorCS"),sQuery(id+"F33.wireOp",EDGE,"E77.MirrorCS")])]})});
            var Q10;
            Q10=makeQuery(id+"F35.opBoolean","SPLIT",BODY,{"disambiguationData":[OD(10.0)],"derivedFrom":makeQuery(id+"F34.opExtrude","SWEPT_BODY",BODY,{"disambiguationData":[OSD([sQuery(id+"F0.wireOp",EDGE,"E0.bottom"),sQuery(id+"F0.wireOp",EDGE,"E0.left"),sQuery(id+"F0.wireOp",EDGE,"E0.right"),sQuery(id+"F0.wireOp",EDGE,"E1"),sQuery(id+"F0.wireOp",EDGE,"E2"),sQuery(id+"F0.wireOp",EDGE,"E3"),sQuery(id+"F0.wireOp",EDGE,"E4"),sQuery(id+"F0.wireOp",EDGE,"E5"),sQuery(id+"F0.wireOp",EDGE,"E6"),sQuery(id+"F0.wireOp",EDGE,"E7"),sQuery(id+"F0.wireOp",EDGE,"E8"),sQuery(id+"F0.wireOp",EDGE,"E9"),sQuery(id+"F0.wireOp",EDGE,"E10"),sQuery(id+"F0.wireOp",EDGE,"E11"),sQuery(id+"F0.wireOp",EDGE,"E12"),sQuery(id+"F0.wireOp",EDGE,"E13"),sQuery(id+"F0.wireOp",EDGE,"E14"),sQuery(id+"F0.wireOp",EDGE,"E15"),sQuery(id+"F0.wireOp",EDGE,"E16"),sQuery(id+"F0.wireOp",EDGE,"E17"),sQuery(id+"F0.wireOp",EDGE,"E18"),sQuery(id+"F0.wireOp",EDGE,"E19"),sQuery(id+"F0.wireOp",EDGE,"E20"),sQuery(id+"F33.wireOp",EDGE,"E66"),sQuery(id+"F33.wireOp",EDGE,"E68"),sQuery(id+"F33.wireOp",EDGE,"E69"),sQuery(id+"F33.wireOp",EDGE,"E70"),sQuery(id+"F33.wireOp",EDGE,"E71"),sQuery(id+"F33.wireOp",EDGE,"E72.MirrorCS"),sQuery(id+"F33.wireOp",EDGE,"E73.MirrorCS"),sQuery(id+"F33.wireOp",EDGE,"E74.MirrorCS"),sQuery(id+"F33.wireOp",EDGE,"E75.MirrorCS"),sQuery(id+"F33.wireOp",EDGE,"E77.MirrorCS")])]})});
            var Q11;
            Q11=makeQuery(id+"F35.opBoolean","SPLIT",BODY,{"disambiguationData":[OD(11.0)],"derivedFrom":makeQuery(id+"F34.opExtrude","SWEPT_BODY",BODY,{"disambiguationData":[OSD([sQuery(id+"F0.wireOp",EDGE,"E0.bottom"),sQuery(id+"F0.wireOp",EDGE,"E0.left"),sQuery(id+"F0.wireOp",EDGE,"E0.right"),sQuery(id+"F0.wireOp",EDGE,"E1"),sQuery(id+"F0.wireOp",EDGE,"E2"),sQuery(id+"F0.wireOp",EDGE,"E3"),sQuery(id+"F0.wireOp",EDGE,"E4"),sQuery(id+"F0.wireOp",EDGE,"E5"),sQuery(id+"F0.wireOp",EDGE,"E6"),sQuery(id+"F0.wireOp",EDGE,"E7"),sQuery(id+"F0.wireOp",EDGE,"E8"),sQuery(id+"F0.wireOp",EDGE,"E9"),sQuery(id+"F0.wireOp",EDGE,"E10"),sQuery(id+"F0.wireOp",EDGE,"E11"),sQuery(id+"F0.wireOp",EDGE,"E12"),sQuery(id+"F0.wireOp",EDGE,"E13"),sQuery(id+"F0.wireOp",EDGE,"E14"),sQuery(id+"F0.wireOp",EDGE,"E15"),sQuery(id+"F0.wireOp",EDGE,"E16"),sQuery(id+"F0.wireOp",EDGE,"E17"),sQuery(id+"F0.wireOp",EDGE,"E18"),sQuery(id+"F0.wireOp",EDGE,"E19"),sQuery(id+"F0.wireOp",EDGE,"E20"),sQuery(id+"F33.wireOp",EDGE,"E66"),sQuery(id+"F33.wireOp",EDGE,"E68"),sQuery(id+"F33.wireOp",EDGE,"E69"),sQuery(id+"F33.wireOp",EDGE,"E70"),sQuery(id+"F33.wireOp",EDGE,"E71"),sQuery(id+"F33.wireOp",EDGE,"E72.MirrorCS"),sQuery(id+"F33.wireOp",EDGE,"E73.MirrorCS"),sQuery(id+"F33.wireOp",EDGE,"E74.MirrorCS"),sQuery(id+"F33.wireOp",EDGE,"E75.MirrorCS"),sQuery(id+"F33.wireOp",EDGE,"E77.MirrorCS")])]})});
            var Q12;
            Q12=makeQuery(id+"F35.opBoolean","SPLIT",BODY,{"disambiguationData":[OD(12.0)],"derivedFrom":makeQuery(id+"F34.opExtrude","SWEPT_BODY",BODY,{"disambiguationData":[OSD([sQuery(id+"F0.wireOp",EDGE,"E0.bottom"),sQuery(id+"F0.wireOp",EDGE,"E0.left"),sQuery(id+"F0.wireOp",EDGE,"E0.right"),sQuery(id+"F0.wireOp",EDGE,"E1"),sQuery(id+"F0.wireOp",EDGE,"E2"),sQuery(id+"F0.wireOp",EDGE,"E3"),sQuery(id+"F0.wireOp",EDGE,"E4"),sQuery(id+"F0.wireOp",EDGE,"E5"),sQuery(id+"F0.wireOp",EDGE,"E6"),sQuery(id+"F0.wireOp",EDGE,"E7"),sQuery(id+"F0.wireOp",EDGE,"E8"),sQuery(id+"F0.wireOp",EDGE,"E9"),sQuery(id+"F0.wireOp",EDGE,"E10"),sQuery(id+"F0.wireOp",EDGE,"E11"),sQuery(id+"F0.wireOp",EDGE,"E12"),sQuery(id+"F0.wireOp",EDGE,"E13"),sQuery(id+"F0.wireOp",EDGE,"E14"),sQuery(id+"F0.wireOp",EDGE,"E15"),sQuery(id+"F0.wireOp",EDGE,"E16"),sQuery(id+"F0.wireOp",EDGE,"E17"),sQuery(id+"F0.wireOp",EDGE,"E18"),sQuery(id+"F0.wireOp",EDGE,"E19"),sQuery(id+"F0.wireOp",EDGE,"E20"),sQuery(id+"F33.wireOp",EDGE,"E66"),sQuery(id+"F33.wireOp",EDGE,"E68"),sQuery(id+"F33.wireOp",EDGE,"E69"),sQuery(id+"F33.wireOp",EDGE,"E70"),sQuery(id+"F33.wireOp",EDGE,"E71"),sQuery(id+"F33.wireOp",EDGE,"E72.MirrorCS"),sQuery(id+"F33.wireOp",EDGE,"E73.MirrorCS"),sQuery(id+"F33.wireOp",EDGE,"E74.MirrorCS"),sQuery(id+"F33.wireOp",EDGE,"E75.MirrorCS"),sQuery(id+"F33.wireOp",EDGE,"E77.MirrorCS")])]})});
            var Q13;
            Q13=makeQuery(id+"F35.opBoolean","SPLIT",BODY,{"disambiguationData":[OD(13.0)],"derivedFrom":makeQuery(id+"F34.opExtrude","SWEPT_BODY",BODY,{"disambiguationData":[OSD([sQuery(id+"F0.wireOp",EDGE,"E0.bottom"),sQuery(id+"F0.wireOp",EDGE,"E0.left"),sQuery(id+"F0.wireOp",EDGE,"E0.right"),sQuery(id+"F0.wireOp",EDGE,"E1"),sQuery(id+"F0.wireOp",EDGE,"E2"),sQuery(id+"F0.wireOp",EDGE,"E3"),sQuery(id+"F0.wireOp",EDGE,"E4"),sQuery(id+"F0.wireOp",EDGE,"E5"),sQuery(id+"F0.wireOp",EDGE,"E6"),sQuery(id+"F0.wireOp",EDGE,"E7"),sQuery(id+"F0.wireOp",EDGE,"E8"),sQuery(id+"F0.wireOp",EDGE,"E9"),sQuery(id+"F0.wireOp",EDGE,"E10"),sQuery(id+"F0.wireOp",EDGE,"E11"),sQuery(id+"F0.wireOp",EDGE,"E12"),sQuery(id+"F0.wireOp",EDGE,"E13"),sQuery(id+"F0.wireOp",EDGE,"E14"),sQuery(id+"F0.wireOp",EDGE,"E15"),sQuery(id+"F0.wireOp",EDGE,"E16"),sQuery(id+"F0.wireOp",EDGE,"E17"),sQuery(id+"F0.wireOp",EDGE,"E18"),sQuery(id+"F0.wireOp",EDGE,"E19"),sQuery(id+"F0.wireOp",EDGE,"E20"),sQuery(id+"F33.wireOp",EDGE,"E66"),sQuery(id+"F33.wireOp",EDGE,"E68"),sQuery(id+"F33.wireOp",EDGE,"E69"),sQuery(id+"F33.wireOp",EDGE,"E70"),sQuery(id+"F33.wireOp",EDGE,"E71"),sQuery(id+"F33.wireOp",EDGE,"E72.MirrorCS"),sQuery(id+"F33.wireOp",EDGE,"E73.MirrorCS"),sQuery(id+"F33.wireOp",EDGE,"E74.MirrorCS"),sQuery(id+"F33.wireOp",EDGE,"E75.MirrorCS"),sQuery(id+"F33.wireOp",EDGE,"E77.MirrorCS")])]})});
            var Q14;
            Q14=makeQuery(id+"F35.opBoolean","SPLIT",BODY,{"disambiguationData":[OD(14.0)],"derivedFrom":makeQuery(id+"F34.opExtrude","SWEPT_BODY",BODY,{"disambiguationData":[OSD([sQuery(id+"F0.wireOp",EDGE,"E0.bottom"),sQuery(id+"F0.wireOp",EDGE,"E0.left"),sQuery(id+"F0.wireOp",EDGE,"E0.right"),sQuery(id+"F0.wireOp",EDGE,"E1"),sQuery(id+"F0.wireOp",EDGE,"E2"),sQuery(id+"F0.wireOp",EDGE,"E3"),sQuery(id+"F0.wireOp",EDGE,"E4"),sQuery(id+"F0.wireOp",EDGE,"E5"),sQuery(id+"F0.wireOp",EDGE,"E6"),sQuery(id+"F0.wireOp",EDGE,"E7"),sQuery(id+"F0.wireOp",EDGE,"E8"),sQuery(id+"F0.wireOp",EDGE,"E9"),sQuery(id+"F0.wireOp",EDGE,"E10"),sQuery(id+"F0.wireOp",EDGE,"E11"),sQuery(id+"F0.wireOp",EDGE,"E12"),sQuery(id+"F0.wireOp",EDGE,"E13"),sQuery(id+"F0.wireOp",EDGE,"E14"),sQuery(id+"F0.wireOp",EDGE,"E15"),sQuery(id+"F0.wireOp",EDGE,"E16"),sQuery(id+"F0.wireOp",EDGE,"E17"),sQuery(id+"F0.wireOp",EDGE,"E18"),sQuery(id+"F0.wireOp",EDGE,"E19"),sQuery(id+"F0.wireOp",EDGE,"E20"),sQuery(id+"F33.wireOp",EDGE,"E66"),sQuery(id+"F33.wireOp",EDGE,"E68"),sQuery(id+"F33.wireOp",EDGE,"E69"),sQuery(id+"F33.wireOp",EDGE,"E70"),sQuery(id+"F33.wireOp",EDGE,"E71"),sQuery(id+"F33.wireOp",EDGE,"E72.MirrorCS"),sQuery(id+"F33.wireOp",EDGE,"E73.MirrorCS"),sQuery(id+"F33.wireOp",EDGE,"E74.MirrorCS"),sQuery(id+"F33.wireOp",EDGE,"E75.MirrorCS"),sQuery(id+"F33.wireOp",EDGE,"E77.MirrorCS")])]})});
            var Q15;
            Q15=makeQuery(id+"F35.opBoolean","SPLIT",BODY,{"disambiguationData":[OD(15.0)],"derivedFrom":makeQuery(id+"F34.opExtrude","SWEPT_BODY",BODY,{"disambiguationData":[OSD([sQuery(id+"F0.wireOp",EDGE,"E0.bottom"),sQuery(id+"F0.wireOp",EDGE,"E0.left"),sQuery(id+"F0.wireOp",EDGE,"E0.right"),sQuery(id+"F0.wireOp",EDGE,"E1"),sQuery(id+"F0.wireOp",EDGE,"E2"),sQuery(id+"F0.wireOp",EDGE,"E3"),sQuery(id+"F0.wireOp",EDGE,"E4"),sQuery(id+"F0.wireOp",EDGE,"E5"),sQuery(id+"F0.wireOp",EDGE,"E6"),sQuery(id+"F0.wireOp",EDGE,"E7"),sQuery(id+"F0.wireOp",EDGE,"E8"),sQuery(id+"F0.wireOp",EDGE,"E9"),sQuery(id+"F0.wireOp",EDGE,"E10"),sQuery(id+"F0.wireOp",EDGE,"E11"),sQuery(id+"F0.wireOp",EDGE,"E12"),sQuery(id+"F0.wireOp",EDGE,"E13"),sQuery(id+"F0.wireOp",EDGE,"E14"),sQuery(id+"F0.wireOp",EDGE,"E15"),sQuery(id+"F0.wireOp",EDGE,"E16"),sQuery(id+"F0.wireOp",EDGE,"E17"),sQuery(id+"F0.wireOp",EDGE,"E18"),sQuery(id+"F0.wireOp",EDGE,"E19"),sQuery(id+"F0.wireOp",EDGE,"E20"),sQuery(id+"F33.wireOp",EDGE,"E66"),sQuery(id+"F33.wireOp",EDGE,"E68"),sQuery(id+"F33.wireOp",EDGE,"E69"),sQuery(id+"F33.wireOp",EDGE,"E70"),sQuery(id+"F33.wireOp",EDGE,"E71"),sQuery(id+"F33.wireOp",EDGE,"E72.MirrorCS"),sQuery(id+"F33.wireOp",EDGE,"E73.MirrorCS"),sQuery(id+"F33.wireOp",EDGE,"E74.MirrorCS"),sQuery(id+"F33.wireOp",EDGE,"E75.MirrorCS"),sQuery(id+"F33.wireOp",EDGE,"E77.MirrorCS")])]})});
            var Q16;
            Q16=makeQuery(id+"F35.opBoolean","SPLIT",BODY,{"disambiguationData":[OD(16.0)],"derivedFrom":makeQuery(id+"F34.opExtrude","SWEPT_BODY",BODY,{"disambiguationData":[OSD([sQuery(id+"F0.wireOp",EDGE,"E0.bottom"),sQuery(id+"F0.wireOp",EDGE,"E0.left"),sQuery(id+"F0.wireOp",EDGE,"E0.right"),sQuery(id+"F0.wireOp",EDGE,"E1"),sQuery(id+"F0.wireOp",EDGE,"E2"),sQuery(id+"F0.wireOp",EDGE,"E3"),sQuery(id+"F0.wireOp",EDGE,"E4"),sQuery(id+"F0.wireOp",EDGE,"E5"),sQuery(id+"F0.wireOp",EDGE,"E6"),sQuery(id+"F0.wireOp",EDGE,"E7"),sQuery(id+"F0.wireOp",EDGE,"E8"),sQuery(id+"F0.wireOp",EDGE,"E9"),sQuery(id+"F0.wireOp",EDGE,"E10"),sQuery(id+"F0.wireOp",EDGE,"E11"),sQuery(id+"F0.wireOp",EDGE,"E12"),sQuery(id+"F0.wireOp",EDGE,"E13"),sQuery(id+"F0.wireOp",EDGE,"E14"),sQuery(id+"F0.wireOp",EDGE,"E15"),sQuery(id+"F0.wireOp",EDGE,"E16"),sQuery(id+"F0.wireOp",EDGE,"E17"),sQuery(id+"F0.wireOp",EDGE,"E18"),sQuery(id+"F0.wireOp",EDGE,"E19"),sQuery(id+"F0.wireOp",EDGE,"E20"),sQuery(id+"F33.wireOp",EDGE,"E66"),sQuery(id+"F33.wireOp",EDGE,"E68"),sQuery(id+"F33.wireOp",EDGE,"E69"),sQuery(id+"F33.wireOp",EDGE,"E70"),sQuery(id+"F33.wireOp",EDGE,"E71"),sQuery(id+"F33.wireOp",EDGE,"E72.MirrorCS"),sQuery(id+"F33.wireOp",EDGE,"E73.MirrorCS"),sQuery(id+"F33.wireOp",EDGE,"E74.MirrorCS"),sQuery(id+"F33.wireOp",EDGE,"E75.MirrorCS"),sQuery(id+"F33.wireOp",EDGE,"E77.MirrorCS")])]})});
            var Q17;
            Q17=makeQuery(id+"F35.opBoolean","SPLIT",BODY,{"disambiguationData":[OD(17.0)],"derivedFrom":makeQuery(id+"F34.opExtrude","SWEPT_BODY",BODY,{"disambiguationData":[OSD([sQuery(id+"F0.wireOp",EDGE,"E0.bottom"),sQuery(id+"F0.wireOp",EDGE,"E0.left"),sQuery(id+"F0.wireOp",EDGE,"E0.right"),sQuery(id+"F0.wireOp",EDGE,"E1"),sQuery(id+"F0.wireOp",EDGE,"E2"),sQuery(id+"F0.wireOp",EDGE,"E3"),sQuery(id+"F0.wireOp",EDGE,"E4"),sQuery(id+"F0.wireOp",EDGE,"E5"),sQuery(id+"F0.wireOp",EDGE,"E6"),sQuery(id+"F0.wireOp",EDGE,"E7"),sQuery(id+"F0.wireOp",EDGE,"E8"),sQuery(id+"F0.wireOp",EDGE,"E9"),sQuery(id+"F0.wireOp",EDGE,"E10"),sQuery(id+"F0.wireOp",EDGE,"E11"),sQuery(id+"F0.wireOp",EDGE,"E12"),sQuery(id+"F0.wireOp",EDGE,"E13"),sQuery(id+"F0.wireOp",EDGE,"E14"),sQuery(id+"F0.wireOp",EDGE,"E15"),sQuery(id+"F0.wireOp",EDGE,"E16"),sQuery(id+"F0.wireOp",EDGE,"E17"),sQuery(id+"F0.wireOp",EDGE,"E18"),sQuery(id+"F0.wireOp",EDGE,"E19"),sQuery(id+"F0.wireOp",EDGE,"E20"),sQuery(id+"F33.wireOp",EDGE,"E66"),sQuery(id+"F33.wireOp",EDGE,"E68"),sQuery(id+"F33.wireOp",EDGE,"E69"),sQuery(id+"F33.wireOp",EDGE,"E70"),sQuery(id+"F33.wireOp",EDGE,"E71"),sQuery(id+"F33.wireOp",EDGE,"E72.MirrorCS"),sQuery(id+"F33.wireOp",EDGE,"E73.MirrorCS"),sQuery(id+"F33.wireOp",EDGE,"E74.MirrorCS"),sQuery(id+"F33.wireOp",EDGE,"E75.MirrorCS"),sQuery(id+"F33.wireOp",EDGE,"E77.MirrorCS")])]})});
            var Q18;
            Q18=makeQuery(id+"F35.opBoolean","SPLIT",BODY,{"disambiguationData":[OD(18.0)],"derivedFrom":makeQuery(id+"F34.opExtrude","SWEPT_BODY",BODY,{"disambiguationData":[OSD([sQuery(id+"F0.wireOp",EDGE,"E0.bottom"),sQuery(id+"F0.wireOp",EDGE,"E0.left"),sQuery(id+"F0.wireOp",EDGE,"E0.right"),sQuery(id+"F0.wireOp",EDGE,"E1"),sQuery(id+"F0.wireOp",EDGE,"E2"),sQuery(id+"F0.wireOp",EDGE,"E3"),sQuery(id+"F0.wireOp",EDGE,"E4"),sQuery(id+"F0.wireOp",EDGE,"E5"),sQuery(id+"F0.wireOp",EDGE,"E6"),sQuery(id+"F0.wireOp",EDGE,"E7"),sQuery(id+"F0.wireOp",EDGE,"E8"),sQuery(id+"F0.wireOp",EDGE,"E9"),sQuery(id+"F0.wireOp",EDGE,"E10"),sQuery(id+"F0.wireOp",EDGE,"E11"),sQuery(id+"F0.wireOp",EDGE,"E12"),sQuery(id+"F0.wireOp",EDGE,"E13"),sQuery(id+"F0.wireOp",EDGE,"E14"),sQuery(id+"F0.wireOp",EDGE,"E15"),sQuery(id+"F0.wireOp",EDGE,"E16"),sQuery(id+"F0.wireOp",EDGE,"E17"),sQuery(id+"F0.wireOp",EDGE,"E18"),sQuery(id+"F0.wireOp",EDGE,"E19"),sQuery(id+"F0.wireOp",EDGE,"E20"),sQuery(id+"F33.wireOp",EDGE,"E66"),sQuery(id+"F33.wireOp",EDGE,"E68"),sQuery(id+"F33.wireOp",EDGE,"E69"),sQuery(id+"F33.wireOp",EDGE,"E70"),sQuery(id+"F33.wireOp",EDGE,"E71"),sQuery(id+"F33.wireOp",EDGE,"E72.MirrorCS"),sQuery(id+"F33.wireOp",EDGE,"E73.MirrorCS"),sQuery(id+"F33.wireOp",EDGE,"E74.MirrorCS"),sQuery(id+"F33.wireOp",EDGE,"E75.MirrorCS"),sQuery(id+"F33.wireOp",EDGE,"E77.MirrorCS")])]})});
            var Q19;
            Q19=makeQuery(id+"F35.opBoolean","SPLIT",BODY,{"disambiguationData":[OD(19.0)],"derivedFrom":makeQuery(id+"F34.opExtrude","SWEPT_BODY",BODY,{"disambiguationData":[OSD([sQuery(id+"F0.wireOp",EDGE,"E0.bottom"),sQuery(id+"F0.wireOp",EDGE,"E0.left"),sQuery(id+"F0.wireOp",EDGE,"E0.right"),sQuery(id+"F0.wireOp",EDGE,"E1"),sQuery(id+"F0.wireOp",EDGE,"E2"),sQuery(id+"F0.wireOp",EDGE,"E3"),sQuery(id+"F0.wireOp",EDGE,"E4"),sQuery(id+"F0.wireOp",EDGE,"E5"),sQuery(id+"F0.wireOp",EDGE,"E6"),sQuery(id+"F0.wireOp",EDGE,"E7"),sQuery(id+"F0.wireOp",EDGE,"E8"),sQuery(id+"F0.wireOp",EDGE,"E9"),sQuery(id+"F0.wireOp",EDGE,"E10"),sQuery(id+"F0.wireOp",EDGE,"E11"),sQuery(id+"F0.wireOp",EDGE,"E12"),sQuery(id+"F0.wireOp",EDGE,"E13"),sQuery(id+"F0.wireOp",EDGE,"E14"),sQuery(id+"F0.wireOp",EDGE,"E15"),sQuery(id+"F0.wireOp",EDGE,"E16"),sQuery(id+"F0.wireOp",EDGE,"E17"),sQuery(id+"F0.wireOp",EDGE,"E18"),sQuery(id+"F0.wireOp",EDGE,"E19"),sQuery(id+"F0.wireOp",EDGE,"E20"),sQuery(id+"F33.wireOp",EDGE,"E66"),sQuery(id+"F33.wireOp",EDGE,"E68"),sQuery(id+"F33.wireOp",EDGE,"E69"),sQuery(id+"F33.wireOp",EDGE,"E70"),sQuery(id+"F33.wireOp",EDGE,"E71"),sQuery(id+"F33.wireOp",EDGE,"E72.MirrorCS"),sQuery(id+"F33.wireOp",EDGE,"E73.MirrorCS"),sQuery(id+"F33.wireOp",EDGE,"E74.MirrorCS"),sQuery(id+"F33.wireOp",EDGE,"E75.MirrorCS"),sQuery(id+"F33.wireOp",EDGE,"E77.MirrorCS")])]})});
            var Q20;
            Q20=makeQuery(id+"F35.opBoolean","SPLIT",BODY,{"disambiguationData":[OD(20.0)],"derivedFrom":makeQuery(id+"F34.opExtrude","SWEPT_BODY",BODY,{"disambiguationData":[OSD([sQuery(id+"F0.wireOp",EDGE,"E0.bottom"),sQuery(id+"F0.wireOp",EDGE,"E0.left"),sQuery(id+"F0.wireOp",EDGE,"E0.right"),sQuery(id+"F0.wireOp",EDGE,"E1"),sQuery(id+"F0.wireOp",EDGE,"E2"),sQuery(id+"F0.wireOp",EDGE,"E3"),sQuery(id+"F0.wireOp",EDGE,"E4"),sQuery(id+"F0.wireOp",EDGE,"E5"),sQuery(id+"F0.wireOp",EDGE,"E6"),sQuery(id+"F0.wireOp",EDGE,"E7"),sQuery(id+"F0.wireOp",EDGE,"E8"),sQuery(id+"F0.wireOp",EDGE,"E9"),sQuery(id+"F0.wireOp",EDGE,"E10"),sQuery(id+"F0.wireOp",EDGE,"E11"),sQuery(id+"F0.wireOp",EDGE,"E12"),sQuery(id+"F0.wireOp",EDGE,"E13"),sQuery(id+"F0.wireOp",EDGE,"E14"),sQuery(id+"F0.wireOp",EDGE,"E15"),sQuery(id+"F0.wireOp",EDGE,"E16"),sQuery(id+"F0.wireOp",EDGE,"E17"),sQuery(id+"F0.wireOp",EDGE,"E18"),sQuery(id+"F0.wireOp",EDGE,"E19"),sQuery(id+"F0.wireOp",EDGE,"E20"),sQuery(id+"F33.wireOp",EDGE,"E66"),sQuery(id+"F33.wireOp",EDGE,"E68"),sQuery(id+"F33.wireOp",EDGE,"E69"),sQuery(id+"F33.wireOp",EDGE,"E70"),sQuery(id+"F33.wireOp",EDGE,"E71"),sQuery(id+"F33.wireOp",EDGE,"E72.MirrorCS"),sQuery(id+"F33.wireOp",EDGE,"E73.MirrorCS"),sQuery(id+"F33.wireOp",EDGE,"E74.MirrorCS"),sQuery(id+"F33.wireOp",EDGE,"E75.MirrorCS"),sQuery(id+"F33.wireOp",EDGE,"E77.MirrorCS")])]})});
            var Q21;
            Q21=makeQuery(id+"F35.opBoolean","SPLIT",BODY,{"disambiguationData":[OD(22.0)],"derivedFrom":makeQuery(id+"F34.opExtrude","SWEPT_BODY",BODY,{"disambiguationData":[OSD([sQuery(id+"F0.wireOp",EDGE,"E0.bottom"),sQuery(id+"F0.wireOp",EDGE,"E0.left"),sQuery(id+"F0.wireOp",EDGE,"E0.right"),sQuery(id+"F0.wireOp",EDGE,"E1"),sQuery(id+"F0.wireOp",EDGE,"E2"),sQuery(id+"F0.wireOp",EDGE,"E3"),sQuery(id+"F0.wireOp",EDGE,"E4"),sQuery(id+"F0.wireOp",EDGE,"E5"),sQuery(id+"F0.wireOp",EDGE,"E6"),sQuery(id+"F0.wireOp",EDGE,"E7"),sQuery(id+"F0.wireOp",EDGE,"E8"),sQuery(id+"F0.wireOp",EDGE,"E9"),sQuery(id+"F0.wireOp",EDGE,"E10"),sQuery(id+"F0.wireOp",EDGE,"E11"),sQuery(id+"F0.wireOp",EDGE,"E12"),sQuery(id+"F0.wireOp",EDGE,"E13"),sQuery(id+"F0.wireOp",EDGE,"E14"),sQuery(id+"F0.wireOp",EDGE,"E15"),sQuery(id+"F0.wireOp",EDGE,"E16"),sQuery(id+"F0.wireOp",EDGE,"E17"),sQuery(id+"F0.wireOp",EDGE,"E18"),sQuery(id+"F0.wireOp",EDGE,"E19"),sQuery(id+"F0.wireOp",EDGE,"E20"),sQuery(id+"F33.wireOp",EDGE,"E66"),sQuery(id+"F33.wireOp",EDGE,"E68"),sQuery(id+"F33.wireOp",EDGE,"E69"),sQuery(id+"F33.wireOp",EDGE,"E70"),sQuery(id+"F33.wireOp",EDGE,"E71"),sQuery(id+"F33.wireOp",EDGE,"E72.MirrorCS"),sQuery(id+"F33.wireOp",EDGE,"E73.MirrorCS"),sQuery(id+"F33.wireOp",EDGE,"E74.MirrorCS"),sQuery(id+"F33.wireOp",EDGE,"E75.MirrorCS"),sQuery(id+"F33.wireOp",EDGE,"E77.MirrorCS")])]})});
            var Q22;
            Q22=makeQuery(id+"F35.opBoolean","SPLIT",BODY,{"disambiguationData":[OD(23.0)],"derivedFrom":makeQuery(id+"F34.opExtrude","SWEPT_BODY",BODY,{"disambiguationData":[OSD([sQuery(id+"F0.wireOp",EDGE,"E0.bottom"),sQuery(id+"F0.wireOp",EDGE,"E0.left"),sQuery(id+"F0.wireOp",EDGE,"E0.right"),sQuery(id+"F0.wireOp",EDGE,"E1"),sQuery(id+"F0.wireOp",EDGE,"E2"),sQuery(id+"F0.wireOp",EDGE,"E3"),sQuery(id+"F0.wireOp",EDGE,"E4"),sQuery(id+"F0.wireOp",EDGE,"E5"),sQuery(id+"F0.wireOp",EDGE,"E6"),sQuery(id+"F0.wireOp",EDGE,"E7"),sQuery(id+"F0.wireOp",EDGE,"E8"),sQuery(id+"F0.wireOp",EDGE,"E9"),sQuery(id+"F0.wireOp",EDGE,"E10"),sQuery(id+"F0.wireOp",EDGE,"E11"),sQuery(id+"F0.wireOp",EDGE,"E12"),sQuery(id+"F0.wireOp",EDGE,"E13"),sQuery(id+"F0.wireOp",EDGE,"E14"),sQuery(id+"F0.wireOp",EDGE,"E15"),sQuery(id+"F0.wireOp",EDGE,"E16"),sQuery(id+"F0.wireOp",EDGE,"E17"),sQuery(id+"F0.wireOp",EDGE,"E18"),sQuery(id+"F0.wireOp",EDGE,"E19"),sQuery(id+"F0.wireOp",EDGE,"E20"),sQuery(id+"F33.wireOp",EDGE,"E66"),sQuery(id+"F33.wireOp",EDGE,"E68"),sQuery(id+"F33.wireOp",EDGE,"E69"),sQuery(id+"F33.wireOp",EDGE,"E70"),sQuery(id+"F33.wireOp",EDGE,"E71"),sQuery(id+"F33.wireOp",EDGE,"E72.MirrorCS"),sQuery(id+"F33.wireOp",EDGE,"E73.MirrorCS"),sQuery(id+"F33.wireOp",EDGE,"E74.MirrorCS"),sQuery(id+"F33.wireOp",EDGE,"E75.MirrorCS"),sQuery(id+"F33.wireOp",EDGE,"E77.MirrorCS")])]})});
            var Q23;
            Q23=makeQuery(id+"F35.opBoolean","SPLIT",BODY,{"disambiguationData":[OD(24.0)],"derivedFrom":makeQuery(id+"F34.opExtrude","SWEPT_BODY",BODY,{"disambiguationData":[OSD([sQuery(id+"F0.wireOp",EDGE,"E0.bottom"),sQuery(id+"F0.wireOp",EDGE,"E0.left"),sQuery(id+"F0.wireOp",EDGE,"E0.right"),sQuery(id+"F0.wireOp",EDGE,"E1"),sQuery(id+"F0.wireOp",EDGE,"E2"),sQuery(id+"F0.wireOp",EDGE,"E3"),sQuery(id+"F0.wireOp",EDGE,"E4"),sQuery(id+"F0.wireOp",EDGE,"E5"),sQuery(id+"F0.wireOp",EDGE,"E6"),sQuery(id+"F0.wireOp",EDGE,"E7"),sQuery(id+"F0.wireOp",EDGE,"E8"),sQuery(id+"F0.wireOp",EDGE,"E9"),sQuery(id+"F0.wireOp",EDGE,"E10"),sQuery(id+"F0.wireOp",EDGE,"E11"),sQuery(id+"F0.wireOp",EDGE,"E12"),sQuery(id+"F0.wireOp",EDGE,"E13"),sQuery(id+"F0.wireOp",EDGE,"E14"),sQuery(id+"F0.wireOp",EDGE,"E15"),sQuery(id+"F0.wireOp",EDGE,"E16"),sQuery(id+"F0.wireOp",EDGE,"E17"),sQuery(id+"F0.wireOp",EDGE,"E18"),sQuery(id+"F0.wireOp",EDGE,"E19"),sQuery(id+"F0.wireOp",EDGE,"E20"),sQuery(id+"F33.wireOp",EDGE,"E66"),sQuery(id+"F33.wireOp",EDGE,"E68"),sQuery(id+"F33.wireOp",EDGE,"E69"),sQuery(id+"F33.wireOp",EDGE,"E70"),sQuery(id+"F33.wireOp",EDGE,"E71"),sQuery(id+"F33.wireOp",EDGE,"E72.MirrorCS"),sQuery(id+"F33.wireOp",EDGE,"E73.MirrorCS"),sQuery(id+"F33.wireOp",EDGE,"E74.MirrorCS"),sQuery(id+"F33.wireOp",EDGE,"E75.MirrorCS"),sQuery(id+"F33.wireOp",EDGE,"E77.MirrorCS")])]})});
            var Q24;
            Q24=makeQuery(id+"F35.opBoolean","SPLIT",BODY,{"disambiguationData":[OD(25.0)],"derivedFrom":makeQuery(id+"F34.opExtrude","SWEPT_BODY",BODY,{"disambiguationData":[OSD([sQuery(id+"F0.wireOp",EDGE,"E0.bottom"),sQuery(id+"F0.wireOp",EDGE,"E0.left"),sQuery(id+"F0.wireOp",EDGE,"E0.right"),sQuery(id+"F0.wireOp",EDGE,"E1"),sQuery(id+"F0.wireOp",EDGE,"E2"),sQuery(id+"F0.wireOp",EDGE,"E3"),sQuery(id+"F0.wireOp",EDGE,"E4"),sQuery(id+"F0.wireOp",EDGE,"E5"),sQuery(id+"F0.wireOp",EDGE,"E6"),sQuery(id+"F0.wireOp",EDGE,"E7"),sQuery(id+"F0.wireOp",EDGE,"E8"),sQuery(id+"F0.wireOp",EDGE,"E9"),sQuery(id+"F0.wireOp",EDGE,"E10"),sQuery(id+"F0.wireOp",EDGE,"E11"),sQuery(id+"F0.wireOp",EDGE,"E12"),sQuery(id+"F0.wireOp",EDGE,"E13"),sQuery(id+"F0.wireOp",EDGE,"E14"),sQuery(id+"F0.wireOp",EDGE,"E15"),sQuery(id+"F0.wireOp",EDGE,"E16"),sQuery(id+"F0.wireOp",EDGE,"E17"),sQuery(id+"F0.wireOp",EDGE,"E18"),sQuery(id+"F0.wireOp",EDGE,"E19"),sQuery(id+"F0.wireOp",EDGE,"E20"),sQuery(id+"F33.wireOp",EDGE,"E66"),sQuery(id+"F33.wireOp",EDGE,"E68"),sQuery(id+"F33.wireOp",EDGE,"E69"),sQuery(id+"F33.wireOp",EDGE,"E70"),sQuery(id+"F33.wireOp",EDGE,"E71"),sQuery(id+"F33.wireOp",EDGE,"E72.MirrorCS"),sQuery(id+"F33.wireOp",EDGE,"E73.MirrorCS"),sQuery(id+"F33.wireOp",EDGE,"E74.MirrorCS"),sQuery(id+"F33.wireOp",EDGE,"E75.MirrorCS"),sQuery(id+"F33.wireOp",EDGE,"E77.MirrorCS")])]})});
            var Q25;
            Q25=makeQuery(id+"F35.opBoolean","SPLIT",BODY,{"disambiguationData":[OD(26.0)],"derivedFrom":makeQuery(id+"F34.opExtrude","SWEPT_BODY",BODY,{"disambiguationData":[OSD([sQuery(id+"F0.wireOp",EDGE,"E0.bottom"),sQuery(id+"F0.wireOp",EDGE,"E0.left"),sQuery(id+"F0.wireOp",EDGE,"E0.right"),sQuery(id+"F0.wireOp",EDGE,"E1"),sQuery(id+"F0.wireOp",EDGE,"E2"),sQuery(id+"F0.wireOp",EDGE,"E3"),sQuery(id+"F0.wireOp",EDGE,"E4"),sQuery(id+"F0.wireOp",EDGE,"E5"),sQuery(id+"F0.wireOp",EDGE,"E6"),sQuery(id+"F0.wireOp",EDGE,"E7"),sQuery(id+"F0.wireOp",EDGE,"E8"),sQuery(id+"F0.wireOp",EDGE,"E9"),sQuery(id+"F0.wireOp",EDGE,"E10"),sQuery(id+"F0.wireOp",EDGE,"E11"),sQuery(id+"F0.wireOp",EDGE,"E12"),sQuery(id+"F0.wireOp",EDGE,"E13"),sQuery(id+"F0.wireOp",EDGE,"E14"),sQuery(id+"F0.wireOp",EDGE,"E15"),sQuery(id+"F0.wireOp",EDGE,"E16"),sQuery(id+"F0.wireOp",EDGE,"E17"),sQuery(id+"F0.wireOp",EDGE,"E18"),sQuery(id+"F0.wireOp",EDGE,"E19"),sQuery(id+"F0.wireOp",EDGE,"E20"),sQuery(id+"F33.wireOp",EDGE,"E66"),sQuery(id+"F33.wireOp",EDGE,"E68"),sQuery(id+"F33.wireOp",EDGE,"E69"),sQuery(id+"F33.wireOp",EDGE,"E70"),sQuery(id+"F33.wireOp",EDGE,"E71"),sQuery(id+"F33.wireOp",EDGE,"E72.MirrorCS"),sQuery(id+"F33.wireOp",EDGE,"E73.MirrorCS"),sQuery(id+"F33.wireOp",EDGE,"E74.MirrorCS"),sQuery(id+"F33.wireOp",EDGE,"E75.MirrorCS"),sQuery(id+"F33.wireOp",EDGE,"E77.MirrorCS")])]})});
            var Q26;
            Q26=makeQuery(id+"F35.opBoolean","SPLIT",BODY,{"disambiguationData":[OD(27.0)],"derivedFrom":makeQuery(id+"F34.opExtrude","SWEPT_BODY",BODY,{"disambiguationData":[OSD([sQuery(id+"F0.wireOp",EDGE,"E0.bottom"),sQuery(id+"F0.wireOp",EDGE,"E0.left"),sQuery(id+"F0.wireOp",EDGE,"E0.right"),sQuery(id+"F0.wireOp",EDGE,"E1"),sQuery(id+"F0.wireOp",EDGE,"E2"),sQuery(id+"F0.wireOp",EDGE,"E3"),sQuery(id+"F0.wireOp",EDGE,"E4"),sQuery(id+"F0.wireOp",EDGE,"E5"),sQuery(id+"F0.wireOp",EDGE,"E6"),sQuery(id+"F0.wireOp",EDGE,"E7"),sQuery(id+"F0.wireOp",EDGE,"E8"),sQuery(id+"F0.wireOp",EDGE,"E9"),sQuery(id+"F0.wireOp",EDGE,"E10"),sQuery(id+"F0.wireOp",EDGE,"E11"),sQuery(id+"F0.wireOp",EDGE,"E12"),sQuery(id+"F0.wireOp",EDGE,"E13"),sQuery(id+"F0.wireOp",EDGE,"E14"),sQuery(id+"F0.wireOp",EDGE,"E15"),sQuery(id+"F0.wireOp",EDGE,"E16"),sQuery(id+"F0.wireOp",EDGE,"E17"),sQuery(id+"F0.wireOp",EDGE,"E18"),sQuery(id+"F0.wireOp",EDGE,"E19"),sQuery(id+"F0.wireOp",EDGE,"E20"),sQuery(id+"F33.wireOp",EDGE,"E66"),sQuery(id+"F33.wireOp",EDGE,"E68"),sQuery(id+"F33.wireOp",EDGE,"E69"),sQuery(id+"F33.wireOp",EDGE,"E70"),sQuery(id+"F33.wireOp",EDGE,"E71"),sQuery(id+"F33.wireOp",EDGE,"E72.MirrorCS"),sQuery(id+"F33.wireOp",EDGE,"E73.MirrorCS"),sQuery(id+"F33.wireOp",EDGE,"E74.MirrorCS"),sQuery(id+"F33.wireOp",EDGE,"E75.MirrorCS"),sQuery(id+"F33.wireOp",EDGE,"E77.MirrorCS")])]})});
            var Q27;
            Q27=makeQuery(id+"F35.opBoolean","SPLIT",BODY,{"disambiguationData":[OD(28.0)],"derivedFrom":makeQuery(id+"F34.opExtrude","SWEPT_BODY",BODY,{"disambiguationData":[OSD([sQuery(id+"F0.wireOp",EDGE,"E0.bottom"),sQuery(id+"F0.wireOp",EDGE,"E0.left"),sQuery(id+"F0.wireOp",EDGE,"E0.right"),sQuery(id+"F0.wireOp",EDGE,"E1"),sQuery(id+"F0.wireOp",EDGE,"E2"),sQuery(id+"F0.wireOp",EDGE,"E3"),sQuery(id+"F0.wireOp",EDGE,"E4"),sQuery(id+"F0.wireOp",EDGE,"E5"),sQuery(id+"F0.wireOp",EDGE,"E6"),sQuery(id+"F0.wireOp",EDGE,"E7"),sQuery(id+"F0.wireOp",EDGE,"E8"),sQuery(id+"F0.wireOp",EDGE,"E9"),sQuery(id+"F0.wireOp",EDGE,"E10"),sQuery(id+"F0.wireOp",EDGE,"E11"),sQuery(id+"F0.wireOp",EDGE,"E12"),sQuery(id+"F0.wireOp",EDGE,"E13"),sQuery(id+"F0.wireOp",EDGE,"E14"),sQuery(id+"F0.wireOp",EDGE,"E15"),sQuery(id+"F0.wireOp",EDGE,"E16"),sQuery(id+"F0.wireOp",EDGE,"E17"),sQuery(id+"F0.wireOp",EDGE,"E18"),sQuery(id+"F0.wireOp",EDGE,"E19"),sQuery(id+"F0.wireOp",EDGE,"E20"),sQuery(id+"F33.wireOp",EDGE,"E66"),sQuery(id+"F33.wireOp",EDGE,"E68"),sQuery(id+"F33.wireOp",EDGE,"E69"),sQuery(id+"F33.wireOp",EDGE,"E70"),sQuery(id+"F33.wireOp",EDGE,"E71"),sQuery(id+"F33.wireOp",EDGE,"E72.MirrorCS"),sQuery(id+"F33.wireOp",EDGE,"E73.MirrorCS"),sQuery(id+"F33.wireOp",EDGE,"E74.MirrorCS"),sQuery(id+"F33.wireOp",EDGE,"E75.MirrorCS"),sQuery(id+"F33.wireOp",EDGE,"E77.MirrorCS")])]})});
            var Q28;
            Q28=makeQuery(id+"F35.opBoolean","SPLIT",BODY,{"disambiguationData":[OD(29.0)],"derivedFrom":makeQuery(id+"F34.opExtrude","SWEPT_BODY",BODY,{"disambiguationData":[OSD([sQuery(id+"F0.wireOp",EDGE,"E0.bottom"),sQuery(id+"F0.wireOp",EDGE,"E0.left"),sQuery(id+"F0.wireOp",EDGE,"E0.right"),sQuery(id+"F0.wireOp",EDGE,"E1"),sQuery(id+"F0.wireOp",EDGE,"E2"),sQuery(id+"F0.wireOp",EDGE,"E3"),sQuery(id+"F0.wireOp",EDGE,"E4"),sQuery(id+"F0.wireOp",EDGE,"E5"),sQuery(id+"F0.wireOp",EDGE,"E6"),sQuery(id+"F0.wireOp",EDGE,"E7"),sQuery(id+"F0.wireOp",EDGE,"E8"),sQuery(id+"F0.wireOp",EDGE,"E9"),sQuery(id+"F0.wireOp",EDGE,"E10"),sQuery(id+"F0.wireOp",EDGE,"E11"),sQuery(id+"F0.wireOp",EDGE,"E12"),sQuery(id+"F0.wireOp",EDGE,"E13"),sQuery(id+"F0.wireOp",EDGE,"E14"),sQuery(id+"F0.wireOp",EDGE,"E15"),sQuery(id+"F0.wireOp",EDGE,"E16"),sQuery(id+"F0.wireOp",EDGE,"E17"),sQuery(id+"F0.wireOp",EDGE,"E18"),sQuery(id+"F0.wireOp",EDGE,"E19"),sQuery(id+"F0.wireOp",EDGE,"E20"),sQuery(id+"F33.wireOp",EDGE,"E66"),sQuery(id+"F33.wireOp",EDGE,"E68"),sQuery(id+"F33.wireOp",EDGE,"E69"),sQuery(id+"F33.wireOp",EDGE,"E70"),sQuery(id+"F33.wireOp",EDGE,"E71"),sQuery(id+"F33.wireOp",EDGE,"E72.MirrorCS"),sQuery(id+"F33.wireOp",EDGE,"E73.MirrorCS"),sQuery(id+"F33.wireOp",EDGE,"E74.MirrorCS"),sQuery(id+"F33.wireOp",EDGE,"E75.MirrorCS"),sQuery(id+"F33.wireOp",EDGE,"E77.MirrorCS")])]})});
            var Q29;
            Q29=makeQuery(id+"F35.opBoolean","SPLIT",BODY,{"disambiguationData":[OD(30.0)],"derivedFrom":makeQuery(id+"F34.opExtrude","SWEPT_BODY",BODY,{"disambiguationData":[OSD([sQuery(id+"F0.wireOp",EDGE,"E0.bottom"),sQuery(id+"F0.wireOp",EDGE,"E0.left"),sQuery(id+"F0.wireOp",EDGE,"E0.right"),sQuery(id+"F0.wireOp",EDGE,"E1"),sQuery(id+"F0.wireOp",EDGE,"E2"),sQuery(id+"F0.wireOp",EDGE,"E3"),sQuery(id+"F0.wireOp",EDGE,"E4"),sQuery(id+"F0.wireOp",EDGE,"E5"),sQuery(id+"F0.wireOp",EDGE,"E6"),sQuery(id+"F0.wireOp",EDGE,"E7"),sQuery(id+"F0.wireOp",EDGE,"E8"),sQuery(id+"F0.wireOp",EDGE,"E9"),sQuery(id+"F0.wireOp",EDGE,"E10"),sQuery(id+"F0.wireOp",EDGE,"E11"),sQuery(id+"F0.wireOp",EDGE,"E12"),sQuery(id+"F0.wireOp",EDGE,"E13"),sQuery(id+"F0.wireOp",EDGE,"E14"),sQuery(id+"F0.wireOp",EDGE,"E15"),sQuery(id+"F0.wireOp",EDGE,"E16"),sQuery(id+"F0.wireOp",EDGE,"E17"),sQuery(id+"F0.wireOp",EDGE,"E18"),sQuery(id+"F0.wireOp",EDGE,"E19"),sQuery(id+"F0.wireOp",EDGE,"E20"),sQuery(id+"F33.wireOp",EDGE,"E66"),sQuery(id+"F33.wireOp",EDGE,"E68"),sQuery(id+"F33.wireOp",EDGE,"E69"),sQuery(id+"F33.wireOp",EDGE,"E70"),sQuery(id+"F33.wireOp",EDGE,"E71"),sQuery(id+"F33.wireOp",EDGE,"E72.MirrorCS"),sQuery(id+"F33.wireOp",EDGE,"E73.MirrorCS"),sQuery(id+"F33.wireOp",EDGE,"E74.MirrorCS"),sQuery(id+"F33.wireOp",EDGE,"E75.MirrorCS"),sQuery(id+"F33.wireOp",EDGE,"E77.MirrorCS")])]})});
            var Q30;
            Q30=makeQuery(id+"F35.opBoolean","SPLIT",BODY,{"disambiguationData":[OD(31.0)],"derivedFrom":makeQuery(id+"F34.opExtrude","SWEPT_BODY",BODY,{"disambiguationData":[OSD([sQuery(id+"F0.wireOp",EDGE,"E0.bottom"),sQuery(id+"F0.wireOp",EDGE,"E0.left"),sQuery(id+"F0.wireOp",EDGE,"E0.right"),sQuery(id+"F0.wireOp",EDGE,"E1"),sQuery(id+"F0.wireOp",EDGE,"E2"),sQuery(id+"F0.wireOp",EDGE,"E3"),sQuery(id+"F0.wireOp",EDGE,"E4"),sQuery(id+"F0.wireOp",EDGE,"E5"),sQuery(id+"F0.wireOp",EDGE,"E6"),sQuery(id+"F0.wireOp",EDGE,"E7"),sQuery(id+"F0.wireOp",EDGE,"E8"),sQuery(id+"F0.wireOp",EDGE,"E9"),sQuery(id+"F0.wireOp",EDGE,"E10"),sQuery(id+"F0.wireOp",EDGE,"E11"),sQuery(id+"F0.wireOp",EDGE,"E12"),sQuery(id+"F0.wireOp",EDGE,"E13"),sQuery(id+"F0.wireOp",EDGE,"E14"),sQuery(id+"F0.wireOp",EDGE,"E15"),sQuery(id+"F0.wireOp",EDGE,"E16"),sQuery(id+"F0.wireOp",EDGE,"E17"),sQuery(id+"F0.wireOp",EDGE,"E18"),sQuery(id+"F0.wireOp",EDGE,"E19"),sQuery(id+"F0.wireOp",EDGE,"E20"),sQuery(id+"F33.wireOp",EDGE,"E66"),sQuery(id+"F33.wireOp",EDGE,"E68"),sQuery(id+"F33.wireOp",EDGE,"E69"),sQuery(id+"F33.wireOp",EDGE,"E70"),sQuery(id+"F33.wireOp",EDGE,"E71"),sQuery(id+"F33.wireOp",EDGE,"E72.MirrorCS"),sQuery(id+"F33.wireOp",EDGE,"E73.MirrorCS"),sQuery(id+"F33.wireOp",EDGE,"E74.MirrorCS"),sQuery(id+"F33.wireOp",EDGE,"E75.MirrorCS"),sQuery(id+"F33.wireOp",EDGE,"E77.MirrorCS")])]})});
            var Q31;
            Q31=makeQuery(id+"F35.opBoolean","SPLIT",BODY,{"disambiguationData":[OD(32.0)],"derivedFrom":makeQuery(id+"F34.opExtrude","SWEPT_BODY",BODY,{"disambiguationData":[OSD([sQuery(id+"F0.wireOp",EDGE,"E0.bottom"),sQuery(id+"F0.wireOp",EDGE,"E0.left"),sQuery(id+"F0.wireOp",EDGE,"E0.right"),sQuery(id+"F0.wireOp",EDGE,"E1"),sQuery(id+"F0.wireOp",EDGE,"E2"),sQuery(id+"F0.wireOp",EDGE,"E3"),sQuery(id+"F0.wireOp",EDGE,"E4"),sQuery(id+"F0.wireOp",EDGE,"E5"),sQuery(id+"F0.wireOp",EDGE,"E6"),sQuery(id+"F0.wireOp",EDGE,"E7"),sQuery(id+"F0.wireOp",EDGE,"E8"),sQuery(id+"F0.wireOp",EDGE,"E9"),sQuery(id+"F0.wireOp",EDGE,"E10"),sQuery(id+"F0.wireOp",EDGE,"E11"),sQuery(id+"F0.wireOp",EDGE,"E12"),sQuery(id+"F0.wireOp",EDGE,"E13"),sQuery(id+"F0.wireOp",EDGE,"E14"),sQuery(id+"F0.wireOp",EDGE,"E15"),sQuery(id+"F0.wireOp",EDGE,"E16"),sQuery(id+"F0.wireOp",EDGE,"E17"),sQuery(id+"F0.wireOp",EDGE,"E18"),sQuery(id+"F0.wireOp",EDGE,"E19"),sQuery(id+"F0.wireOp",EDGE,"E20"),sQuery(id+"F33.wireOp",EDGE,"E66"),sQuery(id+"F33.wireOp",EDGE,"E68"),sQuery(id+"F33.wireOp",EDGE,"E69"),sQuery(id+"F33.wireOp",EDGE,"E70"),sQuery(id+"F33.wireOp",EDGE,"E71"),sQuery(id+"F33.wireOp",EDGE,"E72.MirrorCS"),sQuery(id+"F33.wireOp",EDGE,"E73.MirrorCS"),sQuery(id+"F33.wireOp",EDGE,"E74.MirrorCS"),sQuery(id+"F33.wireOp",EDGE,"E75.MirrorCS"),sQuery(id+"F33.wireOp",EDGE,"E77.MirrorCS")])]})});
            var Q32;
            Q32=makeQuery(id+"F35.opBoolean","SPLIT",BODY,{"disambiguationData":[OD(33.0)],"derivedFrom":makeQuery(id+"F34.opExtrude","SWEPT_BODY",BODY,{"disambiguationData":[OSD([sQuery(id+"F0.wireOp",EDGE,"E0.bottom"),sQuery(id+"F0.wireOp",EDGE,"E0.left"),sQuery(id+"F0.wireOp",EDGE,"E0.right"),sQuery(id+"F0.wireOp",EDGE,"E1"),sQuery(id+"F0.wireOp",EDGE,"E2"),sQuery(id+"F0.wireOp",EDGE,"E3"),sQuery(id+"F0.wireOp",EDGE,"E4"),sQuery(id+"F0.wireOp",EDGE,"E5"),sQuery(id+"F0.wireOp",EDGE,"E6"),sQuery(id+"F0.wireOp",EDGE,"E7"),sQuery(id+"F0.wireOp",EDGE,"E8"),sQuery(id+"F0.wireOp",EDGE,"E9"),sQuery(id+"F0.wireOp",EDGE,"E10"),sQuery(id+"F0.wireOp",EDGE,"E11"),sQuery(id+"F0.wireOp",EDGE,"E12"),sQuery(id+"F0.wireOp",EDGE,"E13"),sQuery(id+"F0.wireOp",EDGE,"E14"),sQuery(id+"F0.wireOp",EDGE,"E15"),sQuery(id+"F0.wireOp",EDGE,"E16"),sQuery(id+"F0.wireOp",EDGE,"E17"),sQuery(id+"F0.wireOp",EDGE,"E18"),sQuery(id+"F0.wireOp",EDGE,"E19"),sQuery(id+"F0.wireOp",EDGE,"E20"),sQuery(id+"F33.wireOp",EDGE,"E66"),sQuery(id+"F33.wireOp",EDGE,"E68"),sQuery(id+"F33.wireOp",EDGE,"E69"),sQuery(id+"F33.wireOp",EDGE,"E70"),sQuery(id+"F33.wireOp",EDGE,"E71"),sQuery(id+"F33.wireOp",EDGE,"E72.MirrorCS"),sQuery(id+"F33.wireOp",EDGE,"E73.MirrorCS"),sQuery(id+"F33.wireOp",EDGE,"E74.MirrorCS"),sQuery(id+"F33.wireOp",EDGE,"E75.MirrorCS"),sQuery(id+"F33.wireOp",EDGE,"E77.MirrorCS")])]})});
            var Q33;
            Q33=makeQuery(id+"F35.opBoolean","SPLIT",BODY,{"disambiguationData":[OD(35.0)],"derivedFrom":makeQuery(id+"F34.opExtrude","SWEPT_BODY",BODY,{"disambiguationData":[OSD([sQuery(id+"F0.wireOp",EDGE,"E0.bottom"),sQuery(id+"F0.wireOp",EDGE,"E0.left"),sQuery(id+"F0.wireOp",EDGE,"E0.right"),sQuery(id+"F0.wireOp",EDGE,"E1"),sQuery(id+"F0.wireOp",EDGE,"E2"),sQuery(id+"F0.wireOp",EDGE,"E3"),sQuery(id+"F0.wireOp",EDGE,"E4"),sQuery(id+"F0.wireOp",EDGE,"E5"),sQuery(id+"F0.wireOp",EDGE,"E6"),sQuery(id+"F0.wireOp",EDGE,"E7"),sQuery(id+"F0.wireOp",EDGE,"E8"),sQuery(id+"F0.wireOp",EDGE,"E9"),sQuery(id+"F0.wireOp",EDGE,"E10"),sQuery(id+"F0.wireOp",EDGE,"E11"),sQuery(id+"F0.wireOp",EDGE,"E12"),sQuery(id+"F0.wireOp",EDGE,"E13"),sQuery(id+"F0.wireOp",EDGE,"E14"),sQuery(id+"F0.wireOp",EDGE,"E15"),sQuery(id+"F0.wireOp",EDGE,"E16"),sQuery(id+"F0.wireOp",EDGE,"E17"),sQuery(id+"F0.wireOp",EDGE,"E18"),sQuery(id+"F0.wireOp",EDGE,"E19"),sQuery(id+"F0.wireOp",EDGE,"E20"),sQuery(id+"F33.wireOp",EDGE,"E66"),sQuery(id+"F33.wireOp",EDGE,"E68"),sQuery(id+"F33.wireOp",EDGE,"E69"),sQuery(id+"F33.wireOp",EDGE,"E70"),sQuery(id+"F33.wireOp",EDGE,"E71"),sQuery(id+"F33.wireOp",EDGE,"E72.MirrorCS"),sQuery(id+"F33.wireOp",EDGE,"E73.MirrorCS"),sQuery(id+"F33.wireOp",EDGE,"E74.MirrorCS"),sQuery(id+"F33.wireOp",EDGE,"E75.MirrorCS"),sQuery(id+"F33.wireOp",EDGE,"E77.MirrorCS")])]})});
            var Q34;
            Q34=makeQuery(id+"F35.opBoolean","SPLIT",BODY,{"disambiguationData":[OD(37.0)],"derivedFrom":makeQuery(id+"F34.opExtrude","SWEPT_BODY",BODY,{"disambiguationData":[OSD([sQuery(id+"F0.wireOp",EDGE,"E0.bottom"),sQuery(id+"F0.wireOp",EDGE,"E0.left"),sQuery(id+"F0.wireOp",EDGE,"E0.right"),sQuery(id+"F0.wireOp",EDGE,"E1"),sQuery(id+"F0.wireOp",EDGE,"E2"),sQuery(id+"F0.wireOp",EDGE,"E3"),sQuery(id+"F0.wireOp",EDGE,"E4"),sQuery(id+"F0.wireOp",EDGE,"E5"),sQuery(id+"F0.wireOp",EDGE,"E6"),sQuery(id+"F0.wireOp",EDGE,"E7"),sQuery(id+"F0.wireOp",EDGE,"E8"),sQuery(id+"F0.wireOp",EDGE,"E9"),sQuery(id+"F0.wireOp",EDGE,"E10"),sQuery(id+"F0.wireOp",EDGE,"E11"),sQuery(id+"F0.wireOp",EDGE,"E12"),sQuery(id+"F0.wireOp",EDGE,"E13"),sQuery(id+"F0.wireOp",EDGE,"E14"),sQuery(id+"F0.wireOp",EDGE,"E15"),sQuery(id+"F0.wireOp",EDGE,"E16"),sQuery(id+"F0.wireOp",EDGE,"E17"),sQuery(id+"F0.wireOp",EDGE,"E18"),sQuery(id+"F0.wireOp",EDGE,"E19"),sQuery(id+"F0.wireOp",EDGE,"E20"),sQuery(id+"F33.wireOp",EDGE,"E66"),sQuery(id+"F33.wireOp",EDGE,"E68"),sQuery(id+"F33.wireOp",EDGE,"E69"),sQuery(id+"F33.wireOp",EDGE,"E70"),sQuery(id+"F33.wireOp",EDGE,"E71"),sQuery(id+"F33.wireOp",EDGE,"E72.MirrorCS"),sQuery(id+"F33.wireOp",EDGE,"E73.MirrorCS"),sQuery(id+"F33.wireOp",EDGE,"E74.MirrorCS"),sQuery(id+"F33.wireOp",EDGE,"E75.MirrorCS"),sQuery(id+"F33.wireOp",EDGE,"E77.MirrorCS")])]})});
            var Q35;
            Q35=makeQuery(id+"F35.opBoolean","SPLIT",BODY,{"disambiguationData":[OD(38.0)],"derivedFrom":makeQuery(id+"F34.opExtrude","SWEPT_BODY",BODY,{"disambiguationData":[OSD([sQuery(id+"F0.wireOp",EDGE,"E0.bottom"),sQuery(id+"F0.wireOp",EDGE,"E0.left"),sQuery(id+"F0.wireOp",EDGE,"E0.right"),sQuery(id+"F0.wireOp",EDGE,"E1"),sQuery(id+"F0.wireOp",EDGE,"E2"),sQuery(id+"F0.wireOp",EDGE,"E3"),sQuery(id+"F0.wireOp",EDGE,"E4"),sQuery(id+"F0.wireOp",EDGE,"E5"),sQuery(id+"F0.wireOp",EDGE,"E6"),sQuery(id+"F0.wireOp",EDGE,"E7"),sQuery(id+"F0.wireOp",EDGE,"E8"),sQuery(id+"F0.wireOp",EDGE,"E9"),sQuery(id+"F0.wireOp",EDGE,"E10"),sQuery(id+"F0.wireOp",EDGE,"E11"),sQuery(id+"F0.wireOp",EDGE,"E12"),sQuery(id+"F0.wireOp",EDGE,"E13"),sQuery(id+"F0.wireOp",EDGE,"E14"),sQuery(id+"F0.wireOp",EDGE,"E15"),sQuery(id+"F0.wireOp",EDGE,"E16"),sQuery(id+"F0.wireOp",EDGE,"E17"),sQuery(id+"F0.wireOp",EDGE,"E18"),sQuery(id+"F0.wireOp",EDGE,"E19"),sQuery(id+"F0.wireOp",EDGE,"E20"),sQuery(id+"F33.wireOp",EDGE,"E66"),sQuery(id+"F33.wireOp",EDGE,"E68"),sQuery(id+"F33.wireOp",EDGE,"E69"),sQuery(id+"F33.wireOp",EDGE,"E70"),sQuery(id+"F33.wireOp",EDGE,"E71"),sQuery(id+"F33.wireOp",EDGE,"E72.MirrorCS"),sQuery(id+"F33.wireOp",EDGE,"E73.MirrorCS"),sQuery(id+"F33.wireOp",EDGE,"E74.MirrorCS"),sQuery(id+"F33.wireOp",EDGE,"E75.MirrorCS"),sQuery(id+"F33.wireOp",EDGE,"E77.MirrorCS")])]})});
            var Q36;
            Q36=makeQuery(id+"F35.opBoolean","SPLIT",BODY,{"disambiguationData":[OD(39.0)],"derivedFrom":makeQuery(id+"F34.opExtrude","SWEPT_BODY",BODY,{"disambiguationData":[OSD([sQuery(id+"F0.wireOp",EDGE,"E0.bottom"),sQuery(id+"F0.wireOp",EDGE,"E0.left"),sQuery(id+"F0.wireOp",EDGE,"E0.right"),sQuery(id+"F0.wireOp",EDGE,"E1"),sQuery(id+"F0.wireOp",EDGE,"E2"),sQuery(id+"F0.wireOp",EDGE,"E3"),sQuery(id+"F0.wireOp",EDGE,"E4"),sQuery(id+"F0.wireOp",EDGE,"E5"),sQuery(id+"F0.wireOp",EDGE,"E6"),sQuery(id+"F0.wireOp",EDGE,"E7"),sQuery(id+"F0.wireOp",EDGE,"E8"),sQuery(id+"F0.wireOp",EDGE,"E9"),sQuery(id+"F0.wireOp",EDGE,"E10"),sQuery(id+"F0.wireOp",EDGE,"E11"),sQuery(id+"F0.wireOp",EDGE,"E12"),sQuery(id+"F0.wireOp",EDGE,"E13"),sQuery(id+"F0.wireOp",EDGE,"E14"),sQuery(id+"F0.wireOp",EDGE,"E15"),sQuery(id+"F0.wireOp",EDGE,"E16"),sQuery(id+"F0.wireOp",EDGE,"E17"),sQuery(id+"F0.wireOp",EDGE,"E18"),sQuery(id+"F0.wireOp",EDGE,"E19"),sQuery(id+"F0.wireOp",EDGE,"E20"),sQuery(id+"F33.wireOp",EDGE,"E66"),sQuery(id+"F33.wireOp",EDGE,"E68"),sQuery(id+"F33.wireOp",EDGE,"E69"),sQuery(id+"F33.wireOp",EDGE,"E70"),sQuery(id+"F33.wireOp",EDGE,"E71"),sQuery(id+"F33.wireOp",EDGE,"E72.MirrorCS"),sQuery(id+"F33.wireOp",EDGE,"E73.MirrorCS"),sQuery(id+"F33.wireOp",EDGE,"E74.MirrorCS"),sQuery(id+"F33.wireOp",EDGE,"E75.MirrorCS"),sQuery(id+"F33.wireOp",EDGE,"E77.MirrorCS")])]})});
            var Q37;
            Q37=makeQuery(id+"F35.opBoolean","SPLIT",BODY,{"disambiguationData":[OD(40.0)],"derivedFrom":makeQuery(id+"F34.opExtrude","SWEPT_BODY",BODY,{"disambiguationData":[OSD([sQuery(id+"F0.wireOp",EDGE,"E0.bottom"),sQuery(id+"F0.wireOp",EDGE,"E0.left"),sQuery(id+"F0.wireOp",EDGE,"E0.right"),sQuery(id+"F0.wireOp",EDGE,"E1"),sQuery(id+"F0.wireOp",EDGE,"E2"),sQuery(id+"F0.wireOp",EDGE,"E3"),sQuery(id+"F0.wireOp",EDGE,"E4"),sQuery(id+"F0.wireOp",EDGE,"E5"),sQuery(id+"F0.wireOp",EDGE,"E6"),sQuery(id+"F0.wireOp",EDGE,"E7"),sQuery(id+"F0.wireOp",EDGE,"E8"),sQuery(id+"F0.wireOp",EDGE,"E9"),sQuery(id+"F0.wireOp",EDGE,"E10"),sQuery(id+"F0.wireOp",EDGE,"E11"),sQuery(id+"F0.wireOp",EDGE,"E12"),sQuery(id+"F0.wireOp",EDGE,"E13"),sQuery(id+"F0.wireOp",EDGE,"E14"),sQuery(id+"F0.wireOp",EDGE,"E15"),sQuery(id+"F0.wireOp",EDGE,"E16"),sQuery(id+"F0.wireOp",EDGE,"E17"),sQuery(id+"F0.wireOp",EDGE,"E18"),sQuery(id+"F0.wireOp",EDGE,"E19"),sQuery(id+"F0.wireOp",EDGE,"E20"),sQuery(id+"F33.wireOp",EDGE,"E66"),sQuery(id+"F33.wireOp",EDGE,"E68"),sQuery(id+"F33.wireOp",EDGE,"E69"),sQuery(id+"F33.wireOp",EDGE,"E70"),sQuery(id+"F33.wireOp",EDGE,"E71"),sQuery(id+"F33.wireOp",EDGE,"E72.MirrorCS"),sQuery(id+"F33.wireOp",EDGE,"E73.MirrorCS"),sQuery(id+"F33.wireOp",EDGE,"E74.MirrorCS"),sQuery(id+"F33.wireOp",EDGE,"E75.MirrorCS"),sQuery(id+"F33.wireOp",EDGE,"E77.MirrorCS")])]})});
            var Q38;
            Q38=makeQuery(id+"F35.opBoolean","SPLIT",BODY,{"disambiguationData":[OD(41.0)],"derivedFrom":makeQuery(id+"F34.opExtrude","SWEPT_BODY",BODY,{"disambiguationData":[OSD([sQuery(id+"F0.wireOp",EDGE,"E0.bottom"),sQuery(id+"F0.wireOp",EDGE,"E0.left"),sQuery(id+"F0.wireOp",EDGE,"E0.right"),sQuery(id+"F0.wireOp",EDGE,"E1"),sQuery(id+"F0.wireOp",EDGE,"E2"),sQuery(id+"F0.wireOp",EDGE,"E3"),sQuery(id+"F0.wireOp",EDGE,"E4"),sQuery(id+"F0.wireOp",EDGE,"E5"),sQuery(id+"F0.wireOp",EDGE,"E6"),sQuery(id+"F0.wireOp",EDGE,"E7"),sQuery(id+"F0.wireOp",EDGE,"E8"),sQuery(id+"F0.wireOp",EDGE,"E9"),sQuery(id+"F0.wireOp",EDGE,"E10"),sQuery(id+"F0.wireOp",EDGE,"E11"),sQuery(id+"F0.wireOp",EDGE,"E12"),sQuery(id+"F0.wireOp",EDGE,"E13"),sQuery(id+"F0.wireOp",EDGE,"E14"),sQuery(id+"F0.wireOp",EDGE,"E15"),sQuery(id+"F0.wireOp",EDGE,"E16"),sQuery(id+"F0.wireOp",EDGE,"E17"),sQuery(id+"F0.wireOp",EDGE,"E18"),sQuery(id+"F0.wireOp",EDGE,"E19"),sQuery(id+"F0.wireOp",EDGE,"E20"),sQuery(id+"F33.wireOp",EDGE,"E66"),sQuery(id+"F33.wireOp",EDGE,"E68"),sQuery(id+"F33.wireOp",EDGE,"E69"),sQuery(id+"F33.wireOp",EDGE,"E70"),sQuery(id+"F33.wireOp",EDGE,"E71"),sQuery(id+"F33.wireOp",EDGE,"E72.MirrorCS"),sQuery(id+"F33.wireOp",EDGE,"E73.MirrorCS"),sQuery(id+"F33.wireOp",EDGE,"E74.MirrorCS"),sQuery(id+"F33.wireOp",EDGE,"E75.MirrorCS"),sQuery(id+"F33.wireOp",EDGE,"E77.MirrorCS")])]})});
            var Q39;
            Q39=makeQuery(id+"F35.opBoolean","SPLIT",BODY,{"disambiguationData":[OD(42.0)],"derivedFrom":makeQuery(id+"F34.opExtrude","SWEPT_BODY",BODY,{"disambiguationData":[OSD([sQuery(id+"F0.wireOp",EDGE,"E0.bottom"),sQuery(id+"F0.wireOp",EDGE,"E0.left"),sQuery(id+"F0.wireOp",EDGE,"E0.right"),sQuery(id+"F0.wireOp",EDGE,"E1"),sQuery(id+"F0.wireOp",EDGE,"E2"),sQuery(id+"F0.wireOp",EDGE,"E3"),sQuery(id+"F0.wireOp",EDGE,"E4"),sQuery(id+"F0.wireOp",EDGE,"E5"),sQuery(id+"F0.wireOp",EDGE,"E6"),sQuery(id+"F0.wireOp",EDGE,"E7"),sQuery(id+"F0.wireOp",EDGE,"E8"),sQuery(id+"F0.wireOp",EDGE,"E9"),sQuery(id+"F0.wireOp",EDGE,"E10"),sQuery(id+"F0.wireOp",EDGE,"E11"),sQuery(id+"F0.wireOp",EDGE,"E12"),sQuery(id+"F0.wireOp",EDGE,"E13"),sQuery(id+"F0.wireOp",EDGE,"E14"),sQuery(id+"F0.wireOp",EDGE,"E15"),sQuery(id+"F0.wireOp",EDGE,"E16"),sQuery(id+"F0.wireOp",EDGE,"E17"),sQuery(id+"F0.wireOp",EDGE,"E18"),sQuery(id+"F0.wireOp",EDGE,"E19"),sQuery(id+"F0.wireOp",EDGE,"E20"),sQuery(id+"F33.wireOp",EDGE,"E66"),sQuery(id+"F33.wireOp",EDGE,"E68"),sQuery(id+"F33.wireOp",EDGE,"E69"),sQuery(id+"F33.wireOp",EDGE,"E70"),sQuery(id+"F33.wireOp",EDGE,"E71"),sQuery(id+"F33.wireOp",EDGE,"E72.MirrorCS"),sQuery(id+"F33.wireOp",EDGE,"E73.MirrorCS"),sQuery(id+"F33.wireOp",EDGE,"E74.MirrorCS"),sQuery(id+"F33.wireOp",EDGE,"E75.MirrorCS"),sQuery(id+"F33.wireOp",EDGE,"E77.MirrorCS")])]})});
            var Q40;
            Q40=makeQuery(id+"F35.opBoolean","SPLIT",BODY,{"disambiguationData":[OD(43.0)],"derivedFrom":makeQuery(id+"F34.opExtrude","SWEPT_BODY",BODY,{"disambiguationData":[OSD([sQuery(id+"F0.wireOp",EDGE,"E0.bottom"),sQuery(id+"F0.wireOp",EDGE,"E0.left"),sQuery(id+"F0.wireOp",EDGE,"E0.right"),sQuery(id+"F0.wireOp",EDGE,"E1"),sQuery(id+"F0.wireOp",EDGE,"E2"),sQuery(id+"F0.wireOp",EDGE,"E3"),sQuery(id+"F0.wireOp",EDGE,"E4"),sQuery(id+"F0.wireOp",EDGE,"E5"),sQuery(id+"F0.wireOp",EDGE,"E6"),sQuery(id+"F0.wireOp",EDGE,"E7"),sQuery(id+"F0.wireOp",EDGE,"E8"),sQuery(id+"F0.wireOp",EDGE,"E9"),sQuery(id+"F0.wireOp",EDGE,"E10"),sQuery(id+"F0.wireOp",EDGE,"E11"),sQuery(id+"F0.wireOp",EDGE,"E12"),sQuery(id+"F0.wireOp",EDGE,"E13"),sQuery(id+"F0.wireOp",EDGE,"E14"),sQuery(id+"F0.wireOp",EDGE,"E15"),sQuery(id+"F0.wireOp",EDGE,"E16"),sQuery(id+"F0.wireOp",EDGE,"E17"),sQuery(id+"F0.wireOp",EDGE,"E18"),sQuery(id+"F0.wireOp",EDGE,"E19"),sQuery(id+"F0.wireOp",EDGE,"E20"),sQuery(id+"F33.wireOp",EDGE,"E66"),sQuery(id+"F33.wireOp",EDGE,"E68"),sQuery(id+"F33.wireOp",EDGE,"E69"),sQuery(id+"F33.wireOp",EDGE,"E70"),sQuery(id+"F33.wireOp",EDGE,"E71"),sQuery(id+"F33.wireOp",EDGE,"E72.MirrorCS"),sQuery(id+"F33.wireOp",EDGE,"E73.MirrorCS"),sQuery(id+"F33.wireOp",EDGE,"E74.MirrorCS"),sQuery(id+"F33.wireOp",EDGE,"E75.MirrorCS"),sQuery(id+"F33.wireOp",EDGE,"E77.MirrorCS")])]})});
            var Q41;
            Q41=makeQuery(id+"F35.opBoolean","SPLIT",BODY,{"disambiguationData":[OD(44.0)],"derivedFrom":makeQuery(id+"F34.opExtrude","SWEPT_BODY",BODY,{"disambiguationData":[OSD([sQuery(id+"F0.wireOp",EDGE,"E0.bottom"),sQuery(id+"F0.wireOp",EDGE,"E0.left"),sQuery(id+"F0.wireOp",EDGE,"E0.right"),sQuery(id+"F0.wireOp",EDGE,"E1"),sQuery(id+"F0.wireOp",EDGE,"E2"),sQuery(id+"F0.wireOp",EDGE,"E3"),sQuery(id+"F0.wireOp",EDGE,"E4"),sQuery(id+"F0.wireOp",EDGE,"E5"),sQuery(id+"F0.wireOp",EDGE,"E6"),sQuery(id+"F0.wireOp",EDGE,"E7"),sQuery(id+"F0.wireOp",EDGE,"E8"),sQuery(id+"F0.wireOp",EDGE,"E9"),sQuery(id+"F0.wireOp",EDGE,"E10"),sQuery(id+"F0.wireOp",EDGE,"E11"),sQuery(id+"F0.wireOp",EDGE,"E12"),sQuery(id+"F0.wireOp",EDGE,"E13"),sQuery(id+"F0.wireOp",EDGE,"E14"),sQuery(id+"F0.wireOp",EDGE,"E15"),sQuery(id+"F0.wireOp",EDGE,"E16"),sQuery(id+"F0.wireOp",EDGE,"E17"),sQuery(id+"F0.wireOp",EDGE,"E18"),sQuery(id+"F0.wireOp",EDGE,"E19"),sQuery(id+"F0.wireOp",EDGE,"E20"),sQuery(id+"F33.wireOp",EDGE,"E66"),sQuery(id+"F33.wireOp",EDGE,"E68"),sQuery(id+"F33.wireOp",EDGE,"E69"),sQuery(id+"F33.wireOp",EDGE,"E70"),sQuery(id+"F33.wireOp",EDGE,"E71"),sQuery(id+"F33.wireOp",EDGE,"E72.MirrorCS"),sQuery(id+"F33.wireOp",EDGE,"E73.MirrorCS"),sQuery(id+"F33.wireOp",EDGE,"E74.MirrorCS"),sQuery(id+"F33.wireOp",EDGE,"E75.MirrorCS"),sQuery(id+"F33.wireOp",EDGE,"E77.MirrorCS")])]})});
            var Q42;
            Q42=makeQuery(id+"F35.opBoolean","SPLIT",BODY,{"disambiguationData":[OD(45.0)],"derivedFrom":makeQuery(id+"F34.opExtrude","SWEPT_BODY",BODY,{"disambiguationData":[OSD([sQuery(id+"F0.wireOp",EDGE,"E0.bottom"),sQuery(id+"F0.wireOp",EDGE,"E0.left"),sQuery(id+"F0.wireOp",EDGE,"E0.right"),sQuery(id+"F0.wireOp",EDGE,"E1"),sQuery(id+"F0.wireOp",EDGE,"E2"),sQuery(id+"F0.wireOp",EDGE,"E3"),sQuery(id+"F0.wireOp",EDGE,"E4"),sQuery(id+"F0.wireOp",EDGE,"E5"),sQuery(id+"F0.wireOp",EDGE,"E6"),sQuery(id+"F0.wireOp",EDGE,"E7"),sQuery(id+"F0.wireOp",EDGE,"E8"),sQuery(id+"F0.wireOp",EDGE,"E9"),sQuery(id+"F0.wireOp",EDGE,"E10"),sQuery(id+"F0.wireOp",EDGE,"E11"),sQuery(id+"F0.wireOp",EDGE,"E12"),sQuery(id+"F0.wireOp",EDGE,"E13"),sQuery(id+"F0.wireOp",EDGE,"E14"),sQuery(id+"F0.wireOp",EDGE,"E15"),sQuery(id+"F0.wireOp",EDGE,"E16"),sQuery(id+"F0.wireOp",EDGE,"E17"),sQuery(id+"F0.wireOp",EDGE,"E18"),sQuery(id+"F0.wireOp",EDGE,"E19"),sQuery(id+"F0.wireOp",EDGE,"E20"),sQuery(id+"F33.wireOp",EDGE,"E66"),sQuery(id+"F33.wireOp",EDGE,"E68"),sQuery(id+"F33.wireOp",EDGE,"E69"),sQuery(id+"F33.wireOp",EDGE,"E70"),sQuery(id+"F33.wireOp",EDGE,"E71"),sQuery(id+"F33.wireOp",EDGE,"E72.MirrorCS"),sQuery(id+"F33.wireOp",EDGE,"E73.MirrorCS"),sQuery(id+"F33.wireOp",EDGE,"E74.MirrorCS"),sQuery(id+"F33.wireOp",EDGE,"E75.MirrorCS"),sQuery(id+"F33.wireOp",EDGE,"E77.MirrorCS")])]})});
            var Q43;
            Q43=makeQuery(id+"F35.opBoolean","SPLIT",BODY,{"disambiguationData":[OD(46.0)],"derivedFrom":makeQuery(id+"F34.opExtrude","SWEPT_BODY",BODY,{"disambiguationData":[OSD([sQuery(id+"F0.wireOp",EDGE,"E0.bottom"),sQuery(id+"F0.wireOp",EDGE,"E0.left"),sQuery(id+"F0.wireOp",EDGE,"E0.right"),sQuery(id+"F0.wireOp",EDGE,"E1"),sQuery(id+"F0.wireOp",EDGE,"E2"),sQuery(id+"F0.wireOp",EDGE,"E3"),sQuery(id+"F0.wireOp",EDGE,"E4"),sQuery(id+"F0.wireOp",EDGE,"E5"),sQuery(id+"F0.wireOp",EDGE,"E6"),sQuery(id+"F0.wireOp",EDGE,"E7"),sQuery(id+"F0.wireOp",EDGE,"E8"),sQuery(id+"F0.wireOp",EDGE,"E9"),sQuery(id+"F0.wireOp",EDGE,"E10"),sQuery(id+"F0.wireOp",EDGE,"E11"),sQuery(id+"F0.wireOp",EDGE,"E12"),sQuery(id+"F0.wireOp",EDGE,"E13"),sQuery(id+"F0.wireOp",EDGE,"E14"),sQuery(id+"F0.wireOp",EDGE,"E15"),sQuery(id+"F0.wireOp",EDGE,"E16"),sQuery(id+"F0.wireOp",EDGE,"E17"),sQuery(id+"F0.wireOp",EDGE,"E18"),sQuery(id+"F0.wireOp",EDGE,"E19"),sQuery(id+"F0.wireOp",EDGE,"E20"),sQuery(id+"F33.wireOp",EDGE,"E66"),sQuery(id+"F33.wireOp",EDGE,"E68"),sQuery(id+"F33.wireOp",EDGE,"E69"),sQuery(id+"F33.wireOp",EDGE,"E70"),sQuery(id+"F33.wireOp",EDGE,"E71"),sQuery(id+"F33.wireOp",EDGE,"E72.MirrorCS"),sQuery(id+"F33.wireOp",EDGE,"E73.MirrorCS"),sQuery(id+"F33.wireOp",EDGE,"E74.MirrorCS"),sQuery(id+"F33.wireOp",EDGE,"E75.MirrorCS"),sQuery(id+"F33.wireOp",EDGE,"E77.MirrorCS")])]})});
            var Q44;
            Q44=makeQuery(id+"F35.opBoolean","SPLIT",BODY,{"disambiguationData":[OD(47.0)],"derivedFrom":makeQuery(id+"F34.opExtrude","SWEPT_BODY",BODY,{"disambiguationData":[OSD([sQuery(id+"F0.wireOp",EDGE,"E0.bottom"),sQuery(id+"F0.wireOp",EDGE,"E0.left"),sQuery(id+"F0.wireOp",EDGE,"E0.right"),sQuery(id+"F0.wireOp",EDGE,"E1"),sQuery(id+"F0.wireOp",EDGE,"E2"),sQuery(id+"F0.wireOp",EDGE,"E3"),sQuery(id+"F0.wireOp",EDGE,"E4"),sQuery(id+"F0.wireOp",EDGE,"E5"),sQuery(id+"F0.wireOp",EDGE,"E6"),sQuery(id+"F0.wireOp",EDGE,"E7"),sQuery(id+"F0.wireOp",EDGE,"E8"),sQuery(id+"F0.wireOp",EDGE,"E9"),sQuery(id+"F0.wireOp",EDGE,"E10"),sQuery(id+"F0.wireOp",EDGE,"E11"),sQuery(id+"F0.wireOp",EDGE,"E12"),sQuery(id+"F0.wireOp",EDGE,"E13"),sQuery(id+"F0.wireOp",EDGE,"E14"),sQuery(id+"F0.wireOp",EDGE,"E15"),sQuery(id+"F0.wireOp",EDGE,"E16"),sQuery(id+"F0.wireOp",EDGE,"E17"),sQuery(id+"F0.wireOp",EDGE,"E18"),sQuery(id+"F0.wireOp",EDGE,"E19"),sQuery(id+"F0.wireOp",EDGE,"E20"),sQuery(id+"F33.wireOp",EDGE,"E66"),sQuery(id+"F33.wireOp",EDGE,"E68"),sQuery(id+"F33.wireOp",EDGE,"E69"),sQuery(id+"F33.wireOp",EDGE,"E70"),sQuery(id+"F33.wireOp",EDGE,"E71"),sQuery(id+"F33.wireOp",EDGE,"E72.MirrorCS"),sQuery(id+"F33.wireOp",EDGE,"E73.MirrorCS"),sQuery(id+"F33.wireOp",EDGE,"E74.MirrorCS"),sQuery(id+"F33.wireOp",EDGE,"E75.MirrorCS"),sQuery(id+"F33.wireOp",EDGE,"E77.MirrorCS")])]})});
            var Q45;
            Q45=makeQuery(id+"F35.opBoolean","SPLIT",BODY,{"disambiguationData":[OD(48.0)],"derivedFrom":makeQuery(id+"F34.opExtrude","SWEPT_BODY",BODY,{"disambiguationData":[OSD([sQuery(id+"F0.wireOp",EDGE,"E0.bottom"),sQuery(id+"F0.wireOp",EDGE,"E0.left"),sQuery(id+"F0.wireOp",EDGE,"E0.right"),sQuery(id+"F0.wireOp",EDGE,"E1"),sQuery(id+"F0.wireOp",EDGE,"E2"),sQuery(id+"F0.wireOp",EDGE,"E3"),sQuery(id+"F0.wireOp",EDGE,"E4"),sQuery(id+"F0.wireOp",EDGE,"E5"),sQuery(id+"F0.wireOp",EDGE,"E6"),sQuery(id+"F0.wireOp",EDGE,"E7"),sQuery(id+"F0.wireOp",EDGE,"E8"),sQuery(id+"F0.wireOp",EDGE,"E9"),sQuery(id+"F0.wireOp",EDGE,"E10"),sQuery(id+"F0.wireOp",EDGE,"E11"),sQuery(id+"F0.wireOp",EDGE,"E12"),sQuery(id+"F0.wireOp",EDGE,"E13"),sQuery(id+"F0.wireOp",EDGE,"E14"),sQuery(id+"F0.wireOp",EDGE,"E15"),sQuery(id+"F0.wireOp",EDGE,"E16"),sQuery(id+"F0.wireOp",EDGE,"E17"),sQuery(id+"F0.wireOp",EDGE,"E18"),sQuery(id+"F0.wireOp",EDGE,"E19"),sQuery(id+"F0.wireOp",EDGE,"E20"),sQuery(id+"F33.wireOp",EDGE,"E66"),sQuery(id+"F33.wireOp",EDGE,"E68"),sQuery(id+"F33.wireOp",EDGE,"E69"),sQuery(id+"F33.wireOp",EDGE,"E70"),sQuery(id+"F33.wireOp",EDGE,"E71"),sQuery(id+"F33.wireOp",EDGE,"E72.MirrorCS"),sQuery(id+"F33.wireOp",EDGE,"E73.MirrorCS"),sQuery(id+"F33.wireOp",EDGE,"E74.MirrorCS"),sQuery(id+"F33.wireOp",EDGE,"E75.MirrorCS"),sQuery(id+"F33.wireOp",EDGE,"E77.MirrorCS")])]})});
            var Q46;
            Q46=makeQuery(id+"F35.opBoolean","SPLIT",BODY,{"disambiguationData":[OD(49.0)],"derivedFrom":makeQuery(id+"F34.opExtrude","SWEPT_BODY",BODY,{"disambiguationData":[OSD([sQuery(id+"F0.wireOp",EDGE,"E0.bottom"),sQuery(id+"F0.wireOp",EDGE,"E0.left"),sQuery(id+"F0.wireOp",EDGE,"E0.right"),sQuery(id+"F0.wireOp",EDGE,"E1"),sQuery(id+"F0.wireOp",EDGE,"E2"),sQuery(id+"F0.wireOp",EDGE,"E3"),sQuery(id+"F0.wireOp",EDGE,"E4"),sQuery(id+"F0.wireOp",EDGE,"E5"),sQuery(id+"F0.wireOp",EDGE,"E6"),sQuery(id+"F0.wireOp",EDGE,"E7"),sQuery(id+"F0.wireOp",EDGE,"E8"),sQuery(id+"F0.wireOp",EDGE,"E9"),sQuery(id+"F0.wireOp",EDGE,"E10"),sQuery(id+"F0.wireOp",EDGE,"E11"),sQuery(id+"F0.wireOp",EDGE,"E12"),sQuery(id+"F0.wireOp",EDGE,"E13"),sQuery(id+"F0.wireOp",EDGE,"E14"),sQuery(id+"F0.wireOp",EDGE,"E15"),sQuery(id+"F0.wireOp",EDGE,"E16"),sQuery(id+"F0.wireOp",EDGE,"E17"),sQuery(id+"F0.wireOp",EDGE,"E18"),sQuery(id+"F0.wireOp",EDGE,"E19"),sQuery(id+"F0.wireOp",EDGE,"E20"),sQuery(id+"F33.wireOp",EDGE,"E66"),sQuery(id+"F33.wireOp",EDGE,"E68"),sQuery(id+"F33.wireOp",EDGE,"E69"),sQuery(id+"F33.wireOp",EDGE,"E70"),sQuery(id+"F33.wireOp",EDGE,"E71"),sQuery(id+"F33.wireOp",EDGE,"E72.MirrorCS"),sQuery(id+"F33.wireOp",EDGE,"E73.MirrorCS"),sQuery(id+"F33.wireOp",EDGE,"E74.MirrorCS"),sQuery(id+"F33.wireOp",EDGE,"E75.MirrorCS"),sQuery(id+"F33.wireOp",EDGE,"E77.MirrorCS")])]})});
            var Q47;
            Q47=makeQuery(id+"F35.opBoolean","SPLIT",BODY,{"disambiguationData":[OD(50.0)],"derivedFrom":makeQuery(id+"F34.opExtrude","SWEPT_BODY",BODY,{"disambiguationData":[OSD([sQuery(id+"F0.wireOp",EDGE,"E0.bottom"),sQuery(id+"F0.wireOp",EDGE,"E0.left"),sQuery(id+"F0.wireOp",EDGE,"E0.right"),sQuery(id+"F0.wireOp",EDGE,"E1"),sQuery(id+"F0.wireOp",EDGE,"E2"),sQuery(id+"F0.wireOp",EDGE,"E3"),sQuery(id+"F0.wireOp",EDGE,"E4"),sQuery(id+"F0.wireOp",EDGE,"E5"),sQuery(id+"F0.wireOp",EDGE,"E6"),sQuery(id+"F0.wireOp",EDGE,"E7"),sQuery(id+"F0.wireOp",EDGE,"E8"),sQuery(id+"F0.wireOp",EDGE,"E9"),sQuery(id+"F0.wireOp",EDGE,"E10"),sQuery(id+"F0.wireOp",EDGE,"E11"),sQuery(id+"F0.wireOp",EDGE,"E12"),sQuery(id+"F0.wireOp",EDGE,"E13"),sQuery(id+"F0.wireOp",EDGE,"E14"),sQuery(id+"F0.wireOp",EDGE,"E15"),sQuery(id+"F0.wireOp",EDGE,"E16"),sQuery(id+"F0.wireOp",EDGE,"E17"),sQuery(id+"F0.wireOp",EDGE,"E18"),sQuery(id+"F0.wireOp",EDGE,"E19"),sQuery(id+"F0.wireOp",EDGE,"E20"),sQuery(id+"F33.wireOp",EDGE,"E66"),sQuery(id+"F33.wireOp",EDGE,"E68"),sQuery(id+"F33.wireOp",EDGE,"E69"),sQuery(id+"F33.wireOp",EDGE,"E70"),sQuery(id+"F33.wireOp",EDGE,"E71"),sQuery(id+"F33.wireOp",EDGE,"E72.MirrorCS"),sQuery(id+"F33.wireOp",EDGE,"E73.MirrorCS"),sQuery(id+"F33.wireOp",EDGE,"E74.MirrorCS"),sQuery(id+"F33.wireOp",EDGE,"E75.MirrorCS"),sQuery(id+"F33.wireOp",EDGE,"E77.MirrorCS")])]})});
            var Q48;
            Q48=makeQuery(id+"F35.opBoolean","SPLIT",BODY,{"disambiguationData":[OD(51.0)],"derivedFrom":makeQuery(id+"F34.opExtrude","SWEPT_BODY",BODY,{"disambiguationData":[OSD([sQuery(id+"F0.wireOp",EDGE,"E0.bottom"),sQuery(id+"F0.wireOp",EDGE,"E0.left"),sQuery(id+"F0.wireOp",EDGE,"E0.right"),sQuery(id+"F0.wireOp",EDGE,"E1"),sQuery(id+"F0.wireOp",EDGE,"E2"),sQuery(id+"F0.wireOp",EDGE,"E3"),sQuery(id+"F0.wireOp",EDGE,"E4"),sQuery(id+"F0.wireOp",EDGE,"E5"),sQuery(id+"F0.wireOp",EDGE,"E6"),sQuery(id+"F0.wireOp",EDGE,"E7"),sQuery(id+"F0.wireOp",EDGE,"E8"),sQuery(id+"F0.wireOp",EDGE,"E9"),sQuery(id+"F0.wireOp",EDGE,"E10"),sQuery(id+"F0.wireOp",EDGE,"E11"),sQuery(id+"F0.wireOp",EDGE,"E12"),sQuery(id+"F0.wireOp",EDGE,"E13"),sQuery(id+"F0.wireOp",EDGE,"E14"),sQuery(id+"F0.wireOp",EDGE,"E15"),sQuery(id+"F0.wireOp",EDGE,"E16"),sQuery(id+"F0.wireOp",EDGE,"E17"),sQuery(id+"F0.wireOp",EDGE,"E18"),sQuery(id+"F0.wireOp",EDGE,"E19"),sQuery(id+"F0.wireOp",EDGE,"E20"),sQuery(id+"F33.wireOp",EDGE,"E66"),sQuery(id+"F33.wireOp",EDGE,"E68"),sQuery(id+"F33.wireOp",EDGE,"E69"),sQuery(id+"F33.wireOp",EDGE,"E70"),sQuery(id+"F33.wireOp",EDGE,"E71"),sQuery(id+"F33.wireOp",EDGE,"E72.MirrorCS"),sQuery(id+"F33.wireOp",EDGE,"E73.MirrorCS"),sQuery(id+"F33.wireOp",EDGE,"E74.MirrorCS"),sQuery(id+"F33.wireOp",EDGE,"E75.MirrorCS"),sQuery(id+"F33.wireOp",EDGE,"E77.MirrorCS")])]})});
            var Q49;
            Q49=makeQuery(id+"F35.opBoolean","SPLIT",BODY,{"disambiguationData":[OD(52.0)],"derivedFrom":makeQuery(id+"F34.opExtrude","SWEPT_BODY",BODY,{"disambiguationData":[OSD([sQuery(id+"F0.wireOp",EDGE,"E0.bottom"),sQuery(id+"F0.wireOp",EDGE,"E0.left"),sQuery(id+"F0.wireOp",EDGE,"E0.right"),sQuery(id+"F0.wireOp",EDGE,"E1"),sQuery(id+"F0.wireOp",EDGE,"E2"),sQuery(id+"F0.wireOp",EDGE,"E3"),sQuery(id+"F0.wireOp",EDGE,"E4"),sQuery(id+"F0.wireOp",EDGE,"E5"),sQuery(id+"F0.wireOp",EDGE,"E6"),sQuery(id+"F0.wireOp",EDGE,"E7"),sQuery(id+"F0.wireOp",EDGE,"E8"),sQuery(id+"F0.wireOp",EDGE,"E9"),sQuery(id+"F0.wireOp",EDGE,"E10"),sQuery(id+"F0.wireOp",EDGE,"E11"),sQuery(id+"F0.wireOp",EDGE,"E12"),sQuery(id+"F0.wireOp",EDGE,"E13"),sQuery(id+"F0.wireOp",EDGE,"E14"),sQuery(id+"F0.wireOp",EDGE,"E15"),sQuery(id+"F0.wireOp",EDGE,"E16"),sQuery(id+"F0.wireOp",EDGE,"E17"),sQuery(id+"F0.wireOp",EDGE,"E18"),sQuery(id+"F0.wireOp",EDGE,"E19"),sQuery(id+"F0.wireOp",EDGE,"E20"),sQuery(id+"F33.wireOp",EDGE,"E66"),sQuery(id+"F33.wireOp",EDGE,"E68"),sQuery(id+"F33.wireOp",EDGE,"E69"),sQuery(id+"F33.wireOp",EDGE,"E70"),sQuery(id+"F33.wireOp",EDGE,"E71"),sQuery(id+"F33.wireOp",EDGE,"E72.MirrorCS"),sQuery(id+"F33.wireOp",EDGE,"E73.MirrorCS"),sQuery(id+"F33.wireOp",EDGE,"E74.MirrorCS"),sQuery(id+"F33.wireOp",EDGE,"E75.MirrorCS"),sQuery(id+"F33.wireOp",EDGE,"E77.MirrorCS")])]})});
            var Q50;
            Q50=makeQuery(id+"F35.opBoolean","SPLIT",BODY,{"disambiguationData":[OD(53.0)],"derivedFrom":makeQuery(id+"F34.opExtrude","SWEPT_BODY",BODY,{"disambiguationData":[OSD([sQuery(id+"F0.wireOp",EDGE,"E0.bottom"),sQuery(id+"F0.wireOp",EDGE,"E0.left"),sQuery(id+"F0.wireOp",EDGE,"E0.right"),sQuery(id+"F0.wireOp",EDGE,"E1"),sQuery(id+"F0.wireOp",EDGE,"E2"),sQuery(id+"F0.wireOp",EDGE,"E3"),sQuery(id+"F0.wireOp",EDGE,"E4"),sQuery(id+"F0.wireOp",EDGE,"E5"),sQuery(id+"F0.wireOp",EDGE,"E6"),sQuery(id+"F0.wireOp",EDGE,"E7"),sQuery(id+"F0.wireOp",EDGE,"E8"),sQuery(id+"F0.wireOp",EDGE,"E9"),sQuery(id+"F0.wireOp",EDGE,"E10"),sQuery(id+"F0.wireOp",EDGE,"E11"),sQuery(id+"F0.wireOp",EDGE,"E12"),sQuery(id+"F0.wireOp",EDGE,"E13"),sQuery(id+"F0.wireOp",EDGE,"E14"),sQuery(id+"F0.wireOp",EDGE,"E15"),sQuery(id+"F0.wireOp",EDGE,"E16"),sQuery(id+"F0.wireOp",EDGE,"E17"),sQuery(id+"F0.wireOp",EDGE,"E18"),sQuery(id+"F0.wireOp",EDGE,"E19"),sQuery(id+"F0.wireOp",EDGE,"E20"),sQuery(id+"F33.wireOp",EDGE,"E66"),sQuery(id+"F33.wireOp",EDGE,"E68"),sQuery(id+"F33.wireOp",EDGE,"E69"),sQuery(id+"F33.wireOp",EDGE,"E70"),sQuery(id+"F33.wireOp",EDGE,"E71"),sQuery(id+"F33.wireOp",EDGE,"E72.MirrorCS"),sQuery(id+"F33.wireOp",EDGE,"E73.MirrorCS"),sQuery(id+"F33.wireOp",EDGE,"E74.MirrorCS"),sQuery(id+"F33.wireOp",EDGE,"E75.MirrorCS"),sQuery(id+"F33.wireOp",EDGE,"E77.MirrorCS")])]})});
            var Q51;
            Q51=makeQuery(id+"F35.opBoolean","SPLIT",BODY,{"disambiguationData":[OD(54.0)],"derivedFrom":makeQuery(id+"F34.opExtrude","SWEPT_BODY",BODY,{"disambiguationData":[OSD([sQuery(id+"F0.wireOp",EDGE,"E0.bottom"),sQuery(id+"F0.wireOp",EDGE,"E0.left"),sQuery(id+"F0.wireOp",EDGE,"E0.right"),sQuery(id+"F0.wireOp",EDGE,"E1"),sQuery(id+"F0.wireOp",EDGE,"E2"),sQuery(id+"F0.wireOp",EDGE,"E3"),sQuery(id+"F0.wireOp",EDGE,"E4"),sQuery(id+"F0.wireOp",EDGE,"E5"),sQuery(id+"F0.wireOp",EDGE,"E6"),sQuery(id+"F0.wireOp",EDGE,"E7"),sQuery(id+"F0.wireOp",EDGE,"E8"),sQuery(id+"F0.wireOp",EDGE,"E9"),sQuery(id+"F0.wireOp",EDGE,"E10"),sQuery(id+"F0.wireOp",EDGE,"E11"),sQuery(id+"F0.wireOp",EDGE,"E12"),sQuery(id+"F0.wireOp",EDGE,"E13"),sQuery(id+"F0.wireOp",EDGE,"E14"),sQuery(id+"F0.wireOp",EDGE,"E15"),sQuery(id+"F0.wireOp",EDGE,"E16"),sQuery(id+"F0.wireOp",EDGE,"E17"),sQuery(id+"F0.wireOp",EDGE,"E18"),sQuery(id+"F0.wireOp",EDGE,"E19"),sQuery(id+"F0.wireOp",EDGE,"E20"),sQuery(id+"F33.wireOp",EDGE,"E66"),sQuery(id+"F33.wireOp",EDGE,"E68"),sQuery(id+"F33.wireOp",EDGE,"E69"),sQuery(id+"F33.wireOp",EDGE,"E70"),sQuery(id+"F33.wireOp",EDGE,"E71"),sQuery(id+"F33.wireOp",EDGE,"E72.MirrorCS"),sQuery(id+"F33.wireOp",EDGE,"E73.MirrorCS"),sQuery(id+"F33.wireOp",EDGE,"E74.MirrorCS"),sQuery(id+"F33.wireOp",EDGE,"E75.MirrorCS"),sQuery(id+"F33.wireOp",EDGE,"E77.MirrorCS")])]})});
            var Q52;
            Q52=makeQuery(id+"F35.opBoolean","SPLIT",BODY,{"disambiguationData":[OD(55.0)],"derivedFrom":makeQuery(id+"F34.opExtrude","SWEPT_BODY",BODY,{"disambiguationData":[OSD([sQuery(id+"F0.wireOp",EDGE,"E0.bottom"),sQuery(id+"F0.wireOp",EDGE,"E0.left"),sQuery(id+"F0.wireOp",EDGE,"E0.right"),sQuery(id+"F0.wireOp",EDGE,"E1"),sQuery(id+"F0.wireOp",EDGE,"E2"),sQuery(id+"F0.wireOp",EDGE,"E3"),sQuery(id+"F0.wireOp",EDGE,"E4"),sQuery(id+"F0.wireOp",EDGE,"E5"),sQuery(id+"F0.wireOp",EDGE,"E6"),sQuery(id+"F0.wireOp",EDGE,"E7"),sQuery(id+"F0.wireOp",EDGE,"E8"),sQuery(id+"F0.wireOp",EDGE,"E9"),sQuery(id+"F0.wireOp",EDGE,"E10"),sQuery(id+"F0.wireOp",EDGE,"E11"),sQuery(id+"F0.wireOp",EDGE,"E12"),sQuery(id+"F0.wireOp",EDGE,"E13"),sQuery(id+"F0.wireOp",EDGE,"E14"),sQuery(id+"F0.wireOp",EDGE,"E15"),sQuery(id+"F0.wireOp",EDGE,"E16"),sQuery(id+"F0.wireOp",EDGE,"E17"),sQuery(id+"F0.wireOp",EDGE,"E18"),sQuery(id+"F0.wireOp",EDGE,"E19"),sQuery(id+"F0.wireOp",EDGE,"E20"),sQuery(id+"F33.wireOp",EDGE,"E66"),sQuery(id+"F33.wireOp",EDGE,"E68"),sQuery(id+"F33.wireOp",EDGE,"E69"),sQuery(id+"F33.wireOp",EDGE,"E70"),sQuery(id+"F33.wireOp",EDGE,"E71"),sQuery(id+"F33.wireOp",EDGE,"E72.MirrorCS"),sQuery(id+"F33.wireOp",EDGE,"E73.MirrorCS"),sQuery(id+"F33.wireOp",EDGE,"E74.MirrorCS"),sQuery(id+"F33.wireOp",EDGE,"E75.MirrorCS"),sQuery(id+"F33.wireOp",EDGE,"E77.MirrorCS")])]})});
            var Q53;
            Q53=makeQuery(id+"F35.opBoolean","SPLIT",BODY,{"disambiguationData":[OD(58.0)],"derivedFrom":makeQuery(id+"F34.opExtrude","SWEPT_BODY",BODY,{"disambiguationData":[OSD([sQuery(id+"F0.wireOp",EDGE,"E0.bottom"),sQuery(id+"F0.wireOp",EDGE,"E0.left"),sQuery(id+"F0.wireOp",EDGE,"E0.right"),sQuery(id+"F0.wireOp",EDGE,"E1"),sQuery(id+"F0.wireOp",EDGE,"E2"),sQuery(id+"F0.wireOp",EDGE,"E3"),sQuery(id+"F0.wireOp",EDGE,"E4"),sQuery(id+"F0.wireOp",EDGE,"E5"),sQuery(id+"F0.wireOp",EDGE,"E6"),sQuery(id+"F0.wireOp",EDGE,"E7"),sQuery(id+"F0.wireOp",EDGE,"E8"),sQuery(id+"F0.wireOp",EDGE,"E9"),sQuery(id+"F0.wireOp",EDGE,"E10"),sQuery(id+"F0.wireOp",EDGE,"E11"),sQuery(id+"F0.wireOp",EDGE,"E12"),sQuery(id+"F0.wireOp",EDGE,"E13"),sQuery(id+"F0.wireOp",EDGE,"E14"),sQuery(id+"F0.wireOp",EDGE,"E15"),sQuery(id+"F0.wireOp",EDGE,"E16"),sQuery(id+"F0.wireOp",EDGE,"E17"),sQuery(id+"F0.wireOp",EDGE,"E18"),sQuery(id+"F0.wireOp",EDGE,"E19"),sQuery(id+"F0.wireOp",EDGE,"E20"),sQuery(id+"F33.wireOp",EDGE,"E66"),sQuery(id+"F33.wireOp",EDGE,"E68"),sQuery(id+"F33.wireOp",EDGE,"E69"),sQuery(id+"F33.wireOp",EDGE,"E70"),sQuery(id+"F33.wireOp",EDGE,"E71"),sQuery(id+"F33.wireOp",EDGE,"E72.MirrorCS"),sQuery(id+"F33.wireOp",EDGE,"E73.MirrorCS"),sQuery(id+"F33.wireOp",EDGE,"E74.MirrorCS"),sQuery(id+"F33.wireOp",EDGE,"E75.MirrorCS"),sQuery(id+"F33.wireOp",EDGE,"E77.MirrorCS")])]})});
            var Q54;
            Q54=makeQuery(id+"F35.opBoolean","SPLIT",BODY,{"disambiguationData":[OD(59.0)],"derivedFrom":makeQuery(id+"F34.opExtrude","SWEPT_BODY",BODY,{"disambiguationData":[OSD([sQuery(id+"F0.wireOp",EDGE,"E0.bottom"),sQuery(id+"F0.wireOp",EDGE,"E0.left"),sQuery(id+"F0.wireOp",EDGE,"E0.right"),sQuery(id+"F0.wireOp",EDGE,"E1"),sQuery(id+"F0.wireOp",EDGE,"E2"),sQuery(id+"F0.wireOp",EDGE,"E3"),sQuery(id+"F0.wireOp",EDGE,"E4"),sQuery(id+"F0.wireOp",EDGE,"E5"),sQuery(id+"F0.wireOp",EDGE,"E6"),sQuery(id+"F0.wireOp",EDGE,"E7"),sQuery(id+"F0.wireOp",EDGE,"E8"),sQuery(id+"F0.wireOp",EDGE,"E9"),sQuery(id+"F0.wireOp",EDGE,"E10"),sQuery(id+"F0.wireOp",EDGE,"E11"),sQuery(id+"F0.wireOp",EDGE,"E12"),sQuery(id+"F0.wireOp",EDGE,"E13"),sQuery(id+"F0.wireOp",EDGE,"E14"),sQuery(id+"F0.wireOp",EDGE,"E15"),sQuery(id+"F0.wireOp",EDGE,"E16"),sQuery(id+"F0.wireOp",EDGE,"E17"),sQuery(id+"F0.wireOp",EDGE,"E18"),sQuery(id+"F0.wireOp",EDGE,"E19"),sQuery(id+"F0.wireOp",EDGE,"E20"),sQuery(id+"F33.wireOp",EDGE,"E66"),sQuery(id+"F33.wireOp",EDGE,"E68"),sQuery(id+"F33.wireOp",EDGE,"E69"),sQuery(id+"F33.wireOp",EDGE,"E70"),sQuery(id+"F33.wireOp",EDGE,"E71"),sQuery(id+"F33.wireOp",EDGE,"E72.MirrorCS"),sQuery(id+"F33.wireOp",EDGE,"E73.MirrorCS"),sQuery(id+"F33.wireOp",EDGE,"E74.MirrorCS"),sQuery(id+"F33.wireOp",EDGE,"E75.MirrorCS"),sQuery(id+"F33.wireOp",EDGE,"E77.MirrorCS")])]})});
            var Q55;
            Q55=makeQuery(id+"F35.opBoolean","SPLIT",BODY,{"disambiguationData":[OD(60.0)],"derivedFrom":makeQuery(id+"F34.opExtrude","SWEPT_BODY",BODY,{"disambiguationData":[OSD([sQuery(id+"F0.wireOp",EDGE,"E0.bottom"),sQuery(id+"F0.wireOp",EDGE,"E0.left"),sQuery(id+"F0.wireOp",EDGE,"E0.right"),sQuery(id+"F0.wireOp",EDGE,"E1"),sQuery(id+"F0.wireOp",EDGE,"E2"),sQuery(id+"F0.wireOp",EDGE,"E3"),sQuery(id+"F0.wireOp",EDGE,"E4"),sQuery(id+"F0.wireOp",EDGE,"E5"),sQuery(id+"F0.wireOp",EDGE,"E6"),sQuery(id+"F0.wireOp",EDGE,"E7"),sQuery(id+"F0.wireOp",EDGE,"E8"),sQuery(id+"F0.wireOp",EDGE,"E9"),sQuery(id+"F0.wireOp",EDGE,"E10"),sQuery(id+"F0.wireOp",EDGE,"E11"),sQuery(id+"F0.wireOp",EDGE,"E12"),sQuery(id+"F0.wireOp",EDGE,"E13"),sQuery(id+"F0.wireOp",EDGE,"E14"),sQuery(id+"F0.wireOp",EDGE,"E15"),sQuery(id+"F0.wireOp",EDGE,"E16"),sQuery(id+"F0.wireOp",EDGE,"E17"),sQuery(id+"F0.wireOp",EDGE,"E18"),sQuery(id+"F0.wireOp",EDGE,"E19"),sQuery(id+"F0.wireOp",EDGE,"E20"),sQuery(id+"F33.wireOp",EDGE,"E66"),sQuery(id+"F33.wireOp",EDGE,"E68"),sQuery(id+"F33.wireOp",EDGE,"E69"),sQuery(id+"F33.wireOp",EDGE,"E70"),sQuery(id+"F33.wireOp",EDGE,"E71"),sQuery(id+"F33.wireOp",EDGE,"E72.MirrorCS"),sQuery(id+"F33.wireOp",EDGE,"E73.MirrorCS"),sQuery(id+"F33.wireOp",EDGE,"E74.MirrorCS"),sQuery(id+"F33.wireOp",EDGE,"E75.MirrorCS"),sQuery(id+"F33.wireOp",EDGE,"E77.MirrorCS")])]})});
            var Q56;
            Q56=makeQuery(id+"F35.opBoolean","SPLIT",BODY,{"disambiguationData":[OD(61.0)],"derivedFrom":makeQuery(id+"F34.opExtrude","SWEPT_BODY",BODY,{"disambiguationData":[OSD([sQuery(id+"F0.wireOp",EDGE,"E0.bottom"),sQuery(id+"F0.wireOp",EDGE,"E0.left"),sQuery(id+"F0.wireOp",EDGE,"E0.right"),sQuery(id+"F0.wireOp",EDGE,"E1"),sQuery(id+"F0.wireOp",EDGE,"E2"),sQuery(id+"F0.wireOp",EDGE,"E3"),sQuery(id+"F0.wireOp",EDGE,"E4"),sQuery(id+"F0.wireOp",EDGE,"E5"),sQuery(id+"F0.wireOp",EDGE,"E6"),sQuery(id+"F0.wireOp",EDGE,"E7"),sQuery(id+"F0.wireOp",EDGE,"E8"),sQuery(id+"F0.wireOp",EDGE,"E9"),sQuery(id+"F0.wireOp",EDGE,"E10"),sQuery(id+"F0.wireOp",EDGE,"E11"),sQuery(id+"F0.wireOp",EDGE,"E12"),sQuery(id+"F0.wireOp",EDGE,"E13"),sQuery(id+"F0.wireOp",EDGE,"E14"),sQuery(id+"F0.wireOp",EDGE,"E15"),sQuery(id+"F0.wireOp",EDGE,"E16"),sQuery(id+"F0.wireOp",EDGE,"E17"),sQuery(id+"F0.wireOp",EDGE,"E18"),sQuery(id+"F0.wireOp",EDGE,"E19"),sQuery(id+"F0.wireOp",EDGE,"E20"),sQuery(id+"F33.wireOp",EDGE,"E66"),sQuery(id+"F33.wireOp",EDGE,"E68"),sQuery(id+"F33.wireOp",EDGE,"E69"),sQuery(id+"F33.wireOp",EDGE,"E70"),sQuery(id+"F33.wireOp",EDGE,"E71"),sQuery(id+"F33.wireOp",EDGE,"E72.MirrorCS"),sQuery(id+"F33.wireOp",EDGE,"E73.MirrorCS"),sQuery(id+"F33.wireOp",EDGE,"E74.MirrorCS"),sQuery(id+"F33.wireOp",EDGE,"E75.MirrorCS"),sQuery(id+"F33.wireOp",EDGE,"E77.MirrorCS")])]})});
            var Q57;
            Q57=makeQuery(id+"F35.opBoolean","SPLIT",BODY,{"disambiguationData":[OD(62.0)],"derivedFrom":makeQuery(id+"F34.opExtrude","SWEPT_BODY",BODY,{"disambiguationData":[OSD([sQuery(id+"F0.wireOp",EDGE,"E0.bottom"),sQuery(id+"F0.wireOp",EDGE,"E0.left"),sQuery(id+"F0.wireOp",EDGE,"E0.right"),sQuery(id+"F0.wireOp",EDGE,"E1"),sQuery(id+"F0.wireOp",EDGE,"E2"),sQuery(id+"F0.wireOp",EDGE,"E3"),sQuery(id+"F0.wireOp",EDGE,"E4"),sQuery(id+"F0.wireOp",EDGE,"E5"),sQuery(id+"F0.wireOp",EDGE,"E6"),sQuery(id+"F0.wireOp",EDGE,"E7"),sQuery(id+"F0.wireOp",EDGE,"E8"),sQuery(id+"F0.wireOp",EDGE,"E9"),sQuery(id+"F0.wireOp",EDGE,"E10"),sQuery(id+"F0.wireOp",EDGE,"E11"),sQuery(id+"F0.wireOp",EDGE,"E12"),sQuery(id+"F0.wireOp",EDGE,"E13"),sQuery(id+"F0.wireOp",EDGE,"E14"),sQuery(id+"F0.wireOp",EDGE,"E15"),sQuery(id+"F0.wireOp",EDGE,"E16"),sQuery(id+"F0.wireOp",EDGE,"E17"),sQuery(id+"F0.wireOp",EDGE,"E18"),sQuery(id+"F0.wireOp",EDGE,"E19"),sQuery(id+"F0.wireOp",EDGE,"E20"),sQuery(id+"F33.wireOp",EDGE,"E66"),sQuery(id+"F33.wireOp",EDGE,"E68"),sQuery(id+"F33.wireOp",EDGE,"E69"),sQuery(id+"F33.wireOp",EDGE,"E70"),sQuery(id+"F33.wireOp",EDGE,"E71"),sQuery(id+"F33.wireOp",EDGE,"E72.MirrorCS"),sQuery(id+"F33.wireOp",EDGE,"E73.MirrorCS"),sQuery(id+"F33.wireOp",EDGE,"E74.MirrorCS"),sQuery(id+"F33.wireOp",EDGE,"E75.MirrorCS"),sQuery(id+"F33.wireOp",EDGE,"E77.MirrorCS")])]})});
            var Q58;
            Q58=makeQuery(id+"F35.opBoolean","SPLIT",BODY,{"disambiguationData":[OD(63.0)],"derivedFrom":makeQuery(id+"F34.opExtrude","SWEPT_BODY",BODY,{"disambiguationData":[OSD([sQuery(id+"F0.wireOp",EDGE,"E0.bottom"),sQuery(id+"F0.wireOp",EDGE,"E0.left"),sQuery(id+"F0.wireOp",EDGE,"E0.right"),sQuery(id+"F0.wireOp",EDGE,"E1"),sQuery(id+"F0.wireOp",EDGE,"E2"),sQuery(id+"F0.wireOp",EDGE,"E3"),sQuery(id+"F0.wireOp",EDGE,"E4"),sQuery(id+"F0.wireOp",EDGE,"E5"),sQuery(id+"F0.wireOp",EDGE,"E6"),sQuery(id+"F0.wireOp",EDGE,"E7"),sQuery(id+"F0.wireOp",EDGE,"E8"),sQuery(id+"F0.wireOp",EDGE,"E9"),sQuery(id+"F0.wireOp",EDGE,"E10"),sQuery(id+"F0.wireOp",EDGE,"E11"),sQuery(id+"F0.wireOp",EDGE,"E12"),sQuery(id+"F0.wireOp",EDGE,"E13"),sQuery(id+"F0.wireOp",EDGE,"E14"),sQuery(id+"F0.wireOp",EDGE,"E15"),sQuery(id+"F0.wireOp",EDGE,"E16"),sQuery(id+"F0.wireOp",EDGE,"E17"),sQuery(id+"F0.wireOp",EDGE,"E18"),sQuery(id+"F0.wireOp",EDGE,"E19"),sQuery(id+"F0.wireOp",EDGE,"E20"),sQuery(id+"F33.wireOp",EDGE,"E66"),sQuery(id+"F33.wireOp",EDGE,"E68"),sQuery(id+"F33.wireOp",EDGE,"E69"),sQuery(id+"F33.wireOp",EDGE,"E70"),sQuery(id+"F33.wireOp",EDGE,"E71"),sQuery(id+"F33.wireOp",EDGE,"E72.MirrorCS"),sQuery(id+"F33.wireOp",EDGE,"E73.MirrorCS"),sQuery(id+"F33.wireOp",EDGE,"E74.MirrorCS"),sQuery(id+"F33.wireOp",EDGE,"E75.MirrorCS"),sQuery(id+"F33.wireOp",EDGE,"E77.MirrorCS")])]})});
            var Q59;
            Q59=makeQuery(id+"F35.opBoolean","SPLIT",BODY,{"disambiguationData":[OD(64.0)],"derivedFrom":makeQuery(id+"F34.opExtrude","SWEPT_BODY",BODY,{"disambiguationData":[OSD([sQuery(id+"F0.wireOp",EDGE,"E0.bottom"),sQuery(id+"F0.wireOp",EDGE,"E0.left"),sQuery(id+"F0.wireOp",EDGE,"E0.right"),sQuery(id+"F0.wireOp",EDGE,"E1"),sQuery(id+"F0.wireOp",EDGE,"E2"),sQuery(id+"F0.wireOp",EDGE,"E3"),sQuery(id+"F0.wireOp",EDGE,"E4"),sQuery(id+"F0.wireOp",EDGE,"E5"),sQuery(id+"F0.wireOp",EDGE,"E6"),sQuery(id+"F0.wireOp",EDGE,"E7"),sQuery(id+"F0.wireOp",EDGE,"E8"),sQuery(id+"F0.wireOp",EDGE,"E9"),sQuery(id+"F0.wireOp",EDGE,"E10"),sQuery(id+"F0.wireOp",EDGE,"E11"),sQuery(id+"F0.wireOp",EDGE,"E12"),sQuery(id+"F0.wireOp",EDGE,"E13"),sQuery(id+"F0.wireOp",EDGE,"E14"),sQuery(id+"F0.wireOp",EDGE,"E15"),sQuery(id+"F0.wireOp",EDGE,"E16"),sQuery(id+"F0.wireOp",EDGE,"E17"),sQuery(id+"F0.wireOp",EDGE,"E18"),sQuery(id+"F0.wireOp",EDGE,"E19"),sQuery(id+"F0.wireOp",EDGE,"E20"),sQuery(id+"F33.wireOp",EDGE,"E66"),sQuery(id+"F33.wireOp",EDGE,"E68"),sQuery(id+"F33.wireOp",EDGE,"E69"),sQuery(id+"F33.wireOp",EDGE,"E70"),sQuery(id+"F33.wireOp",EDGE,"E71"),sQuery(id+"F33.wireOp",EDGE,"E72.MirrorCS"),sQuery(id+"F33.wireOp",EDGE,"E73.MirrorCS"),sQuery(id+"F33.wireOp",EDGE,"E74.MirrorCS"),sQuery(id+"F33.wireOp",EDGE,"E75.MirrorCS"),sQuery(id+"F33.wireOp",EDGE,"E77.MirrorCS")])]})});
            var Q60;
            Q60=makeQuery(id+"F35.opBoolean","SPLIT",BODY,{"disambiguationData":[OD(66.0)],"derivedFrom":makeQuery(id+"F34.opExtrude","SWEPT_BODY",BODY,{"disambiguationData":[OSD([sQuery(id+"F0.wireOp",EDGE,"E0.bottom"),sQuery(id+"F0.wireOp",EDGE,"E0.left"),sQuery(id+"F0.wireOp",EDGE,"E0.right"),sQuery(id+"F0.wireOp",EDGE,"E1"),sQuery(id+"F0.wireOp",EDGE,"E2"),sQuery(id+"F0.wireOp",EDGE,"E3"),sQuery(id+"F0.wireOp",EDGE,"E4"),sQuery(id+"F0.wireOp",EDGE,"E5"),sQuery(id+"F0.wireOp",EDGE,"E6"),sQuery(id+"F0.wireOp",EDGE,"E7"),sQuery(id+"F0.wireOp",EDGE,"E8"),sQuery(id+"F0.wireOp",EDGE,"E9"),sQuery(id+"F0.wireOp",EDGE,"E10"),sQuery(id+"F0.wireOp",EDGE,"E11"),sQuery(id+"F0.wireOp",EDGE,"E12"),sQuery(id+"F0.wireOp",EDGE,"E13"),sQuery(id+"F0.wireOp",EDGE,"E14"),sQuery(id+"F0.wireOp",EDGE,"E15"),sQuery(id+"F0.wireOp",EDGE,"E16"),sQuery(id+"F0.wireOp",EDGE,"E17"),sQuery(id+"F0.wireOp",EDGE,"E18"),sQuery(id+"F0.wireOp",EDGE,"E19"),sQuery(id+"F0.wireOp",EDGE,"E20"),sQuery(id+"F33.wireOp",EDGE,"E66"),sQuery(id+"F33.wireOp",EDGE,"E68"),sQuery(id+"F33.wireOp",EDGE,"E69"),sQuery(id+"F33.wireOp",EDGE,"E70"),sQuery(id+"F33.wireOp",EDGE,"E71"),sQuery(id+"F33.wireOp",EDGE,"E72.MirrorCS"),sQuery(id+"F33.wireOp",EDGE,"E73.MirrorCS"),sQuery(id+"F33.wireOp",EDGE,"E74.MirrorCS"),sQuery(id+"F33.wireOp",EDGE,"E75.MirrorCS"),sQuery(id+"F33.wireOp",EDGE,"E77.MirrorCS")])]})});
            var Q61;
            Q61=makeQuery(id+"F35.opBoolean","SPLIT",BODY,{"disambiguationData":[OD(67.0)],"derivedFrom":makeQuery(id+"F34.opExtrude","SWEPT_BODY",BODY,{"disambiguationData":[OSD([sQuery(id+"F0.wireOp",EDGE,"E0.bottom"),sQuery(id+"F0.wireOp",EDGE,"E0.left"),sQuery(id+"F0.wireOp",EDGE,"E0.right"),sQuery(id+"F0.wireOp",EDGE,"E1"),sQuery(id+"F0.wireOp",EDGE,"E2"),sQuery(id+"F0.wireOp",EDGE,"E3"),sQuery(id+"F0.wireOp",EDGE,"E4"),sQuery(id+"F0.wireOp",EDGE,"E5"),sQuery(id+"F0.wireOp",EDGE,"E6"),sQuery(id+"F0.wireOp",EDGE,"E7"),sQuery(id+"F0.wireOp",EDGE,"E8"),sQuery(id+"F0.wireOp",EDGE,"E9"),sQuery(id+"F0.wireOp",EDGE,"E10"),sQuery(id+"F0.wireOp",EDGE,"E11"),sQuery(id+"F0.wireOp",EDGE,"E12"),sQuery(id+"F0.wireOp",EDGE,"E13"),sQuery(id+"F0.wireOp",EDGE,"E14"),sQuery(id+"F0.wireOp",EDGE,"E15"),sQuery(id+"F0.wireOp",EDGE,"E16"),sQuery(id+"F0.wireOp",EDGE,"E17"),sQuery(id+"F0.wireOp",EDGE,"E18"),sQuery(id+"F0.wireOp",EDGE,"E19"),sQuery(id+"F0.wireOp",EDGE,"E20"),sQuery(id+"F33.wireOp",EDGE,"E66"),sQuery(id+"F33.wireOp",EDGE,"E68"),sQuery(id+"F33.wireOp",EDGE,"E69"),sQuery(id+"F33.wireOp",EDGE,"E70"),sQuery(id+"F33.wireOp",EDGE,"E71"),sQuery(id+"F33.wireOp",EDGE,"E72.MirrorCS"),sQuery(id+"F33.wireOp",EDGE,"E73.MirrorCS"),sQuery(id+"F33.wireOp",EDGE,"E74.MirrorCS"),sQuery(id+"F33.wireOp",EDGE,"E75.MirrorCS"),sQuery(id+"F33.wireOp",EDGE,"E77.MirrorCS")])]})});
            var Q62;
            Q62=makeQuery(id+"F35.opBoolean","SPLIT",BODY,{"disambiguationData":[OD(68.0)],"derivedFrom":makeQuery(id+"F34.opExtrude","SWEPT_BODY",BODY,{"disambiguationData":[OSD([sQuery(id+"F0.wireOp",EDGE,"E0.bottom"),sQuery(id+"F0.wireOp",EDGE,"E0.left"),sQuery(id+"F0.wireOp",EDGE,"E0.right"),sQuery(id+"F0.wireOp",EDGE,"E1"),sQuery(id+"F0.wireOp",EDGE,"E2"),sQuery(id+"F0.wireOp",EDGE,"E3"),sQuery(id+"F0.wireOp",EDGE,"E4"),sQuery(id+"F0.wireOp",EDGE,"E5"),sQuery(id+"F0.wireOp",EDGE,"E6"),sQuery(id+"F0.wireOp",EDGE,"E7"),sQuery(id+"F0.wireOp",EDGE,"E8"),sQuery(id+"F0.wireOp",EDGE,"E9"),sQuery(id+"F0.wireOp",EDGE,"E10"),sQuery(id+"F0.wireOp",EDGE,"E11"),sQuery(id+"F0.wireOp",EDGE,"E12"),sQuery(id+"F0.wireOp",EDGE,"E13"),sQuery(id+"F0.wireOp",EDGE,"E14"),sQuery(id+"F0.wireOp",EDGE,"E15"),sQuery(id+"F0.wireOp",EDGE,"E16"),sQuery(id+"F0.wireOp",EDGE,"E17"),sQuery(id+"F0.wireOp",EDGE,"E18"),sQuery(id+"F0.wireOp",EDGE,"E19"),sQuery(id+"F0.wireOp",EDGE,"E20"),sQuery(id+"F33.wireOp",EDGE,"E66"),sQuery(id+"F33.wireOp",EDGE,"E68"),sQuery(id+"F33.wireOp",EDGE,"E69"),sQuery(id+"F33.wireOp",EDGE,"E70"),sQuery(id+"F33.wireOp",EDGE,"E71"),sQuery(id+"F33.wireOp",EDGE,"E72.MirrorCS"),sQuery(id+"F33.wireOp",EDGE,"E73.MirrorCS"),sQuery(id+"F33.wireOp",EDGE,"E74.MirrorCS"),sQuery(id+"F33.wireOp",EDGE,"E75.MirrorCS"),sQuery(id+"F33.wireOp",EDGE,"E77.MirrorCS")])]})});
            var Q63;
            Q63=makeQuery(id+"F35.opBoolean","SPLIT",BODY,{"disambiguationData":[OD(69.0)],"derivedFrom":makeQuery(id+"F34.opExtrude","SWEPT_BODY",BODY,{"disambiguationData":[OSD([sQuery(id+"F0.wireOp",EDGE,"E0.bottom"),sQuery(id+"F0.wireOp",EDGE,"E0.left"),sQuery(id+"F0.wireOp",EDGE,"E0.right"),sQuery(id+"F0.wireOp",EDGE,"E1"),sQuery(id+"F0.wireOp",EDGE,"E2"),sQuery(id+"F0.wireOp",EDGE,"E3"),sQuery(id+"F0.wireOp",EDGE,"E4"),sQuery(id+"F0.wireOp",EDGE,"E5"),sQuery(id+"F0.wireOp",EDGE,"E6"),sQuery(id+"F0.wireOp",EDGE,"E7"),sQuery(id+"F0.wireOp",EDGE,"E8"),sQuery(id+"F0.wireOp",EDGE,"E9"),sQuery(id+"F0.wireOp",EDGE,"E10"),sQuery(id+"F0.wireOp",EDGE,"E11"),sQuery(id+"F0.wireOp",EDGE,"E12"),sQuery(id+"F0.wireOp",EDGE,"E13"),sQuery(id+"F0.wireOp",EDGE,"E14"),sQuery(id+"F0.wireOp",EDGE,"E15"),sQuery(id+"F0.wireOp",EDGE,"E16"),sQuery(id+"F0.wireOp",EDGE,"E17"),sQuery(id+"F0.wireOp",EDGE,"E18"),sQuery(id+"F0.wireOp",EDGE,"E19"),sQuery(id+"F0.wireOp",EDGE,"E20"),sQuery(id+"F33.wireOp",EDGE,"E66"),sQuery(id+"F33.wireOp",EDGE,"E68"),sQuery(id+"F33.wireOp",EDGE,"E69"),sQuery(id+"F33.wireOp",EDGE,"E70"),sQuery(id+"F33.wireOp",EDGE,"E71"),sQuery(id+"F33.wireOp",EDGE,"E72.MirrorCS"),sQuery(id+"F33.wireOp",EDGE,"E73.MirrorCS"),sQuery(id+"F33.wireOp",EDGE,"E74.MirrorCS"),sQuery(id+"F33.wireOp",EDGE,"E75.MirrorCS"),sQuery(id+"F33.wireOp",EDGE,"E77.MirrorCS")])]})});
            var Q64;
            Q64=makeQuery(id+"F35.opBoolean","SPLIT",BODY,{"disambiguationData":[OD(70.0)],"derivedFrom":makeQuery(id+"F34.opExtrude","SWEPT_BODY",BODY,{"disambiguationData":[OSD([sQuery(id+"F0.wireOp",EDGE,"E0.bottom"),sQuery(id+"F0.wireOp",EDGE,"E0.left"),sQuery(id+"F0.wireOp",EDGE,"E0.right"),sQuery(id+"F0.wireOp",EDGE,"E1"),sQuery(id+"F0.wireOp",EDGE,"E2"),sQuery(id+"F0.wireOp",EDGE,"E3"),sQuery(id+"F0.wireOp",EDGE,"E4"),sQuery(id+"F0.wireOp",EDGE,"E5"),sQuery(id+"F0.wireOp",EDGE,"E6"),sQuery(id+"F0.wireOp",EDGE,"E7"),sQuery(id+"F0.wireOp",EDGE,"E8"),sQuery(id+"F0.wireOp",EDGE,"E9"),sQuery(id+"F0.wireOp",EDGE,"E10"),sQuery(id+"F0.wireOp",EDGE,"E11"),sQuery(id+"F0.wireOp",EDGE,"E12"),sQuery(id+"F0.wireOp",EDGE,"E13"),sQuery(id+"F0.wireOp",EDGE,"E14"),sQuery(id+"F0.wireOp",EDGE,"E15"),sQuery(id+"F0.wireOp",EDGE,"E16"),sQuery(id+"F0.wireOp",EDGE,"E17"),sQuery(id+"F0.wireOp",EDGE,"E18"),sQuery(id+"F0.wireOp",EDGE,"E19"),sQuery(id+"F0.wireOp",EDGE,"E20"),sQuery(id+"F33.wireOp",EDGE,"E66"),sQuery(id+"F33.wireOp",EDGE,"E68"),sQuery(id+"F33.wireOp",EDGE,"E69"),sQuery(id+"F33.wireOp",EDGE,"E70"),sQuery(id+"F33.wireOp",EDGE,"E71"),sQuery(id+"F33.wireOp",EDGE,"E72.MirrorCS"),sQuery(id+"F33.wireOp",EDGE,"E73.MirrorCS"),sQuery(id+"F33.wireOp",EDGE,"E74.MirrorCS"),sQuery(id+"F33.wireOp",EDGE,"E75.MirrorCS"),sQuery(id+"F33.wireOp",EDGE,"E77.MirrorCS")])]})});
            var Q65;
            Q65=makeQuery(id+"F35.opBoolean","SPLIT",BODY,{"disambiguationData":[OD(71.0)],"derivedFrom":makeQuery(id+"F34.opExtrude","SWEPT_BODY",BODY,{"disambiguationData":[OSD([sQuery(id+"F0.wireOp",EDGE,"E0.bottom"),sQuery(id+"F0.wireOp",EDGE,"E0.left"),sQuery(id+"F0.wireOp",EDGE,"E0.right"),sQuery(id+"F0.wireOp",EDGE,"E1"),sQuery(id+"F0.wireOp",EDGE,"E2"),sQuery(id+"F0.wireOp",EDGE,"E3"),sQuery(id+"F0.wireOp",EDGE,"E4"),sQuery(id+"F0.wireOp",EDGE,"E5"),sQuery(id+"F0.wireOp",EDGE,"E6"),sQuery(id+"F0.wireOp",EDGE,"E7"),sQuery(id+"F0.wireOp",EDGE,"E8"),sQuery(id+"F0.wireOp",EDGE,"E9"),sQuery(id+"F0.wireOp",EDGE,"E10"),sQuery(id+"F0.wireOp",EDGE,"E11"),sQuery(id+"F0.wireOp",EDGE,"E12"),sQuery(id+"F0.wireOp",EDGE,"E13"),sQuery(id+"F0.wireOp",EDGE,"E14"),sQuery(id+"F0.wireOp",EDGE,"E15"),sQuery(id+"F0.wireOp",EDGE,"E16"),sQuery(id+"F0.wireOp",EDGE,"E17"),sQuery(id+"F0.wireOp",EDGE,"E18"),sQuery(id+"F0.wireOp",EDGE,"E19"),sQuery(id+"F0.wireOp",EDGE,"E20"),sQuery(id+"F33.wireOp",EDGE,"E66"),sQuery(id+"F33.wireOp",EDGE,"E68"),sQuery(id+"F33.wireOp",EDGE,"E69"),sQuery(id+"F33.wireOp",EDGE,"E70"),sQuery(id+"F33.wireOp",EDGE,"E71"),sQuery(id+"F33.wireOp",EDGE,"E72.MirrorCS"),sQuery(id+"F33.wireOp",EDGE,"E73.MirrorCS"),sQuery(id+"F33.wireOp",EDGE,"E74.MirrorCS"),sQuery(id+"F33.wireOp",EDGE,"E75.MirrorCS"),sQuery(id+"F33.wireOp",EDGE,"E77.MirrorCS")])]})});
            var Q66;
            Q66=makeQuery(id+"F35.opBoolean","SPLIT",BODY,{"disambiguationData":[OD(72.0)],"derivedFrom":makeQuery(id+"F34.opExtrude","SWEPT_BODY",BODY,{"disambiguationData":[OSD([sQuery(id+"F0.wireOp",EDGE,"E0.bottom"),sQuery(id+"F0.wireOp",EDGE,"E0.left"),sQuery(id+"F0.wireOp",EDGE,"E0.right"),sQuery(id+"F0.wireOp",EDGE,"E1"),sQuery(id+"F0.wireOp",EDGE,"E2"),sQuery(id+"F0.wireOp",EDGE,"E3"),sQuery(id+"F0.wireOp",EDGE,"E4"),sQuery(id+"F0.wireOp",EDGE,"E5"),sQuery(id+"F0.wireOp",EDGE,"E6"),sQuery(id+"F0.wireOp",EDGE,"E7"),sQuery(id+"F0.wireOp",EDGE,"E8"),sQuery(id+"F0.wireOp",EDGE,"E9"),sQuery(id+"F0.wireOp",EDGE,"E10"),sQuery(id+"F0.wireOp",EDGE,"E11"),sQuery(id+"F0.wireOp",EDGE,"E12"),sQuery(id+"F0.wireOp",EDGE,"E13"),sQuery(id+"F0.wireOp",EDGE,"E14"),sQuery(id+"F0.wireOp",EDGE,"E15"),sQuery(id+"F0.wireOp",EDGE,"E16"),sQuery(id+"F0.wireOp",EDGE,"E17"),sQuery(id+"F0.wireOp",EDGE,"E18"),sQuery(id+"F0.wireOp",EDGE,"E19"),sQuery(id+"F0.wireOp",EDGE,"E20"),sQuery(id+"F33.wireOp",EDGE,"E66"),sQuery(id+"F33.wireOp",EDGE,"E68"),sQuery(id+"F33.wireOp",EDGE,"E69"),sQuery(id+"F33.wireOp",EDGE,"E70"),sQuery(id+"F33.wireOp",EDGE,"E71"),sQuery(id+"F33.wireOp",EDGE,"E72.MirrorCS"),sQuery(id+"F33.wireOp",EDGE,"E73.MirrorCS"),sQuery(id+"F33.wireOp",EDGE,"E74.MirrorCS"),sQuery(id+"F33.wireOp",EDGE,"E75.MirrorCS"),sQuery(id+"F33.wireOp",EDGE,"E77.MirrorCS")])]})});
            var Q67;
            Q67=makeQuery(id+"F35.opBoolean","SPLIT",BODY,{"disambiguationData":[OD(73.0)],"derivedFrom":makeQuery(id+"F34.opExtrude","SWEPT_BODY",BODY,{"disambiguationData":[OSD([sQuery(id+"F0.wireOp",EDGE,"E0.bottom"),sQuery(id+"F0.wireOp",EDGE,"E0.left"),sQuery(id+"F0.wireOp",EDGE,"E0.right"),sQuery(id+"F0.wireOp",EDGE,"E1"),sQuery(id+"F0.wireOp",EDGE,"E2"),sQuery(id+"F0.wireOp",EDGE,"E3"),sQuery(id+"F0.wireOp",EDGE,"E4"),sQuery(id+"F0.wireOp",EDGE,"E5"),sQuery(id+"F0.wireOp",EDGE,"E6"),sQuery(id+"F0.wireOp",EDGE,"E7"),sQuery(id+"F0.wireOp",EDGE,"E8"),sQuery(id+"F0.wireOp",EDGE,"E9"),sQuery(id+"F0.wireOp",EDGE,"E10"),sQuery(id+"F0.wireOp",EDGE,"E11"),sQuery(id+"F0.wireOp",EDGE,"E12"),sQuery(id+"F0.wireOp",EDGE,"E13"),sQuery(id+"F0.wireOp",EDGE,"E14"),sQuery(id+"F0.wireOp",EDGE,"E15"),sQuery(id+"F0.wireOp",EDGE,"E16"),sQuery(id+"F0.wireOp",EDGE,"E17"),sQuery(id+"F0.wireOp",EDGE,"E18"),sQuery(id+"F0.wireOp",EDGE,"E19"),sQuery(id+"F0.wireOp",EDGE,"E20"),sQuery(id+"F33.wireOp",EDGE,"E66"),sQuery(id+"F33.wireOp",EDGE,"E68"),sQuery(id+"F33.wireOp",EDGE,"E69"),sQuery(id+"F33.wireOp",EDGE,"E70"),sQuery(id+"F33.wireOp",EDGE,"E71"),sQuery(id+"F33.wireOp",EDGE,"E72.MirrorCS"),sQuery(id+"F33.wireOp",EDGE,"E73.MirrorCS"),sQuery(id+"F33.wireOp",EDGE,"E74.MirrorCS"),sQuery(id+"F33.wireOp",EDGE,"E75.MirrorCS"),sQuery(id+"F33.wireOp",EDGE,"E77.MirrorCS")])]})});
            var Q68;
            Q68=makeQuery(id+"F35.opBoolean","SPLIT",BODY,{"disambiguationData":[OD(74.0)],"derivedFrom":makeQuery(id+"F34.opExtrude","SWEPT_BODY",BODY,{"disambiguationData":[OSD([sQuery(id+"F0.wireOp",EDGE,"E0.bottom"),sQuery(id+"F0.wireOp",EDGE,"E0.left"),sQuery(id+"F0.wireOp",EDGE,"E0.right"),sQuery(id+"F0.wireOp",EDGE,"E1"),sQuery(id+"F0.wireOp",EDGE,"E2"),sQuery(id+"F0.wireOp",EDGE,"E3"),sQuery(id+"F0.wireOp",EDGE,"E4"),sQuery(id+"F0.wireOp",EDGE,"E5"),sQuery(id+"F0.wireOp",EDGE,"E6"),sQuery(id+"F0.wireOp",EDGE,"E7"),sQuery(id+"F0.wireOp",EDGE,"E8"),sQuery(id+"F0.wireOp",EDGE,"E9"),sQuery(id+"F0.wireOp",EDGE,"E10"),sQuery(id+"F0.wireOp",EDGE,"E11"),sQuery(id+"F0.wireOp",EDGE,"E12"),sQuery(id+"F0.wireOp",EDGE,"E13"),sQuery(id+"F0.wireOp",EDGE,"E14"),sQuery(id+"F0.wireOp",EDGE,"E15"),sQuery(id+"F0.wireOp",EDGE,"E16"),sQuery(id+"F0.wireOp",EDGE,"E17"),sQuery(id+"F0.wireOp",EDGE,"E18"),sQuery(id+"F0.wireOp",EDGE,"E19"),sQuery(id+"F0.wireOp",EDGE,"E20"),sQuery(id+"F33.wireOp",EDGE,"E66"),sQuery(id+"F33.wireOp",EDGE,"E68"),sQuery(id+"F33.wireOp",EDGE,"E69"),sQuery(id+"F33.wireOp",EDGE,"E70"),sQuery(id+"F33.wireOp",EDGE,"E71"),sQuery(id+"F33.wireOp",EDGE,"E72.MirrorCS"),sQuery(id+"F33.wireOp",EDGE,"E73.MirrorCS"),sQuery(id+"F33.wireOp",EDGE,"E74.MirrorCS"),sQuery(id+"F33.wireOp",EDGE,"E75.MirrorCS"),sQuery(id+"F33.wireOp",EDGE,"E77.MirrorCS")])]})});
            var Q69;
            Q69=makeQuery(id+"F35.opBoolean","SPLIT",BODY,{"disambiguationData":[OD(76.0)],"derivedFrom":makeQuery(id+"F34.opExtrude","SWEPT_BODY",BODY,{"disambiguationData":[OSD([sQuery(id+"F0.wireOp",EDGE,"E0.bottom"),sQuery(id+"F0.wireOp",EDGE,"E0.left"),sQuery(id+"F0.wireOp",EDGE,"E0.right"),sQuery(id+"F0.wireOp",EDGE,"E1"),sQuery(id+"F0.wireOp",EDGE,"E2"),sQuery(id+"F0.wireOp",EDGE,"E3"),sQuery(id+"F0.wireOp",EDGE,"E4"),sQuery(id+"F0.wireOp",EDGE,"E5"),sQuery(id+"F0.wireOp",EDGE,"E6"),sQuery(id+"F0.wireOp",EDGE,"E7"),sQuery(id+"F0.wireOp",EDGE,"E8"),sQuery(id+"F0.wireOp",EDGE,"E9"),sQuery(id+"F0.wireOp",EDGE,"E10"),sQuery(id+"F0.wireOp",EDGE,"E11"),sQuery(id+"F0.wireOp",EDGE,"E12"),sQuery(id+"F0.wireOp",EDGE,"E13"),sQuery(id+"F0.wireOp",EDGE,"E14"),sQuery(id+"F0.wireOp",EDGE,"E15"),sQuery(id+"F0.wireOp",EDGE,"E16"),sQuery(id+"F0.wireOp",EDGE,"E17"),sQuery(id+"F0.wireOp",EDGE,"E18"),sQuery(id+"F0.wireOp",EDGE,"E19"),sQuery(id+"F0.wireOp",EDGE,"E20"),sQuery(id+"F33.wireOp",EDGE,"E66"),sQuery(id+"F33.wireOp",EDGE,"E68"),sQuery(id+"F33.wireOp",EDGE,"E69"),sQuery(id+"F33.wireOp",EDGE,"E70"),sQuery(id+"F33.wireOp",EDGE,"E71"),sQuery(id+"F33.wireOp",EDGE,"E72.MirrorCS"),sQuery(id+"F33.wireOp",EDGE,"E73.MirrorCS"),sQuery(id+"F33.wireOp",EDGE,"E74.MirrorCS"),sQuery(id+"F33.wireOp",EDGE,"E75.MirrorCS"),sQuery(id+"F33.wireOp",EDGE,"E77.MirrorCS")])]})});
            var Q70;
            Q70=makeQuery(id+"F35.opBoolean","SPLIT",BODY,{"disambiguationData":[OD(77.0)],"derivedFrom":makeQuery(id+"F34.opExtrude","SWEPT_BODY",BODY,{"disambiguationData":[OSD([sQuery(id+"F0.wireOp",EDGE,"E0.bottom"),sQuery(id+"F0.wireOp",EDGE,"E0.left"),sQuery(id+"F0.wireOp",EDGE,"E0.right"),sQuery(id+"F0.wireOp",EDGE,"E1"),sQuery(id+"F0.wireOp",EDGE,"E2"),sQuery(id+"F0.wireOp",EDGE,"E3"),sQuery(id+"F0.wireOp",EDGE,"E4"),sQuery(id+"F0.wireOp",EDGE,"E5"),sQuery(id+"F0.wireOp",EDGE,"E6"),sQuery(id+"F0.wireOp",EDGE,"E7"),sQuery(id+"F0.wireOp",EDGE,"E8"),sQuery(id+"F0.wireOp",EDGE,"E9"),sQuery(id+"F0.wireOp",EDGE,"E10"),sQuery(id+"F0.wireOp",EDGE,"E11"),sQuery(id+"F0.wireOp",EDGE,"E12"),sQuery(id+"F0.wireOp",EDGE,"E13"),sQuery(id+"F0.wireOp",EDGE,"E14"),sQuery(id+"F0.wireOp",EDGE,"E15"),sQuery(id+"F0.wireOp",EDGE,"E16"),sQuery(id+"F0.wireOp",EDGE,"E17"),sQuery(id+"F0.wireOp",EDGE,"E18"),sQuery(id+"F0.wireOp",EDGE,"E19"),sQuery(id+"F0.wireOp",EDGE,"E20"),sQuery(id+"F33.wireOp",EDGE,"E66"),sQuery(id+"F33.wireOp",EDGE,"E68"),sQuery(id+"F33.wireOp",EDGE,"E69"),sQuery(id+"F33.wireOp",EDGE,"E70"),sQuery(id+"F33.wireOp",EDGE,"E71"),sQuery(id+"F33.wireOp",EDGE,"E72.MirrorCS"),sQuery(id+"F33.wireOp",EDGE,"E73.MirrorCS"),sQuery(id+"F33.wireOp",EDGE,"E74.MirrorCS"),sQuery(id+"F33.wireOp",EDGE,"E75.MirrorCS"),sQuery(id+"F33.wireOp",EDGE,"E77.MirrorCS")])]})});
            var Q71;
            Q71=makeQuery(id+"F35.opBoolean","SPLIT",BODY,{"disambiguationData":[OD(78.0)],"derivedFrom":makeQuery(id+"F34.opExtrude","SWEPT_BODY",BODY,{"disambiguationData":[OSD([sQuery(id+"F0.wireOp",EDGE,"E0.bottom"),sQuery(id+"F0.wireOp",EDGE,"E0.left"),sQuery(id+"F0.wireOp",EDGE,"E0.right"),sQuery(id+"F0.wireOp",EDGE,"E1"),sQuery(id+"F0.wireOp",EDGE,"E2"),sQuery(id+"F0.wireOp",EDGE,"E3"),sQuery(id+"F0.wireOp",EDGE,"E4"),sQuery(id+"F0.wireOp",EDGE,"E5"),sQuery(id+"F0.wireOp",EDGE,"E6"),sQuery(id+"F0.wireOp",EDGE,"E7"),sQuery(id+"F0.wireOp",EDGE,"E8"),sQuery(id+"F0.wireOp",EDGE,"E9"),sQuery(id+"F0.wireOp",EDGE,"E10"),sQuery(id+"F0.wireOp",EDGE,"E11"),sQuery(id+"F0.wireOp",EDGE,"E12"),sQuery(id+"F0.wireOp",EDGE,"E13"),sQuery(id+"F0.wireOp",EDGE,"E14"),sQuery(id+"F0.wireOp",EDGE,"E15"),sQuery(id+"F0.wireOp",EDGE,"E16"),sQuery(id+"F0.wireOp",EDGE,"E17"),sQuery(id+"F0.wireOp",EDGE,"E18"),sQuery(id+"F0.wireOp",EDGE,"E19"),sQuery(id+"F0.wireOp",EDGE,"E20"),sQuery(id+"F33.wireOp",EDGE,"E66"),sQuery(id+"F33.wireOp",EDGE,"E68"),sQuery(id+"F33.wireOp",EDGE,"E69"),sQuery(id+"F33.wireOp",EDGE,"E70"),sQuery(id+"F33.wireOp",EDGE,"E71"),sQuery(id+"F33.wireOp",EDGE,"E72.MirrorCS"),sQuery(id+"F33.wireOp",EDGE,"E73.MirrorCS"),sQuery(id+"F33.wireOp",EDGE,"E74.MirrorCS"),sQuery(id+"F33.wireOp",EDGE,"E75.MirrorCS"),sQuery(id+"F33.wireOp",EDGE,"E77.MirrorCS")])]})});
            var Q72;
            Q72=makeQuery(id+"F35.opBoolean","SPLIT",BODY,{"disambiguationData":[OD(79.0)],"derivedFrom":makeQuery(id+"F34.opExtrude","SWEPT_BODY",BODY,{"disambiguationData":[OSD([sQuery(id+"F0.wireOp",EDGE,"E0.bottom"),sQuery(id+"F0.wireOp",EDGE,"E0.left"),sQuery(id+"F0.wireOp",EDGE,"E0.right"),sQuery(id+"F0.wireOp",EDGE,"E1"),sQuery(id+"F0.wireOp",EDGE,"E2"),sQuery(id+"F0.wireOp",EDGE,"E3"),sQuery(id+"F0.wireOp",EDGE,"E4"),sQuery(id+"F0.wireOp",EDGE,"E5"),sQuery(id+"F0.wireOp",EDGE,"E6"),sQuery(id+"F0.wireOp",EDGE,"E7"),sQuery(id+"F0.wireOp",EDGE,"E8"),sQuery(id+"F0.wireOp",EDGE,"E9"),sQuery(id+"F0.wireOp",EDGE,"E10"),sQuery(id+"F0.wireOp",EDGE,"E11"),sQuery(id+"F0.wireOp",EDGE,"E12"),sQuery(id+"F0.wireOp",EDGE,"E13"),sQuery(id+"F0.wireOp",EDGE,"E14"),sQuery(id+"F0.wireOp",EDGE,"E15"),sQuery(id+"F0.wireOp",EDGE,"E16"),sQuery(id+"F0.wireOp",EDGE,"E17"),sQuery(id+"F0.wireOp",EDGE,"E18"),sQuery(id+"F0.wireOp",EDGE,"E19"),sQuery(id+"F0.wireOp",EDGE,"E20"),sQuery(id+"F33.wireOp",EDGE,"E66"),sQuery(id+"F33.wireOp",EDGE,"E68"),sQuery(id+"F33.wireOp",EDGE,"E69"),sQuery(id+"F33.wireOp",EDGE,"E70"),sQuery(id+"F33.wireOp",EDGE,"E71"),sQuery(id+"F33.wireOp",EDGE,"E72.MirrorCS"),sQuery(id+"F33.wireOp",EDGE,"E73.MirrorCS"),sQuery(id+"F33.wireOp",EDGE,"E74.MirrorCS"),sQuery(id+"F33.wireOp",EDGE,"E75.MirrorCS"),sQuery(id+"F33.wireOp",EDGE,"E77.MirrorCS")])]})});
            var Q73;
            Q73=makeQuery(id+"F35.opBoolean","SPLIT",BODY,{"disambiguationData":[OD(80.0)],"derivedFrom":makeQuery(id+"F34.opExtrude","SWEPT_BODY",BODY,{"disambiguationData":[OSD([sQuery(id+"F0.wireOp",EDGE,"E0.bottom"),sQuery(id+"F0.wireOp",EDGE,"E0.left"),sQuery(id+"F0.wireOp",EDGE,"E0.right"),sQuery(id+"F0.wireOp",EDGE,"E1"),sQuery(id+"F0.wireOp",EDGE,"E2"),sQuery(id+"F0.wireOp",EDGE,"E3"),sQuery(id+"F0.wireOp",EDGE,"E4"),sQuery(id+"F0.wireOp",EDGE,"E5"),sQuery(id+"F0.wireOp",EDGE,"E6"),sQuery(id+"F0.wireOp",EDGE,"E7"),sQuery(id+"F0.wireOp",EDGE,"E8"),sQuery(id+"F0.wireOp",EDGE,"E9"),sQuery(id+"F0.wireOp",EDGE,"E10"),sQuery(id+"F0.wireOp",EDGE,"E11"),sQuery(id+"F0.wireOp",EDGE,"E12"),sQuery(id+"F0.wireOp",EDGE,"E13"),sQuery(id+"F0.wireOp",EDGE,"E14"),sQuery(id+"F0.wireOp",EDGE,"E15"),sQuery(id+"F0.wireOp",EDGE,"E16"),sQuery(id+"F0.wireOp",EDGE,"E17"),sQuery(id+"F0.wireOp",EDGE,"E18"),sQuery(id+"F0.wireOp",EDGE,"E19"),sQuery(id+"F0.wireOp",EDGE,"E20"),sQuery(id+"F33.wireOp",EDGE,"E66"),sQuery(id+"F33.wireOp",EDGE,"E68"),sQuery(id+"F33.wireOp",EDGE,"E69"),sQuery(id+"F33.wireOp",EDGE,"E70"),sQuery(id+"F33.wireOp",EDGE,"E71"),sQuery(id+"F33.wireOp",EDGE,"E72.MirrorCS"),sQuery(id+"F33.wireOp",EDGE,"E73.MirrorCS"),sQuery(id+"F33.wireOp",EDGE,"E74.MirrorCS"),sQuery(id+"F33.wireOp",EDGE,"E75.MirrorCS"),sQuery(id+"F33.wireOp",EDGE,"E77.MirrorCS")])]})});
            var Q74;
            Q74=makeQuery(id+"F35.opBoolean","SPLIT",BODY,{"disambiguationData":[OD(81.0)],"derivedFrom":makeQuery(id+"F34.opExtrude","SWEPT_BODY",BODY,{"disambiguationData":[OSD([sQuery(id+"F0.wireOp",EDGE,"E0.bottom"),sQuery(id+"F0.wireOp",EDGE,"E0.left"),sQuery(id+"F0.wireOp",EDGE,"E0.right"),sQuery(id+"F0.wireOp",EDGE,"E1"),sQuery(id+"F0.wireOp",EDGE,"E2"),sQuery(id+"F0.wireOp",EDGE,"E3"),sQuery(id+"F0.wireOp",EDGE,"E4"),sQuery(id+"F0.wireOp",EDGE,"E5"),sQuery(id+"F0.wireOp",EDGE,"E6"),sQuery(id+"F0.wireOp",EDGE,"E7"),sQuery(id+"F0.wireOp",EDGE,"E8"),sQuery(id+"F0.wireOp",EDGE,"E9"),sQuery(id+"F0.wireOp",EDGE,"E10"),sQuery(id+"F0.wireOp",EDGE,"E11"),sQuery(id+"F0.wireOp",EDGE,"E12"),sQuery(id+"F0.wireOp",EDGE,"E13"),sQuery(id+"F0.wireOp",EDGE,"E14"),sQuery(id+"F0.wireOp",EDGE,"E15"),sQuery(id+"F0.wireOp",EDGE,"E16"),sQuery(id+"F0.wireOp",EDGE,"E17"),sQuery(id+"F0.wireOp",EDGE,"E18"),sQuery(id+"F0.wireOp",EDGE,"E19"),sQuery(id+"F0.wireOp",EDGE,"E20"),sQuery(id+"F33.wireOp",EDGE,"E66"),sQuery(id+"F33.wireOp",EDGE,"E68"),sQuery(id+"F33.wireOp",EDGE,"E69"),sQuery(id+"F33.wireOp",EDGE,"E70"),sQuery(id+"F33.wireOp",EDGE,"E71"),sQuery(id+"F33.wireOp",EDGE,"E72.MirrorCS"),sQuery(id+"F33.wireOp",EDGE,"E73.MirrorCS"),sQuery(id+"F33.wireOp",EDGE,"E74.MirrorCS"),sQuery(id+"F33.wireOp",EDGE,"E75.MirrorCS"),sQuery(id+"F33.wireOp",EDGE,"E77.MirrorCS")])]})});
            var Q75;
            Q75=makeQuery(id+"F35.opBoolean","SPLIT",BODY,{"disambiguationData":[OD(82.0)],"derivedFrom":makeQuery(id+"F34.opExtrude","SWEPT_BODY",BODY,{"disambiguationData":[OSD([sQuery(id+"F0.wireOp",EDGE,"E0.bottom"),sQuery(id+"F0.wireOp",EDGE,"E0.left"),sQuery(id+"F0.wireOp",EDGE,"E0.right"),sQuery(id+"F0.wireOp",EDGE,"E1"),sQuery(id+"F0.wireOp",EDGE,"E2"),sQuery(id+"F0.wireOp",EDGE,"E3"),sQuery(id+"F0.wireOp",EDGE,"E4"),sQuery(id+"F0.wireOp",EDGE,"E5"),sQuery(id+"F0.wireOp",EDGE,"E6"),sQuery(id+"F0.wireOp",EDGE,"E7"),sQuery(id+"F0.wireOp",EDGE,"E8"),sQuery(id+"F0.wireOp",EDGE,"E9"),sQuery(id+"F0.wireOp",EDGE,"E10"),sQuery(id+"F0.wireOp",EDGE,"E11"),sQuery(id+"F0.wireOp",EDGE,"E12"),sQuery(id+"F0.wireOp",EDGE,"E13"),sQuery(id+"F0.wireOp",EDGE,"E14"),sQuery(id+"F0.wireOp",EDGE,"E15"),sQuery(id+"F0.wireOp",EDGE,"E16"),sQuery(id+"F0.wireOp",EDGE,"E17"),sQuery(id+"F0.wireOp",EDGE,"E18"),sQuery(id+"F0.wireOp",EDGE,"E19"),sQuery(id+"F0.wireOp",EDGE,"E20"),sQuery(id+"F33.wireOp",EDGE,"E66"),sQuery(id+"F33.wireOp",EDGE,"E68"),sQuery(id+"F33.wireOp",EDGE,"E69"),sQuery(id+"F33.wireOp",EDGE,"E70"),sQuery(id+"F33.wireOp",EDGE,"E71"),sQuery(id+"F33.wireOp",EDGE,"E72.MirrorCS"),sQuery(id+"F33.wireOp",EDGE,"E73.MirrorCS"),sQuery(id+"F33.wireOp",EDGE,"E74.MirrorCS"),sQuery(id+"F33.wireOp",EDGE,"E75.MirrorCS"),sQuery(id+"F33.wireOp",EDGE,"E77.MirrorCS")])]})});
            var Q76;
            Q76=makeQuery(id+"F35.opBoolean","SPLIT",BODY,{"disambiguationData":[OD(83.0)],"derivedFrom":makeQuery(id+"F34.opExtrude","SWEPT_BODY",BODY,{"disambiguationData":[OSD([sQuery(id+"F0.wireOp",EDGE,"E0.bottom"),sQuery(id+"F0.wireOp",EDGE,"E0.left"),sQuery(id+"F0.wireOp",EDGE,"E0.right"),sQuery(id+"F0.wireOp",EDGE,"E1"),sQuery(id+"F0.wireOp",EDGE,"E2"),sQuery(id+"F0.wireOp",EDGE,"E3"),sQuery(id+"F0.wireOp",EDGE,"E4"),sQuery(id+"F0.wireOp",EDGE,"E5"),sQuery(id+"F0.wireOp",EDGE,"E6"),sQuery(id+"F0.wireOp",EDGE,"E7"),sQuery(id+"F0.wireOp",EDGE,"E8"),sQuery(id+"F0.wireOp",EDGE,"E9"),sQuery(id+"F0.wireOp",EDGE,"E10"),sQuery(id+"F0.wireOp",EDGE,"E11"),sQuery(id+"F0.wireOp",EDGE,"E12"),sQuery(id+"F0.wireOp",EDGE,"E13"),sQuery(id+"F0.wireOp",EDGE,"E14"),sQuery(id+"F0.wireOp",EDGE,"E15"),sQuery(id+"F0.wireOp",EDGE,"E16"),sQuery(id+"F0.wireOp",EDGE,"E17"),sQuery(id+"F0.wireOp",EDGE,"E18"),sQuery(id+"F0.wireOp",EDGE,"E19"),sQuery(id+"F0.wireOp",EDGE,"E20"),sQuery(id+"F33.wireOp",EDGE,"E66"),sQuery(id+"F33.wireOp",EDGE,"E68"),sQuery(id+"F33.wireOp",EDGE,"E69"),sQuery(id+"F33.wireOp",EDGE,"E70"),sQuery(id+"F33.wireOp",EDGE,"E71"),sQuery(id+"F33.wireOp",EDGE,"E72.MirrorCS"),sQuery(id+"F33.wireOp",EDGE,"E73.MirrorCS"),sQuery(id+"F33.wireOp",EDGE,"E74.MirrorCS"),sQuery(id+"F33.wireOp",EDGE,"E75.MirrorCS"),sQuery(id+"F33.wireOp",EDGE,"E77.MirrorCS")])]})});
            var Q77;
            Q77=makeQuery(id+"F35.opBoolean","SPLIT",BODY,{"disambiguationData":[OD(84.0)],"derivedFrom":makeQuery(id+"F34.opExtrude","SWEPT_BODY",BODY,{"disambiguationData":[OSD([sQuery(id+"F0.wireOp",EDGE,"E0.bottom"),sQuery(id+"F0.wireOp",EDGE,"E0.left"),sQuery(id+"F0.wireOp",EDGE,"E0.right"),sQuery(id+"F0.wireOp",EDGE,"E1"),sQuery(id+"F0.wireOp",EDGE,"E2"),sQuery(id+"F0.wireOp",EDGE,"E3"),sQuery(id+"F0.wireOp",EDGE,"E4"),sQuery(id+"F0.wireOp",EDGE,"E5"),sQuery(id+"F0.wireOp",EDGE,"E6"),sQuery(id+"F0.wireOp",EDGE,"E7"),sQuery(id+"F0.wireOp",EDGE,"E8"),sQuery(id+"F0.wireOp",EDGE,"E9"),sQuery(id+"F0.wireOp",EDGE,"E10"),sQuery(id+"F0.wireOp",EDGE,"E11"),sQuery(id+"F0.wireOp",EDGE,"E12"),sQuery(id+"F0.wireOp",EDGE,"E13"),sQuery(id+"F0.wireOp",EDGE,"E14"),sQuery(id+"F0.wireOp",EDGE,"E15"),sQuery(id+"F0.wireOp",EDGE,"E16"),sQuery(id+"F0.wireOp",EDGE,"E17"),sQuery(id+"F0.wireOp",EDGE,"E18"),sQuery(id+"F0.wireOp",EDGE,"E19"),sQuery(id+"F0.wireOp",EDGE,"E20"),sQuery(id+"F33.wireOp",EDGE,"E66"),sQuery(id+"F33.wireOp",EDGE,"E68"),sQuery(id+"F33.wireOp",EDGE,"E69"),sQuery(id+"F33.wireOp",EDGE,"E70"),sQuery(id+"F33.wireOp",EDGE,"E71"),sQuery(id+"F33.wireOp",EDGE,"E72.MirrorCS"),sQuery(id+"F33.wireOp",EDGE,"E73.MirrorCS"),sQuery(id+"F33.wireOp",EDGE,"E74.MirrorCS"),sQuery(id+"F33.wireOp",EDGE,"E75.MirrorCS"),sQuery(id+"F33.wireOp",EDGE,"E77.MirrorCS")])]})});
            var Q78;
            Q78=makeQuery(id+"F35.opBoolean","SPLIT",BODY,{"disambiguationData":[OD(85.0)],"derivedFrom":makeQuery(id+"F34.opExtrude","SWEPT_BODY",BODY,{"disambiguationData":[OSD([sQuery(id+"F0.wireOp",EDGE,"E0.bottom"),sQuery(id+"F0.wireOp",EDGE,"E0.left"),sQuery(id+"F0.wireOp",EDGE,"E0.right"),sQuery(id+"F0.wireOp",EDGE,"E1"),sQuery(id+"F0.wireOp",EDGE,"E2"),sQuery(id+"F0.wireOp",EDGE,"E3"),sQuery(id+"F0.wireOp",EDGE,"E4"),sQuery(id+"F0.wireOp",EDGE,"E5"),sQuery(id+"F0.wireOp",EDGE,"E6"),sQuery(id+"F0.wireOp",EDGE,"E7"),sQuery(id+"F0.wireOp",EDGE,"E8"),sQuery(id+"F0.wireOp",EDGE,"E9"),sQuery(id+"F0.wireOp",EDGE,"E10"),sQuery(id+"F0.wireOp",EDGE,"E11"),sQuery(id+"F0.wireOp",EDGE,"E12"),sQuery(id+"F0.wireOp",EDGE,"E13"),sQuery(id+"F0.wireOp",EDGE,"E14"),sQuery(id+"F0.wireOp",EDGE,"E15"),sQuery(id+"F0.wireOp",EDGE,"E16"),sQuery(id+"F0.wireOp",EDGE,"E17"),sQuery(id+"F0.wireOp",EDGE,"E18"),sQuery(id+"F0.wireOp",EDGE,"E19"),sQuery(id+"F0.wireOp",EDGE,"E20"),sQuery(id+"F33.wireOp",EDGE,"E66"),sQuery(id+"F33.wireOp",EDGE,"E68"),sQuery(id+"F33.wireOp",EDGE,"E69"),sQuery(id+"F33.wireOp",EDGE,"E70"),sQuery(id+"F33.wireOp",EDGE,"E71"),sQuery(id+"F33.wireOp",EDGE,"E72.MirrorCS"),sQuery(id+"F33.wireOp",EDGE,"E73.MirrorCS"),sQuery(id+"F33.wireOp",EDGE,"E74.MirrorCS"),sQuery(id+"F33.wireOp",EDGE,"E75.MirrorCS"),sQuery(id+"F33.wireOp",EDGE,"E77.MirrorCS")])]})});
            var Q79;
            Q79=makeQuery(id+"F35.opBoolean","SPLIT",BODY,{"disambiguationData":[OD(86.0)],"derivedFrom":makeQuery(id+"F34.opExtrude","SWEPT_BODY",BODY,{"disambiguationData":[OSD([sQuery(id+"F0.wireOp",EDGE,"E0.bottom"),sQuery(id+"F0.wireOp",EDGE,"E0.left"),sQuery(id+"F0.wireOp",EDGE,"E0.right"),sQuery(id+"F0.wireOp",EDGE,"E1"),sQuery(id+"F0.wireOp",EDGE,"E2"),sQuery(id+"F0.wireOp",EDGE,"E3"),sQuery(id+"F0.wireOp",EDGE,"E4"),sQuery(id+"F0.wireOp",EDGE,"E5"),sQuery(id+"F0.wireOp",EDGE,"E6"),sQuery(id+"F0.wireOp",EDGE,"E7"),sQuery(id+"F0.wireOp",EDGE,"E8"),sQuery(id+"F0.wireOp",EDGE,"E9"),sQuery(id+"F0.wireOp",EDGE,"E10"),sQuery(id+"F0.wireOp",EDGE,"E11"),sQuery(id+"F0.wireOp",EDGE,"E12"),sQuery(id+"F0.wireOp",EDGE,"E13"),sQuery(id+"F0.wireOp",EDGE,"E14"),sQuery(id+"F0.wireOp",EDGE,"E15"),sQuery(id+"F0.wireOp",EDGE,"E16"),sQuery(id+"F0.wireOp",EDGE,"E17"),sQuery(id+"F0.wireOp",EDGE,"E18"),sQuery(id+"F0.wireOp",EDGE,"E19"),sQuery(id+"F0.wireOp",EDGE,"E20"),sQuery(id+"F33.wireOp",EDGE,"E66"),sQuery(id+"F33.wireOp",EDGE,"E68"),sQuery(id+"F33.wireOp",EDGE,"E69"),sQuery(id+"F33.wireOp",EDGE,"E70"),sQuery(id+"F33.wireOp",EDGE,"E71"),sQuery(id+"F33.wireOp",EDGE,"E72.MirrorCS"),sQuery(id+"F33.wireOp",EDGE,"E73.MirrorCS"),sQuery(id+"F33.wireOp",EDGE,"E74.MirrorCS"),sQuery(id+"F33.wireOp",EDGE,"E75.MirrorCS"),sQuery(id+"F33.wireOp",EDGE,"E77.MirrorCS")])]})});
            var Q80;
            Q80=makeQuery(id+"F35.opBoolean","SPLIT",BODY,{"disambiguationData":[OD(87.0)],"derivedFrom":makeQuery(id+"F34.opExtrude","SWEPT_BODY",BODY,{"disambiguationData":[OSD([sQuery(id+"F0.wireOp",EDGE,"E0.bottom"),sQuery(id+"F0.wireOp",EDGE,"E0.left"),sQuery(id+"F0.wireOp",EDGE,"E0.right"),sQuery(id+"F0.wireOp",EDGE,"E1"),sQuery(id+"F0.wireOp",EDGE,"E2"),sQuery(id+"F0.wireOp",EDGE,"E3"),sQuery(id+"F0.wireOp",EDGE,"E4"),sQuery(id+"F0.wireOp",EDGE,"E5"),sQuery(id+"F0.wireOp",EDGE,"E6"),sQuery(id+"F0.wireOp",EDGE,"E7"),sQuery(id+"F0.wireOp",EDGE,"E8"),sQuery(id+"F0.wireOp",EDGE,"E9"),sQuery(id+"F0.wireOp",EDGE,"E10"),sQuery(id+"F0.wireOp",EDGE,"E11"),sQuery(id+"F0.wireOp",EDGE,"E12"),sQuery(id+"F0.wireOp",EDGE,"E13"),sQuery(id+"F0.wireOp",EDGE,"E14"),sQuery(id+"F0.wireOp",EDGE,"E15"),sQuery(id+"F0.wireOp",EDGE,"E16"),sQuery(id+"F0.wireOp",EDGE,"E17"),sQuery(id+"F0.wireOp",EDGE,"E18"),sQuery(id+"F0.wireOp",EDGE,"E19"),sQuery(id+"F0.wireOp",EDGE,"E20"),sQuery(id+"F33.wireOp",EDGE,"E66"),sQuery(id+"F33.wireOp",EDGE,"E68"),sQuery(id+"F33.wireOp",EDGE,"E69"),sQuery(id+"F33.wireOp",EDGE,"E70"),sQuery(id+"F33.wireOp",EDGE,"E71"),sQuery(id+"F33.wireOp",EDGE,"E72.MirrorCS"),sQuery(id+"F33.wireOp",EDGE,"E73.MirrorCS"),sQuery(id+"F33.wireOp",EDGE,"E74.MirrorCS"),sQuery(id+"F33.wireOp",EDGE,"E75.MirrorCS"),sQuery(id+"F33.wireOp",EDGE,"E77.MirrorCS")])]})});
            var Q81;
            Q81=makeQuery(id+"F35.opBoolean","SPLIT",BODY,{"disambiguationData":[OD(88.0)],"derivedFrom":makeQuery(id+"F34.opExtrude","SWEPT_BODY",BODY,{"disambiguationData":[OSD([sQuery(id+"F0.wireOp",EDGE,"E0.bottom"),sQuery(id+"F0.wireOp",EDGE,"E0.left"),sQuery(id+"F0.wireOp",EDGE,"E0.right"),sQuery(id+"F0.wireOp",EDGE,"E1"),sQuery(id+"F0.wireOp",EDGE,"E2"),sQuery(id+"F0.wireOp",EDGE,"E3"),sQuery(id+"F0.wireOp",EDGE,"E4"),sQuery(id+"F0.wireOp",EDGE,"E5"),sQuery(id+"F0.wireOp",EDGE,"E6"),sQuery(id+"F0.wireOp",EDGE,"E7"),sQuery(id+"F0.wireOp",EDGE,"E8"),sQuery(id+"F0.wireOp",EDGE,"E9"),sQuery(id+"F0.wireOp",EDGE,"E10"),sQuery(id+"F0.wireOp",EDGE,"E11"),sQuery(id+"F0.wireOp",EDGE,"E12"),sQuery(id+"F0.wireOp",EDGE,"E13"),sQuery(id+"F0.wireOp",EDGE,"E14"),sQuery(id+"F0.wireOp",EDGE,"E15"),sQuery(id+"F0.wireOp",EDGE,"E16"),sQuery(id+"F0.wireOp",EDGE,"E17"),sQuery(id+"F0.wireOp",EDGE,"E18"),sQuery(id+"F0.wireOp",EDGE,"E19"),sQuery(id+"F0.wireOp",EDGE,"E20"),sQuery(id+"F33.wireOp",EDGE,"E66"),sQuery(id+"F33.wireOp",EDGE,"E68"),sQuery(id+"F33.wireOp",EDGE,"E69"),sQuery(id+"F33.wireOp",EDGE,"E70"),sQuery(id+"F33.wireOp",EDGE,"E71"),sQuery(id+"F33.wireOp",EDGE,"E72.MirrorCS"),sQuery(id+"F33.wireOp",EDGE,"E73.MirrorCS"),sQuery(id+"F33.wireOp",EDGE,"E74.MirrorCS"),sQuery(id+"F33.wireOp",EDGE,"E75.MirrorCS"),sQuery(id+"F33.wireOp",EDGE,"E77.MirrorCS")])]})});
            var Q82;
            Q82=makeQuery(id+"F35.opBoolean","SPLIT",BODY,{"disambiguationData":[OD(89.0)],"derivedFrom":makeQuery(id+"F34.opExtrude","SWEPT_BODY",BODY,{"disambiguationData":[OSD([sQuery(id+"F0.wireOp",EDGE,"E0.bottom"),sQuery(id+"F0.wireOp",EDGE,"E0.left"),sQuery(id+"F0.wireOp",EDGE,"E0.right"),sQuery(id+"F0.wireOp",EDGE,"E1"),sQuery(id+"F0.wireOp",EDGE,"E2"),sQuery(id+"F0.wireOp",EDGE,"E3"),sQuery(id+"F0.wireOp",EDGE,"E4"),sQuery(id+"F0.wireOp",EDGE,"E5"),sQuery(id+"F0.wireOp",EDGE,"E6"),sQuery(id+"F0.wireOp",EDGE,"E7"),sQuery(id+"F0.wireOp",EDGE,"E8"),sQuery(id+"F0.wireOp",EDGE,"E9"),sQuery(id+"F0.wireOp",EDGE,"E10"),sQuery(id+"F0.wireOp",EDGE,"E11"),sQuery(id+"F0.wireOp",EDGE,"E12"),sQuery(id+"F0.wireOp",EDGE,"E13"),sQuery(id+"F0.wireOp",EDGE,"E14"),sQuery(id+"F0.wireOp",EDGE,"E15"),sQuery(id+"F0.wireOp",EDGE,"E16"),sQuery(id+"F0.wireOp",EDGE,"E17"),sQuery(id+"F0.wireOp",EDGE,"E18"),sQuery(id+"F0.wireOp",EDGE,"E19"),sQuery(id+"F0.wireOp",EDGE,"E20"),sQuery(id+"F33.wireOp",EDGE,"E66"),sQuery(id+"F33.wireOp",EDGE,"E68"),sQuery(id+"F33.wireOp",EDGE,"E69"),sQuery(id+"F33.wireOp",EDGE,"E70"),sQuery(id+"F33.wireOp",EDGE,"E71"),sQuery(id+"F33.wireOp",EDGE,"E72.MirrorCS"),sQuery(id+"F33.wireOp",EDGE,"E73.MirrorCS"),sQuery(id+"F33.wireOp",EDGE,"E74.MirrorCS"),sQuery(id+"F33.wireOp",EDGE,"E75.MirrorCS"),sQuery(id+"F33.wireOp",EDGE,"E77.MirrorCS")])]})});
            var Q83;
            Q83=makeQuery(id+"F35.opBoolean","SPLIT",BODY,{"disambiguationData":[OD(90.0)],"derivedFrom":makeQuery(id+"F34.opExtrude","SWEPT_BODY",BODY,{"disambiguationData":[OSD([sQuery(id+"F0.wireOp",EDGE,"E0.bottom"),sQuery(id+"F0.wireOp",EDGE,"E0.left"),sQuery(id+"F0.wireOp",EDGE,"E0.right"),sQuery(id+"F0.wireOp",EDGE,"E1"),sQuery(id+"F0.wireOp",EDGE,"E2"),sQuery(id+"F0.wireOp",EDGE,"E3"),sQuery(id+"F0.wireOp",EDGE,"E4"),sQuery(id+"F0.wireOp",EDGE,"E5"),sQuery(id+"F0.wireOp",EDGE,"E6"),sQuery(id+"F0.wireOp",EDGE,"E7"),sQuery(id+"F0.wireOp",EDGE,"E8"),sQuery(id+"F0.wireOp",EDGE,"E9"),sQuery(id+"F0.wireOp",EDGE,"E10"),sQuery(id+"F0.wireOp",EDGE,"E11"),sQuery(id+"F0.wireOp",EDGE,"E12"),sQuery(id+"F0.wireOp",EDGE,"E13"),sQuery(id+"F0.wireOp",EDGE,"E14"),sQuery(id+"F0.wireOp",EDGE,"E15"),sQuery(id+"F0.wireOp",EDGE,"E16"),sQuery(id+"F0.wireOp",EDGE,"E17"),sQuery(id+"F0.wireOp",EDGE,"E18"),sQuery(id+"F0.wireOp",EDGE,"E19"),sQuery(id+"F0.wireOp",EDGE,"E20"),sQuery(id+"F33.wireOp",EDGE,"E66"),sQuery(id+"F33.wireOp",EDGE,"E68"),sQuery(id+"F33.wireOp",EDGE,"E69"),sQuery(id+"F33.wireOp",EDGE,"E70"),sQuery(id+"F33.wireOp",EDGE,"E71"),sQuery(id+"F33.wireOp",EDGE,"E72.MirrorCS"),sQuery(id+"F33.wireOp",EDGE,"E73.MirrorCS"),sQuery(id+"F33.wireOp",EDGE,"E74.MirrorCS"),sQuery(id+"F33.wireOp",EDGE,"E75.MirrorCS"),sQuery(id+"F33.wireOp",EDGE,"E77.MirrorCS")])]})});
            var Q84;
            Q84=makeQuery(id+"F35.opBoolean","SPLIT",BODY,{"disambiguationData":[OD(91.0)],"derivedFrom":makeQuery(id+"F34.opExtrude","SWEPT_BODY",BODY,{"disambiguationData":[OSD([sQuery(id+"F0.wireOp",EDGE,"E0.bottom"),sQuery(id+"F0.wireOp",EDGE,"E0.left"),sQuery(id+"F0.wireOp",EDGE,"E0.right"),sQuery(id+"F0.wireOp",EDGE,"E1"),sQuery(id+"F0.wireOp",EDGE,"E2"),sQuery(id+"F0.wireOp",EDGE,"E3"),sQuery(id+"F0.wireOp",EDGE,"E4"),sQuery(id+"F0.wireOp",EDGE,"E5"),sQuery(id+"F0.wireOp",EDGE,"E6"),sQuery(id+"F0.wireOp",EDGE,"E7"),sQuery(id+"F0.wireOp",EDGE,"E8"),sQuery(id+"F0.wireOp",EDGE,"E9"),sQuery(id+"F0.wireOp",EDGE,"E10"),sQuery(id+"F0.wireOp",EDGE,"E11"),sQuery(id+"F0.wireOp",EDGE,"E12"),sQuery(id+"F0.wireOp",EDGE,"E13"),sQuery(id+"F0.wireOp",EDGE,"E14"),sQuery(id+"F0.wireOp",EDGE,"E15"),sQuery(id+"F0.wireOp",EDGE,"E16"),sQuery(id+"F0.wireOp",EDGE,"E17"),sQuery(id+"F0.wireOp",EDGE,"E18"),sQuery(id+"F0.wireOp",EDGE,"E19"),sQuery(id+"F0.wireOp",EDGE,"E20"),sQuery(id+"F33.wireOp",EDGE,"E66"),sQuery(id+"F33.wireOp",EDGE,"E68"),sQuery(id+"F33.wireOp",EDGE,"E69"),sQuery(id+"F33.wireOp",EDGE,"E70"),sQuery(id+"F33.wireOp",EDGE,"E71"),sQuery(id+"F33.wireOp",EDGE,"E72.MirrorCS"),sQuery(id+"F33.wireOp",EDGE,"E73.MirrorCS"),sQuery(id+"F33.wireOp",EDGE,"E74.MirrorCS"),sQuery(id+"F33.wireOp",EDGE,"E75.MirrorCS"),sQuery(id+"F33.wireOp",EDGE,"E77.MirrorCS")])]})});
            var Q85;
            Q85=makeQuery(id+"F35.opBoolean","SPLIT",BODY,{"disambiguationData":[OD(92.0)],"derivedFrom":makeQuery(id+"F34.opExtrude","SWEPT_BODY",BODY,{"disambiguationData":[OSD([sQuery(id+"F0.wireOp",EDGE,"E0.bottom"),sQuery(id+"F0.wireOp",EDGE,"E0.left"),sQuery(id+"F0.wireOp",EDGE,"E0.right"),sQuery(id+"F0.wireOp",EDGE,"E1"),sQuery(id+"F0.wireOp",EDGE,"E2"),sQuery(id+"F0.wireOp",EDGE,"E3"),sQuery(id+"F0.wireOp",EDGE,"E4"),sQuery(id+"F0.wireOp",EDGE,"E5"),sQuery(id+"F0.wireOp",EDGE,"E6"),sQuery(id+"F0.wireOp",EDGE,"E7"),sQuery(id+"F0.wireOp",EDGE,"E8"),sQuery(id+"F0.wireOp",EDGE,"E9"),sQuery(id+"F0.wireOp",EDGE,"E10"),sQuery(id+"F0.wireOp",EDGE,"E11"),sQuery(id+"F0.wireOp",EDGE,"E12"),sQuery(id+"F0.wireOp",EDGE,"E13"),sQuery(id+"F0.wireOp",EDGE,"E14"),sQuery(id+"F0.wireOp",EDGE,"E15"),sQuery(id+"F0.wireOp",EDGE,"E16"),sQuery(id+"F0.wireOp",EDGE,"E17"),sQuery(id+"F0.wireOp",EDGE,"E18"),sQuery(id+"F0.wireOp",EDGE,"E19"),sQuery(id+"F0.wireOp",EDGE,"E20"),sQuery(id+"F33.wireOp",EDGE,"E66"),sQuery(id+"F33.wireOp",EDGE,"E68"),sQuery(id+"F33.wireOp",EDGE,"E69"),sQuery(id+"F33.wireOp",EDGE,"E70"),sQuery(id+"F33.wireOp",EDGE,"E71"),sQuery(id+"F33.wireOp",EDGE,"E72.MirrorCS"),sQuery(id+"F33.wireOp",EDGE,"E73.MirrorCS"),sQuery(id+"F33.wireOp",EDGE,"E74.MirrorCS"),sQuery(id+"F33.wireOp",EDGE,"E75.MirrorCS"),sQuery(id+"F33.wireOp",EDGE,"E77.MirrorCS")])]})});
            var Q86;
            Q86=makeQuery(id+"F35.opBoolean","SPLIT",BODY,{"disambiguationData":[OD(93.0)],"derivedFrom":makeQuery(id+"F34.opExtrude","SWEPT_BODY",BODY,{"disambiguationData":[OSD([sQuery(id+"F0.wireOp",EDGE,"E0.bottom"),sQuery(id+"F0.wireOp",EDGE,"E0.left"),sQuery(id+"F0.wireOp",EDGE,"E0.right"),sQuery(id+"F0.wireOp",EDGE,"E1"),sQuery(id+"F0.wireOp",EDGE,"E2"),sQuery(id+"F0.wireOp",EDGE,"E3"),sQuery(id+"F0.wireOp",EDGE,"E4"),sQuery(id+"F0.wireOp",EDGE,"E5"),sQuery(id+"F0.wireOp",EDGE,"E6"),sQuery(id+"F0.wireOp",EDGE,"E7"),sQuery(id+"F0.wireOp",EDGE,"E8"),sQuery(id+"F0.wireOp",EDGE,"E9"),sQuery(id+"F0.wireOp",EDGE,"E10"),sQuery(id+"F0.wireOp",EDGE,"E11"),sQuery(id+"F0.wireOp",EDGE,"E12"),sQuery(id+"F0.wireOp",EDGE,"E13"),sQuery(id+"F0.wireOp",EDGE,"E14"),sQuery(id+"F0.wireOp",EDGE,"E15"),sQuery(id+"F0.wireOp",EDGE,"E16"),sQuery(id+"F0.wireOp",EDGE,"E17"),sQuery(id+"F0.wireOp",EDGE,"E18"),sQuery(id+"F0.wireOp",EDGE,"E19"),sQuery(id+"F0.wireOp",EDGE,"E20"),sQuery(id+"F33.wireOp",EDGE,"E66"),sQuery(id+"F33.wireOp",EDGE,"E68"),sQuery(id+"F33.wireOp",EDGE,"E69"),sQuery(id+"F33.wireOp",EDGE,"E70"),sQuery(id+"F33.wireOp",EDGE,"E71"),sQuery(id+"F33.wireOp",EDGE,"E72.MirrorCS"),sQuery(id+"F33.wireOp",EDGE,"E73.MirrorCS"),sQuery(id+"F33.wireOp",EDGE,"E74.MirrorCS"),sQuery(id+"F33.wireOp",EDGE,"E75.MirrorCS"),sQuery(id+"F33.wireOp",EDGE,"E77.MirrorCS")])]})});
            var Q87;
            Q87=makeQuery(id+"F35.opBoolean","SPLIT",BODY,{"disambiguationData":[OD(94.0)],"derivedFrom":makeQuery(id+"F34.opExtrude","SWEPT_BODY",BODY,{"disambiguationData":[OSD([sQuery(id+"F0.wireOp",EDGE,"E0.bottom"),sQuery(id+"F0.wireOp",EDGE,"E0.left"),sQuery(id+"F0.wireOp",EDGE,"E0.right"),sQuery(id+"F0.wireOp",EDGE,"E1"),sQuery(id+"F0.wireOp",EDGE,"E2"),sQuery(id+"F0.wireOp",EDGE,"E3"),sQuery(id+"F0.wireOp",EDGE,"E4"),sQuery(id+"F0.wireOp",EDGE,"E5"),sQuery(id+"F0.wireOp",EDGE,"E6"),sQuery(id+"F0.wireOp",EDGE,"E7"),sQuery(id+"F0.wireOp",EDGE,"E8"),sQuery(id+"F0.wireOp",EDGE,"E9"),sQuery(id+"F0.wireOp",EDGE,"E10"),sQuery(id+"F0.wireOp",EDGE,"E11"),sQuery(id+"F0.wireOp",EDGE,"E12"),sQuery(id+"F0.wireOp",EDGE,"E13"),sQuery(id+"F0.wireOp",EDGE,"E14"),sQuery(id+"F0.wireOp",EDGE,"E15"),sQuery(id+"F0.wireOp",EDGE,"E16"),sQuery(id+"F0.wireOp",EDGE,"E17"),sQuery(id+"F0.wireOp",EDGE,"E18"),sQuery(id+"F0.wireOp",EDGE,"E19"),sQuery(id+"F0.wireOp",EDGE,"E20"),sQuery(id+"F33.wireOp",EDGE,"E66"),sQuery(id+"F33.wireOp",EDGE,"E68"),sQuery(id+"F33.wireOp",EDGE,"E69"),sQuery(id+"F33.wireOp",EDGE,"E70"),sQuery(id+"F33.wireOp",EDGE,"E71"),sQuery(id+"F33.wireOp",EDGE,"E72.MirrorCS"),sQuery(id+"F33.wireOp",EDGE,"E73.MirrorCS"),sQuery(id+"F33.wireOp",EDGE,"E74.MirrorCS"),sQuery(id+"F33.wireOp",EDGE,"E75.MirrorCS"),sQuery(id+"F33.wireOp",EDGE,"E77.MirrorCS")])]})});
            var Q88;
            Q88=makeQuery(id+"F35.opBoolean","SPLIT",BODY,{"disambiguationData":[OD(21.0)],"derivedFrom":makeQuery(id+"F34.opExtrude","SWEPT_BODY",BODY,{"disambiguationData":[OSD([sQuery(id+"F0.wireOp",EDGE,"E0.bottom"),sQuery(id+"F0.wireOp",EDGE,"E0.left"),sQuery(id+"F0.wireOp",EDGE,"E0.right"),sQuery(id+"F0.wireOp",EDGE,"E1"),sQuery(id+"F0.wireOp",EDGE,"E2"),sQuery(id+"F0.wireOp",EDGE,"E3"),sQuery(id+"F0.wireOp",EDGE,"E4"),sQuery(id+"F0.wireOp",EDGE,"E5"),sQuery(id+"F0.wireOp",EDGE,"E6"),sQuery(id+"F0.wireOp",EDGE,"E7"),sQuery(id+"F0.wireOp",EDGE,"E8"),sQuery(id+"F0.wireOp",EDGE,"E9"),sQuery(id+"F0.wireOp",EDGE,"E10"),sQuery(id+"F0.wireOp",EDGE,"E11"),sQuery(id+"F0.wireOp",EDGE,"E12"),sQuery(id+"F0.wireOp",EDGE,"E13"),sQuery(id+"F0.wireOp",EDGE,"E14"),sQuery(id+"F0.wireOp",EDGE,"E15"),sQuery(id+"F0.wireOp",EDGE,"E16"),sQuery(id+"F0.wireOp",EDGE,"E17"),sQuery(id+"F0.wireOp",EDGE,"E18"),sQuery(id+"F0.wireOp",EDGE,"E19"),sQuery(id+"F0.wireOp",EDGE,"E20"),sQuery(id+"F33.wireOp",EDGE,"E66"),sQuery(id+"F33.wireOp",EDGE,"E68"),sQuery(id+"F33.wireOp",EDGE,"E69"),sQuery(id+"F33.wireOp",EDGE,"E70"),sQuery(id+"F33.wireOp",EDGE,"E71"),sQuery(id+"F33.wireOp",EDGE,"E72.MirrorCS"),sQuery(id+"F33.wireOp",EDGE,"E73.MirrorCS"),sQuery(id+"F33.wireOp",EDGE,"E74.MirrorCS"),sQuery(id+"F33.wireOp",EDGE,"E75.MirrorCS"),sQuery(id+"F33.wireOp",EDGE,"E77.MirrorCS")])]})});
            var Q89;
            Q89=makeQuery(id+"F35.opBoolean","SPLIT",BODY,{"disambiguationData":[OD(34.0)],"derivedFrom":makeQuery(id+"F34.opExtrude","SWEPT_BODY",BODY,{"disambiguationData":[OSD([sQuery(id+"F0.wireOp",EDGE,"E0.bottom"),sQuery(id+"F0.wireOp",EDGE,"E0.left"),sQuery(id+"F0.wireOp",EDGE,"E0.right"),sQuery(id+"F0.wireOp",EDGE,"E1"),sQuery(id+"F0.wireOp",EDGE,"E2"),sQuery(id+"F0.wireOp",EDGE,"E3"),sQuery(id+"F0.wireOp",EDGE,"E4"),sQuery(id+"F0.wireOp",EDGE,"E5"),sQuery(id+"F0.wireOp",EDGE,"E6"),sQuery(id+"F0.wireOp",EDGE,"E7"),sQuery(id+"F0.wireOp",EDGE,"E8"),sQuery(id+"F0.wireOp",EDGE,"E9"),sQuery(id+"F0.wireOp",EDGE,"E10"),sQuery(id+"F0.wireOp",EDGE,"E11"),sQuery(id+"F0.wireOp",EDGE,"E12"),sQuery(id+"F0.wireOp",EDGE,"E13"),sQuery(id+"F0.wireOp",EDGE,"E14"),sQuery(id+"F0.wireOp",EDGE,"E15"),sQuery(id+"F0.wireOp",EDGE,"E16"),sQuery(id+"F0.wireOp",EDGE,"E17"),sQuery(id+"F0.wireOp",EDGE,"E18"),sQuery(id+"F0.wireOp",EDGE,"E19"),sQuery(id+"F0.wireOp",EDGE,"E20"),sQuery(id+"F33.wireOp",EDGE,"E66"),sQuery(id+"F33.wireOp",EDGE,"E68"),sQuery(id+"F33.wireOp",EDGE,"E69"),sQuery(id+"F33.wireOp",EDGE,"E70"),sQuery(id+"F33.wireOp",EDGE,"E71"),sQuery(id+"F33.wireOp",EDGE,"E72.MirrorCS"),sQuery(id+"F33.wireOp",EDGE,"E73.MirrorCS"),sQuery(id+"F33.wireOp",EDGE,"E74.MirrorCS"),sQuery(id+"F33.wireOp",EDGE,"E75.MirrorCS"),sQuery(id+"F33.wireOp",EDGE,"E77.MirrorCS")])]})});
            var Q90;
            Q90=makeQuery(id+"F35.opBoolean","SPLIT",BODY,{"disambiguationData":[OD(36.0)],"derivedFrom":makeQuery(id+"F34.opExtrude","SWEPT_BODY",BODY,{"disambiguationData":[OSD([sQuery(id+"F0.wireOp",EDGE,"E0.bottom"),sQuery(id+"F0.wireOp",EDGE,"E0.left"),sQuery(id+"F0.wireOp",EDGE,"E0.right"),sQuery(id+"F0.wireOp",EDGE,"E1"),sQuery(id+"F0.wireOp",EDGE,"E2"),sQuery(id+"F0.wireOp",EDGE,"E3"),sQuery(id+"F0.wireOp",EDGE,"E4"),sQuery(id+"F0.wireOp",EDGE,"E5"),sQuery(id+"F0.wireOp",EDGE,"E6"),sQuery(id+"F0.wireOp",EDGE,"E7"),sQuery(id+"F0.wireOp",EDGE,"E8"),sQuery(id+"F0.wireOp",EDGE,"E9"),sQuery(id+"F0.wireOp",EDGE,"E10"),sQuery(id+"F0.wireOp",EDGE,"E11"),sQuery(id+"F0.wireOp",EDGE,"E12"),sQuery(id+"F0.wireOp",EDGE,"E13"),sQuery(id+"F0.wireOp",EDGE,"E14"),sQuery(id+"F0.wireOp",EDGE,"E15"),sQuery(id+"F0.wireOp",EDGE,"E16"),sQuery(id+"F0.wireOp",EDGE,"E17"),sQuery(id+"F0.wireOp",EDGE,"E18"),sQuery(id+"F0.wireOp",EDGE,"E19"),sQuery(id+"F0.wireOp",EDGE,"E20"),sQuery(id+"F33.wireOp",EDGE,"E66"),sQuery(id+"F33.wireOp",EDGE,"E68"),sQuery(id+"F33.wireOp",EDGE,"E69"),sQuery(id+"F33.wireOp",EDGE,"E70"),sQuery(id+"F33.wireOp",EDGE,"E71"),sQuery(id+"F33.wireOp",EDGE,"E72.MirrorCS"),sQuery(id+"F33.wireOp",EDGE,"E73.MirrorCS"),sQuery(id+"F33.wireOp",EDGE,"E74.MirrorCS"),sQuery(id+"F33.wireOp",EDGE,"E75.MirrorCS"),sQuery(id+"F33.wireOp",EDGE,"E77.MirrorCS")])]})});
            var Q91;
            Q91=makeQuery(id+"F35.opBoolean","SPLIT",BODY,{"disambiguationData":[OD(56.0)],"derivedFrom":makeQuery(id+"F34.opExtrude","SWEPT_BODY",BODY,{"disambiguationData":[OSD([sQuery(id+"F0.wireOp",EDGE,"E0.bottom"),sQuery(id+"F0.wireOp",EDGE,"E0.left"),sQuery(id+"F0.wireOp",EDGE,"E0.right"),sQuery(id+"F0.wireOp",EDGE,"E1"),sQuery(id+"F0.wireOp",EDGE,"E2"),sQuery(id+"F0.wireOp",EDGE,"E3"),sQuery(id+"F0.wireOp",EDGE,"E4"),sQuery(id+"F0.wireOp",EDGE,"E5"),sQuery(id+"F0.wireOp",EDGE,"E6"),sQuery(id+"F0.wireOp",EDGE,"E7"),sQuery(id+"F0.wireOp",EDGE,"E8"),sQuery(id+"F0.wireOp",EDGE,"E9"),sQuery(id+"F0.wireOp",EDGE,"E10"),sQuery(id+"F0.wireOp",EDGE,"E11"),sQuery(id+"F0.wireOp",EDGE,"E12"),sQuery(id+"F0.wireOp",EDGE,"E13"),sQuery(id+"F0.wireOp",EDGE,"E14"),sQuery(id+"F0.wireOp",EDGE,"E15"),sQuery(id+"F0.wireOp",EDGE,"E16"),sQuery(id+"F0.wireOp",EDGE,"E17"),sQuery(id+"F0.wireOp",EDGE,"E18"),sQuery(id+"F0.wireOp",EDGE,"E19"),sQuery(id+"F0.wireOp",EDGE,"E20"),sQuery(id+"F33.wireOp",EDGE,"E66"),sQuery(id+"F33.wireOp",EDGE,"E68"),sQuery(id+"F33.wireOp",EDGE,"E69"),sQuery(id+"F33.wireOp",EDGE,"E70"),sQuery(id+"F33.wireOp",EDGE,"E71"),sQuery(id+"F33.wireOp",EDGE,"E72.MirrorCS"),sQuery(id+"F33.wireOp",EDGE,"E73.MirrorCS"),sQuery(id+"F33.wireOp",EDGE,"E74.MirrorCS"),sQuery(id+"F33.wireOp",EDGE,"E75.MirrorCS"),sQuery(id+"F33.wireOp",EDGE,"E77.MirrorCS")])]})});
            var Q92;
            Q92=makeQuery(id+"F35.opBoolean","SPLIT",BODY,{"disambiguationData":[OD(57.0)],"derivedFrom":makeQuery(id+"F34.opExtrude","SWEPT_BODY",BODY,{"disambiguationData":[OSD([sQuery(id+"F0.wireOp",EDGE,"E0.bottom"),sQuery(id+"F0.wireOp",EDGE,"E0.left"),sQuery(id+"F0.wireOp",EDGE,"E0.right"),sQuery(id+"F0.wireOp",EDGE,"E1"),sQuery(id+"F0.wireOp",EDGE,"E2"),sQuery(id+"F0.wireOp",EDGE,"E3"),sQuery(id+"F0.wireOp",EDGE,"E4"),sQuery(id+"F0.wireOp",EDGE,"E5"),sQuery(id+"F0.wireOp",EDGE,"E6"),sQuery(id+"F0.wireOp",EDGE,"E7"),sQuery(id+"F0.wireOp",EDGE,"E8"),sQuery(id+"F0.wireOp",EDGE,"E9"),sQuery(id+"F0.wireOp",EDGE,"E10"),sQuery(id+"F0.wireOp",EDGE,"E11"),sQuery(id+"F0.wireOp",EDGE,"E12"),sQuery(id+"F0.wireOp",EDGE,"E13"),sQuery(id+"F0.wireOp",EDGE,"E14"),sQuery(id+"F0.wireOp",EDGE,"E15"),sQuery(id+"F0.wireOp",EDGE,"E16"),sQuery(id+"F0.wireOp",EDGE,"E17"),sQuery(id+"F0.wireOp",EDGE,"E18"),sQuery(id+"F0.wireOp",EDGE,"E19"),sQuery(id+"F0.wireOp",EDGE,"E20"),sQuery(id+"F33.wireOp",EDGE,"E66"),sQuery(id+"F33.wireOp",EDGE,"E68"),sQuery(id+"F33.wireOp",EDGE,"E69"),sQuery(id+"F33.wireOp",EDGE,"E70"),sQuery(id+"F33.wireOp",EDGE,"E71"),sQuery(id+"F33.wireOp",EDGE,"E72.MirrorCS"),sQuery(id+"F33.wireOp",EDGE,"E73.MirrorCS"),sQuery(id+"F33.wireOp",EDGE,"E74.MirrorCS"),sQuery(id+"F33.wireOp",EDGE,"E75.MirrorCS"),sQuery(id+"F33.wireOp",EDGE,"E77.MirrorCS")])]})});
            var Q93;
            Q93=makeQuery(id+"F35.opBoolean","SPLIT",BODY,{"disambiguationData":[OD(65.0)],"derivedFrom":makeQuery(id+"F34.opExtrude","SWEPT_BODY",BODY,{"disambiguationData":[OSD([sQuery(id+"F0.wireOp",EDGE,"E0.bottom"),sQuery(id+"F0.wireOp",EDGE,"E0.left"),sQuery(id+"F0.wireOp",EDGE,"E0.right"),sQuery(id+"F0.wireOp",EDGE,"E1"),sQuery(id+"F0.wireOp",EDGE,"E2"),sQuery(id+"F0.wireOp",EDGE,"E3"),sQuery(id+"F0.wireOp",EDGE,"E4"),sQuery(id+"F0.wireOp",EDGE,"E5"),sQuery(id+"F0.wireOp",EDGE,"E6"),sQuery(id+"F0.wireOp",EDGE,"E7"),sQuery(id+"F0.wireOp",EDGE,"E8"),sQuery(id+"F0.wireOp",EDGE,"E9"),sQuery(id+"F0.wireOp",EDGE,"E10"),sQuery(id+"F0.wireOp",EDGE,"E11"),sQuery(id+"F0.wireOp",EDGE,"E12"),sQuery(id+"F0.wireOp",EDGE,"E13"),sQuery(id+"F0.wireOp",EDGE,"E14"),sQuery(id+"F0.wireOp",EDGE,"E15"),sQuery(id+"F0.wireOp",EDGE,"E16"),sQuery(id+"F0.wireOp",EDGE,"E17"),sQuery(id+"F0.wireOp",EDGE,"E18"),sQuery(id+"F0.wireOp",EDGE,"E19"),sQuery(id+"F0.wireOp",EDGE,"E20"),sQuery(id+"F33.wireOp",EDGE,"E66"),sQuery(id+"F33.wireOp",EDGE,"E68"),sQuery(id+"F33.wireOp",EDGE,"E69"),sQuery(id+"F33.wireOp",EDGE,"E70"),sQuery(id+"F33.wireOp",EDGE,"E71"),sQuery(id+"F33.wireOp",EDGE,"E72.MirrorCS"),sQuery(id+"F33.wireOp",EDGE,"E73.MirrorCS"),sQuery(id+"F33.wireOp",EDGE,"E74.MirrorCS"),sQuery(id+"F33.wireOp",EDGE,"E75.MirrorCS"),sQuery(id+"F33.wireOp",EDGE,"E77.MirrorCS")])]})});
            var Q94;
            Q94=makeQuery(id+"F35.opBoolean","SPLIT",BODY,{"disambiguationData":[OD(75.0)],"derivedFrom":makeQuery(id+"F34.opExtrude","SWEPT_BODY",BODY,{"disambiguationData":[OSD([sQuery(id+"F0.wireOp",EDGE,"E0.bottom"),sQuery(id+"F0.wireOp",EDGE,"E0.left"),sQuery(id+"F0.wireOp",EDGE,"E0.right"),sQuery(id+"F0.wireOp",EDGE,"E1"),sQuery(id+"F0.wireOp",EDGE,"E2"),sQuery(id+"F0.wireOp",EDGE,"E3"),sQuery(id+"F0.wireOp",EDGE,"E4"),sQuery(id+"F0.wireOp",EDGE,"E5"),sQuery(id+"F0.wireOp",EDGE,"E6"),sQuery(id+"F0.wireOp",EDGE,"E7"),sQuery(id+"F0.wireOp",EDGE,"E8"),sQuery(id+"F0.wireOp",EDGE,"E9"),sQuery(id+"F0.wireOp",EDGE,"E10"),sQuery(id+"F0.wireOp",EDGE,"E11"),sQuery(id+"F0.wireOp",EDGE,"E12"),sQuery(id+"F0.wireOp",EDGE,"E13"),sQuery(id+"F0.wireOp",EDGE,"E14"),sQuery(id+"F0.wireOp",EDGE,"E15"),sQuery(id+"F0.wireOp",EDGE,"E16"),sQuery(id+"F0.wireOp",EDGE,"E17"),sQuery(id+"F0.wireOp",EDGE,"E18"),sQuery(id+"F0.wireOp",EDGE,"E19"),sQuery(id+"F0.wireOp",EDGE,"E20"),sQuery(id+"F33.wireOp",EDGE,"E66"),sQuery(id+"F33.wireOp",EDGE,"E68"),sQuery(id+"F33.wireOp",EDGE,"E69"),sQuery(id+"F33.wireOp",EDGE,"E70"),sQuery(id+"F33.wireOp",EDGE,"E71"),sQuery(id+"F33.wireOp",EDGE,"E72.MirrorCS"),sQuery(id+"F33.wireOp",EDGE,"E73.MirrorCS"),sQuery(id+"F33.wireOp",EDGE,"E74.MirrorCS"),sQuery(id+"F33.wireOp",EDGE,"E75.MirrorCS"),sQuery(id+"F33.wireOp",EDGE,"E77.MirrorCS")])]})});
            transform(context, id + "F38", {"entities" : qUnion([Q0, Q1, Q2, Q3, Q4, Q5, Q6, Q7, Q8, Q9, Q10, Q11, Q12, Q13, Q14, Q15, Q16, Q17, Q18, Q19, Q20, Q21, Q22, Q23, Q24, Q25, Q26, Q27, Q28, Q29, Q30, Q31, Q32, Q33, Q34, Q35, Q36, Q37, Q38, Q39, Q40, Q41, Q42, Q43, Q44, Q45, Q46, Q47, Q48, Q49, Q50, Q51, Q52, Q53, Q54, Q55, Q56, Q57, Q58, Q59, Q60, Q61, Q62, Q63, Q64, Q65, Q66, Q67, Q68, Q69, Q70, Q71, Q72, Q73, Q74, Q75, Q76, Q77, Q78, Q79, Q80, Q81, Q82, Q83, Q84, Q85, Q86, Q87, Q88, Q89, Q90, Q91, Q92, Q93, Q94]), "transformType" : TransformType.TRANSLATION_3D, "dx" : 0 * mm, "dy" : 0 * mm, "dz" : 1.5 * mm, "makeCopy" : false});
        }
    });
